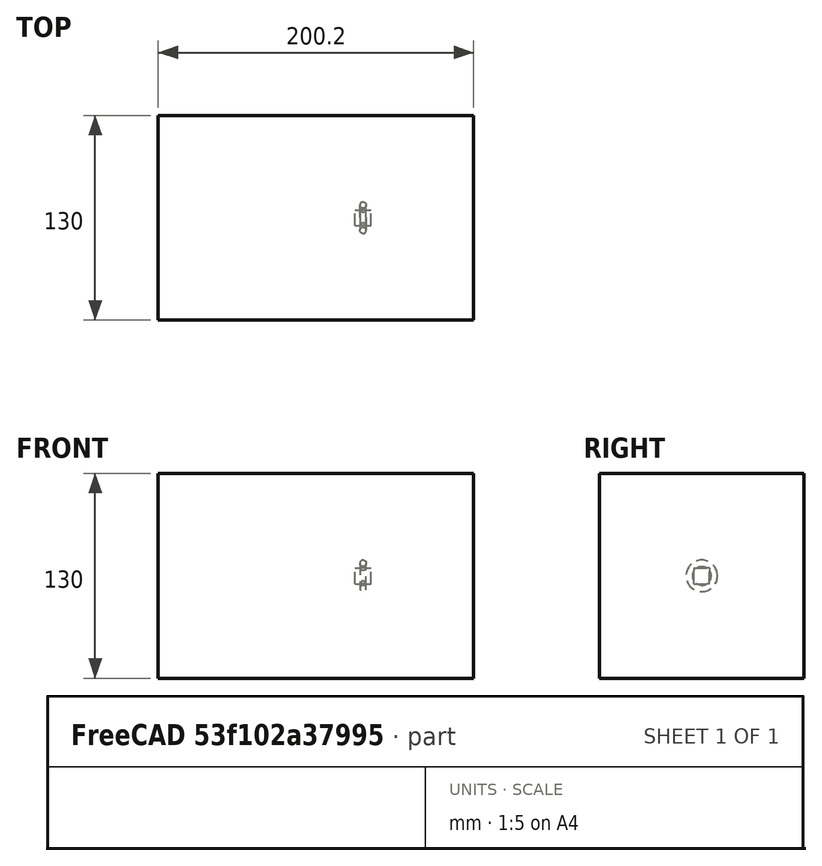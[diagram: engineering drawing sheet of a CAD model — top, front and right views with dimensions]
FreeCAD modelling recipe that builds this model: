
FCSTD DOCUMENT  (FreeCAD 0.21R33694 (Git))
Label: polarArray-7-array-rotated-translated
License: All rights reserved
objects: App::DocumentObjectGroupPython×1251, Part::FeaturePython×4, App::Part×2, Part::MultiFuse×1
note: 4 computed .brp shape members not serialized (recipe doc carries the construction recipe); baked Part::Feature solids carry a one-line shape summary decoded from their .brp

FEATURE [App::DocumentObjectGroupPython] HALFPI  # scripted group (container) (typed FeaturePython)
  name = HALFPI
  value = pi/2.
FEATURE [App::DocumentObjectGroupPython] PI  # scripted group (container) (typed FeaturePython)
  name = PI
  value = 1.*pi
FEATURE [App::DocumentObjectGroupPython] TWOPI  # scripted group (container) (typed FeaturePython)
  name = TWOPI
  value = 2.*pi
FEATURE [App::DocumentObjectGroupPython] Constants  # scripted group (container) (typed FeaturePython)
  Group = -> [HALFPI,PI,TWOPI]
FEATURE [App::DocumentObjectGroupPython] Variables  # scripted group (container) (typed FeaturePython)
FEATURE [App::DocumentObjectGroupPython] Quantities  # scripted group (container) (typed FeaturePython)
FEATURE [App::DocumentObjectGroupPython] Isotopes  # scripted group (container) (typed FeaturePython)
FEATURE [App::DocumentObjectGroupPython] Elements  # scripted group (container) (typed FeaturePython)
FEATURE [App::DocumentObjectGroupPython] Matrix  # scripted group (container) (typed FeaturePython)
FEATURE [App::DocumentObjectGroupPython] Surfaces  # scripted group (container) (typed FeaturePython)
FEATURE [App::DocumentObjectGroupPython] Opticals  # scripted group (container) (typed FeaturePython)
  Group = -> [Matrix,Surfaces]
FEATURE [App::DocumentObjectGroupPython] G4Isotopes  # scripted group (container) (typed FeaturePython)
FEATURE [App::DocumentObjectGroupPython] H_element  # scripted group (container) (typed FeaturePython)
  Z = 1
  atom_value = 1.008
  formula = H
  name = H_element
FEATURE [App::DocumentObjectGroupPython] He_element  # scripted group (container) (typed FeaturePython)
  Z = 2
  atom_value = 4.0026
  formula = He
  name = He_element
FEATURE [App::DocumentObjectGroupPython] Li_element  # scripted group (container) (typed FeaturePython)
  Z = 3
  atom_value = 6.94
  formula = Li
  name = Li_element
FEATURE [App::DocumentObjectGroupPython] Be_element  # scripted group (container) (typed FeaturePython)
  Z = 4
  atom_value = 9.01218
  formula = Be
  name = Be_element
FEATURE [App::DocumentObjectGroupPython] B_element  # scripted group (container) (typed FeaturePython)
  Z = 5
  atom_value = 10.81
  formula = B
  name = B_element
FEATURE [App::DocumentObjectGroupPython] C_element  # scripted group (container) (typed FeaturePython)
  Z = 6
  atom_value = 12.011
  formula = C
  name = C_element
FEATURE [App::DocumentObjectGroupPython] N_element  # scripted group (container) (typed FeaturePython)
  Z = 7
  atom_value = 14.007
  formula = N
  name = N_element
FEATURE [App::DocumentObjectGroupPython] O_element  # scripted group (container) (typed FeaturePython)
  Z = 8
  atom_value = 15.999
  formula = O
  name = O_element
FEATURE [App::DocumentObjectGroupPython] F_element  # scripted group (container) (typed FeaturePython)
  Z = 9
  atom_value = 18.9984
  formula = F
  name = F_element
FEATURE [App::DocumentObjectGroupPython] Ne_element  # scripted group (container) (typed FeaturePython)
  Z = 10
  atom_value = 20.1797
  formula = Ne
  name = Ne_element
FEATURE [App::DocumentObjectGroupPython] Na_element  # scripted group (container) (typed FeaturePython)
  Z = 11
  atom_value = 22.9898
  formula = Na
  name = Na_element
FEATURE [App::DocumentObjectGroupPython] Mg_element  # scripted group (container) (typed FeaturePython)
  Z = 12
  atom_value = 24.305
  formula = Mg
  name = Mg_element
FEATURE [App::DocumentObjectGroupPython] Al_element  # scripted group (container) (typed FeaturePython)
  Z = 13
  atom_value = 26.9815
  formula = Al
  name = Al_element
FEATURE [App::DocumentObjectGroupPython] Si_element  # scripted group (container) (typed FeaturePython)
  Z = 14
  atom_value = 28.085
  formula = Si
  name = Si_element
FEATURE [App::DocumentObjectGroupPython] P_element  # scripted group (container) (typed FeaturePython)
  Z = 15
  atom_value = 30.9738
  formula = P
  name = P_element
FEATURE [App::DocumentObjectGroupPython] S_element  # scripted group (container) (typed FeaturePython)
  Z = 16
  atom_value = 32.06
  formula = S
  name = S_element
FEATURE [App::DocumentObjectGroupPython] Cl_element  # scripted group (container) (typed FeaturePython)
  Z = 17
  atom_value = 35.45
  formula = Cl
  name = Cl_element
FEATURE [App::DocumentObjectGroupPython] Ar_element  # scripted group (container) (typed FeaturePython)
  Z = 18
  atom_value = 39.95
  formula = Ar
  name = Ar_element
FEATURE [App::DocumentObjectGroupPython] K_element  # scripted group (container) (typed FeaturePython)
  Z = 19
  atom_value = 39.0983
  formula = K
  name = K_element
FEATURE [App::DocumentObjectGroupPython] Ca_element  # scripted group (container) (typed FeaturePython)
  Z = 20
  atom_value = 40.078
  formula = Ca
  name = Ca_element
FEATURE [App::DocumentObjectGroupPython] Sc_element  # scripted group (container) (typed FeaturePython)
  Z = 21
  atom_value = 44.9559
  formula = Sc
  name = Sc_element
FEATURE [App::DocumentObjectGroupPython] Ti_element  # scripted group (container) (typed FeaturePython)
  Z = 22
  atom_value = 47.867
  formula = Ti
  name = Ti_element
FEATURE [App::DocumentObjectGroupPython] V_element  # scripted group (container) (typed FeaturePython)
  Z = 23
  atom_value = 50.9415
  formula = V
  name = V_element
FEATURE [App::DocumentObjectGroupPython] Cr_element  # scripted group (container) (typed FeaturePython)
  Z = 24
  atom_value = 51.9961
  formula = Cr
  name = Cr_element
FEATURE [App::DocumentObjectGroupPython] Mn_element  # scripted group (container) (typed FeaturePython)
  Z = 25
  atom_value = 54.938
  formula = Mn
  name = Mn_element
FEATURE [App::DocumentObjectGroupPython] Fe_element  # scripted group (container) (typed FeaturePython)
  Z = 26
  atom_value = 55.845
  formula = Fe
  name = Fe_element
FEATURE [App::DocumentObjectGroupPython] Co_element  # scripted group (container) (typed FeaturePython)
  Z = 27
  atom_value = 58.9332
  formula = Co
  name = Co_element
FEATURE [App::DocumentObjectGroupPython] Ni_element  # scripted group (container) (typed FeaturePython)
  Z = 28
  atom_value = 58.6934
  formula = Ni
  name = Ni_element
FEATURE [App::DocumentObjectGroupPython] Cu_element  # scripted group (container) (typed FeaturePython)
  Z = 29
  atom_value = 63.546
  formula = Cu
  name = Cu_element
FEATURE [App::DocumentObjectGroupPython] Zn_element  # scripted group (container) (typed FeaturePython)
  Z = 30
  atom_value = 65.38
  formula = Zn
  name = Zn_element
FEATURE [App::DocumentObjectGroupPython] Ga_element  # scripted group (container) (typed FeaturePython)
  Z = 31
  atom_value = 69.723
  formula = Ga
  name = Ga_element
FEATURE [App::DocumentObjectGroupPython] Ge_element  # scripted group (container) (typed FeaturePython)
  Z = 32
  atom_value = 72.63
  formula = Ge
  name = Ge_element
FEATURE [App::DocumentObjectGroupPython] As_element  # scripted group (container) (typed FeaturePython)
  Z = 33
  atom_value = 74.9216
  formula = As
  name = As_element
FEATURE [App::DocumentObjectGroupPython] Se_element  # scripted group (container) (typed FeaturePython)
  Z = 34
  atom_value = 78.971
  formula = Se
  name = Se_element
FEATURE [App::DocumentObjectGroupPython] Br_element  # scripted group (container) (typed FeaturePython)
  Z = 35
  atom_value = 79.904
  formula = Br
  name = Br_element
FEATURE [App::DocumentObjectGroupPython] Kr_element  # scripted group (container) (typed FeaturePython)
  Z = 36
  atom_value = 83.798
  formula = Kr
  name = Kr_element
FEATURE [App::DocumentObjectGroupPython] Rb_element  # scripted group (container) (typed FeaturePython)
  Z = 37
  atom_value = 85.4678
  formula = Rb
  name = Rb_element
FEATURE [App::DocumentObjectGroupPython] Sr_element  # scripted group (container) (typed FeaturePython)
  Z = 38
  atom_value = 87.62
  formula = Sr
  name = Sr_element
FEATURE [App::DocumentObjectGroupPython] Y_element  # scripted group (container) (typed FeaturePython)
  Z = 39
  atom_value = 88.9058
  formula = Y
  name = Y_element
FEATURE [App::DocumentObjectGroupPython] Zr_element  # scripted group (container) (typed FeaturePython)
  Z = 40
  atom_value = 91.224
  formula = Zr
  name = Zr_element
FEATURE [App::DocumentObjectGroupPython] Nb_element  # scripted group (container) (typed FeaturePython)
  Z = 41
  atom_value = 92.9064
  formula = Nb
  name = Nb_element
FEATURE [App::DocumentObjectGroupPython] Mo_element  # scripted group (container) (typed FeaturePython)
  Z = 42
  atom_value = 95.95
  formula = Mo
  name = Mo_element
FEATURE [App::DocumentObjectGroupPython] Tc_element  # scripted group (container) (typed FeaturePython)
  Z = 43
  atom_value = 97
  formula = Tc
  name = Tc_element
FEATURE [App::DocumentObjectGroupPython] Ru_element  # scripted group (container) (typed FeaturePython)
  Z = 44
  atom_value = 101.07
  formula = Ru
  name = Ru_element
FEATURE [App::DocumentObjectGroupPython] Rh_element  # scripted group (container) (typed FeaturePython)
  Z = 45
  atom_value = 102.905
  formula = Rh
  name = Rh_element
FEATURE [App::DocumentObjectGroupPython] Pd_element  # scripted group (container) (typed FeaturePython)
  Z = 46
  atom_value = 106.42
  formula = Pd
  name = Pd_element
FEATURE [App::DocumentObjectGroupPython] Ag_element  # scripted group (container) (typed FeaturePython)
  Z = 47
  atom_value = 107.868
  formula = Ag
  name = Ag_element
FEATURE [App::DocumentObjectGroupPython] Cd_element  # scripted group (container) (typed FeaturePython)
  Z = 48
  atom_value = 112.414
  formula = Cd
  name = Cd_element
FEATURE [App::DocumentObjectGroupPython] In_element  # scripted group (container) (typed FeaturePython)
  Z = 49
  atom_value = 114.818
  formula = In
  name = In_element
FEATURE [App::DocumentObjectGroupPython] Sn_element  # scripted group (container) (typed FeaturePython)
  Z = 50
  atom_value = 118.71
  formula = Sn
  name = Sn_element
FEATURE [App::DocumentObjectGroupPython] Sb_element  # scripted group (container) (typed FeaturePython)
  Z = 51
  atom_value = 121.76
  formula = Sb
  name = Sb_element
FEATURE [App::DocumentObjectGroupPython] Te_element  # scripted group (container) (typed FeaturePython)
  Z = 52
  atom_value = 127.6
  formula = Te
  name = Te_element
FEATURE [App::DocumentObjectGroupPython] I_element  # scripted group (container) (typed FeaturePython)
  Z = 53
  atom_value = 126.904
  formula = I
  name = I_element
FEATURE [App::DocumentObjectGroupPython] Xe_element  # scripted group (container) (typed FeaturePython)
  Z = 54
  atom_value = 131.293
  formula = Xe
  name = Xe_element
FEATURE [App::DocumentObjectGroupPython] Cs_element  # scripted group (container) (typed FeaturePython)
  Z = 55
  atom_value = 132.905
  formula = Cs
  name = Cs_element
FEATURE [App::DocumentObjectGroupPython] Ba_element  # scripted group (container) (typed FeaturePython)
  Z = 56
  atom_value = 137.327
  formula = Ba
  name = Ba_element
FEATURE [App::DocumentObjectGroupPython] La_element  # scripted group (container) (typed FeaturePython)
  Z = 57
  atom_value = 138.905
  formula = La
  name = La_element
FEATURE [App::DocumentObjectGroupPython] Ce_element  # scripted group (container) (typed FeaturePython)
  Z = 58
  atom_value = 140.116
  formula = Ce
  name = Ce_element
FEATURE [App::DocumentObjectGroupPython] Pr_element  # scripted group (container) (typed FeaturePython)
  Z = 59
  atom_value = 140.908
  formula = Pr
  name = Pr_element
FEATURE [App::DocumentObjectGroupPython] Nd_element  # scripted group (container) (typed FeaturePython)
  Z = 60
  atom_value = 144.242
  formula = Nd
  name = Nd_element
FEATURE [App::DocumentObjectGroupPython] Pm_element  # scripted group (container) (typed FeaturePython)
  Z = 61
  atom_value = 145
  formula = Pm
  name = Pm_element
FEATURE [App::DocumentObjectGroupPython] Sm_element  # scripted group (container) (typed FeaturePython)
  Z = 62
  atom_value = 150.36
  formula = Sm
  name = Sm_element
FEATURE [App::DocumentObjectGroupPython] Eu_element  # scripted group (container) (typed FeaturePython)
  Z = 63
  atom_value = 151.964
  formula = Eu
  name = Eu_element
FEATURE [App::DocumentObjectGroupPython] Gd_element  # scripted group (container) (typed FeaturePython)
  Z = 64
  atom_value = 157.25
  formula = Gd
  name = Gd_element
FEATURE [App::DocumentObjectGroupPython] Tb_element  # scripted group (container) (typed FeaturePython)
  Z = 65
  atom_value = 158.925
  formula = Tb
  name = Tb_element
FEATURE [App::DocumentObjectGroupPython] Dy_element  # scripted group (container) (typed FeaturePython)
  Z = 66
  atom_value = 162.5
  formula = Dy
  name = Dy_element
FEATURE [App::DocumentObjectGroupPython] Ho_element  # scripted group (container) (typed FeaturePython)
  Z = 67
  atom_value = 164.93
  formula = Ho
  name = Ho_element
FEATURE [App::DocumentObjectGroupPython] Er_element  # scripted group (container) (typed FeaturePython)
  Z = 68
  atom_value = 167.259
  formula = Er
  name = Er_element
FEATURE [App::DocumentObjectGroupPython] Tm_element  # scripted group (container) (typed FeaturePython)
  Z = 69
  atom_value = 168.934
  formula = Tm
  name = Tm_element
FEATURE [App::DocumentObjectGroupPython] Yb_element  # scripted group (container) (typed FeaturePython)
  Z = 70
  atom_value = 173.045
  formula = Yb
  name = Yb_element
FEATURE [App::DocumentObjectGroupPython] Lu_element  # scripted group (container) (typed FeaturePython)
  Z = 71
  atom_value = 174.967
  formula = Lu
  name = Lu_element
FEATURE [App::DocumentObjectGroupPython] Hf_element  # scripted group (container) (typed FeaturePython)
  Z = 72
  atom_value = 178.49
  formula = Hf
  name = Hf_element
FEATURE [App::DocumentObjectGroupPython] Ta_element  # scripted group (container) (typed FeaturePython)
  Z = 73
  atom_value = 180.948
  formula = Ta
  name = Ta_element
FEATURE [App::DocumentObjectGroupPython] W_element  # scripted group (container) (typed FeaturePython)
  Z = 74
  atom_value = 183.84
  formula = W
  name = W_element
FEATURE [App::DocumentObjectGroupPython] Re_element  # scripted group (container) (typed FeaturePython)
  Z = 75
  atom_value = 186.207
  formula = Re
  name = Re_element
FEATURE [App::DocumentObjectGroupPython] Os_element  # scripted group (container) (typed FeaturePython)
  Z = 76
  atom_value = 190.23
  formula = Os
  name = Os_element
FEATURE [App::DocumentObjectGroupPython] Ir_element  # scripted group (container) (typed FeaturePython)
  Z = 77
  atom_value = 192.217
  formula = Ir
  name = Ir_element
FEATURE [App::DocumentObjectGroupPython] Pt_element  # scripted group (container) (typed FeaturePython)
  Z = 78
  atom_value = 195.084
  formula = Pt
  name = Pt_element
FEATURE [App::DocumentObjectGroupPython] Au_element  # scripted group (container) (typed FeaturePython)
  Z = 79
  atom_value = 196.967
  formula = Au
  name = Au_element
FEATURE [App::DocumentObjectGroupPython] Hg_element  # scripted group (container) (typed FeaturePython)
  Z = 80
  atom_value = 200.592
  formula = Hg
  name = Hg_element
FEATURE [App::DocumentObjectGroupPython] Tl_element  # scripted group (container) (typed FeaturePython)
  Z = 81
  atom_value = 204.38
  formula = Tl
  name = Tl_element
FEATURE [App::DocumentObjectGroupPython] Pb_element  # scripted group (container) (typed FeaturePython)
  Z = 82
  atom_value = 207.2
  formula = Pb
  name = Pb_element
FEATURE [App::DocumentObjectGroupPython] Bi_element  # scripted group (container) (typed FeaturePython)
  Z = 83
  atom_value = 208.98
  formula = Bi
  name = Bi_element
FEATURE [App::DocumentObjectGroupPython] Po_element  # scripted group (container) (typed FeaturePython)
  Z = 84
  atom_value = 209
  formula = Po
  name = Po_element
FEATURE [App::DocumentObjectGroupPython] At_element  # scripted group (container) (typed FeaturePython)
  Z = 85
  atom_value = 210
  formula = At
  name = At_element
FEATURE [App::DocumentObjectGroupPython] Rn_element  # scripted group (container) (typed FeaturePython)
  Z = 86
  atom_value = 222
  formula = Rn
  name = Rn_element
FEATURE [App::DocumentObjectGroupPython] Fr_element  # scripted group (container) (typed FeaturePython)
  Z = 87
  atom_value = 223
  formula = Fr
  name = Fr_element
FEATURE [App::DocumentObjectGroupPython] Ra_element  # scripted group (container) (typed FeaturePython)
  Z = 88
  atom_value = 226
  formula = Ra
  name = Ra_element
FEATURE [App::DocumentObjectGroupPython] Ac_element  # scripted group (container) (typed FeaturePython)
  Z = 89
  atom_value = 227
  formula = Ac
  name = Ac_element
FEATURE [App::DocumentObjectGroupPython] Th_element  # scripted group (container) (typed FeaturePython)
  Z = 90
  atom_value = 232.038
  formula = Th
  name = Th_element
FEATURE [App::DocumentObjectGroupPython] Pa_element  # scripted group (container) (typed FeaturePython)
  Z = 91
  atom_value = 231.036
  formula = Pa
  name = Pa_element
FEATURE [App::DocumentObjectGroupPython] U_element  # scripted group (container) (typed FeaturePython)
  Z = 92
  atom_value = 238.029
  formula = U
  name = U_element
FEATURE [App::DocumentObjectGroupPython] Np_element  # scripted group (container) (typed FeaturePython)
  Z = 93
  atom_value = 237
  formula = Np
  name = Np_element
FEATURE [App::DocumentObjectGroupPython] Pu_element  # scripted group (container) (typed FeaturePython)
  Z = 94
  atom_value = 244
  formula = Pu
  name = Pu_element
FEATURE [App::DocumentObjectGroupPython] Am_element  # scripted group (container) (typed FeaturePython)
  Z = 95
  atom_value = 243
  formula = Am
  name = Am_element
FEATURE [App::DocumentObjectGroupPython] Cm_element  # scripted group (container) (typed FeaturePython)
  Z = 96
  atom_value = 247
  formula = Cm
  name = Cm_element
FEATURE [App::DocumentObjectGroupPython] Bk_element  # scripted group (container) (typed FeaturePython)
  Z = 97
  atom_value = 247
  formula = Bk
  name = Bk_element
FEATURE [App::DocumentObjectGroupPython] Cf_element  # scripted group (container) (typed FeaturePython)
  Z = 98
  atom_value = 251
  formula = Cf
  name = Cf_element
FEATURE [App::DocumentObjectGroupPython] G4Elements  # scripted group (container) (typed FeaturePython)
  Group = -> [H_element,He_element,Li_element,Be_element,B_element,C_element,N_element,O_element,F_element,Ne_element,Na_element,Mg_element,Al_element,Si_element,P_element,S_element,Cl_element,Ar_element,K_element,Ca_element,Sc_element,Ti_element,V_element,Cr_element,Mn_element,Fe_element,Co_element,Ni_element,Cu_element,Zn_element,Ga_element,Ge_element,As_element,Se_element,Br_element,Kr_element,Rb_element,+61 more]
FEATURE [App::DocumentObjectGroupPython] H_element001  label="H_element : 0.101"  # scripted group (container) (typed FeaturePython)
  n = 0.101327
FEATURE [App::DocumentObjectGroupPython] C_element001  label="C_element : 0.775"  # scripted group (container) (typed FeaturePython)
  n = 0.7755
FEATURE [App::DocumentObjectGroupPython] N_element001  label="N_element : 0.035"  # scripted group (container) (typed FeaturePython)
  n = 0.035057
FEATURE [App::DocumentObjectGroupPython] O_element001  label="O_element : 0.052"  # scripted group (container) (typed FeaturePython)
  n = 0.0523159
FEATURE [App::DocumentObjectGroupPython] F_element001  label="F_element : 0.017"  # scripted group (container) (typed FeaturePython)
  n = 0.017422
FEATURE [App::DocumentObjectGroupPython] Ca_element001  label="Ca_element : 0.018"  # scripted group (container) (typed FeaturePython)
  n = 0.018378
FEATURE [App::DocumentObjectGroupPython] G4_A_150_TISSUE  label="G4_A-150_TISSUE"  # scripted group (container) (typed FeaturePython)
  Dunit = g/cm3
  Dvalue = 1.127
  Group = -> [H_element001,C_element001,N_element001,O_element001,F_element001,Ca_element001]
  conduct = 2
  density = 1
  expand = 3
  formula = G4_A-150_TISSUE
  name = G4_A-150_TISSUE
  specific = 4
FEATURE [App::DocumentObjectGroupPython] C_element002  label="C_element : 3"  # scripted group (container) (typed FeaturePython)
  n = 3
  ref = C_element
FEATURE [App::DocumentObjectGroupPython] H_element002  label="H_element : 6"  # scripted group (container) (typed FeaturePython)
  n = 6
  ref = H_element
FEATURE [App::DocumentObjectGroupPython] O_element002  label="O_element : 1"  # scripted group (container) (typed FeaturePython)
  n = 1
  ref = O_element
FEATURE [App::DocumentObjectGroupPython] G4_ACETONE  # scripted group (container) (typed FeaturePython)
  Dunit = g/cm3
  Dvalue = 0.7899
  Group = -> [C_element002,H_element002,O_element002]
  conduct = 2
  density = 1
  expand = 3
  formula = G4_ACETONE
  name = G4_ACETONE
  specific = 4
FEATURE [App::DocumentObjectGroupPython] C_element003  label="C_element : 2"  # scripted group (container) (typed FeaturePython)
  n = 2
  ref = C_element
FEATURE [App::DocumentObjectGroupPython] H_element003  label="H_element : 2"  # scripted group (container) (typed FeaturePython)
  n = 2
  ref = H_element
FEATURE [App::DocumentObjectGroupPython] G4_ACETYLENE  # scripted group (container) (typed FeaturePython)
  Dunit = g/cm3
  Dvalue = 0.0010967
  Group = -> [C_element003,H_element003]
  conduct = 2
  density = 1
  expand = 3
  formula = G4_ACETYLENE
  name = G4_ACETYLENE
  specific = 4
FEATURE [App::DocumentObjectGroupPython] C_element004  label="C_element : 5"  # scripted group (container) (typed FeaturePython)
  n = 5
  ref = C_element
FEATURE [App::DocumentObjectGroupPython] H_element004  label="H_element : 5"  # scripted group (container) (typed FeaturePython)
  n = 5
  ref = H_element
FEATURE [App::DocumentObjectGroupPython] N_element002  label="N_element : 5"  # scripted group (container) (typed FeaturePython)
  n = 5
  ref = N_element
FEATURE [App::DocumentObjectGroupPython] G4_ADENINE  # scripted group (container) (typed FeaturePython)
  Dunit = g/cm3
  Dvalue = 1.6
  Group = -> [C_element004,H_element004,N_element002]
  conduct = 2
  density = 1
  expand = 3
  formula = G4_ADENINE
  name = G4_ADENINE
  specific = 4
FEATURE [App::DocumentObjectGroupPython] H_element005  label="H_element : 0.114"  # scripted group (container) (typed FeaturePython)
  n = 0.114
FEATURE [App::DocumentObjectGroupPython] C_element005  label="C_element : 0.598"  # scripted group (container) (typed FeaturePython)
  n = 0.598
FEATURE [App::DocumentObjectGroupPython] N_element003  label="N_element : 0.007"  # scripted group (container) (typed FeaturePython)
  n = 0.007
FEATURE [App::DocumentObjectGroupPython] O_element003  label="O_element : 0.278"  # scripted group (container) (typed FeaturePython)
  n = 0.278
FEATURE [App::DocumentObjectGroupPython] Na_element001  label="Na_element : 0.001"  # scripted group (container) (typed FeaturePython)
  n = 0.001
FEATURE [App::DocumentObjectGroupPython] S_element001  label="S_element : 0.001"  # scripted group (container) (typed FeaturePython)
  n = 0.001
FEATURE [App::DocumentObjectGroupPython] Cl_element001  label="Cl_element : 0.001"  # scripted group (container) (typed FeaturePython)
  n = 0.001
FEATURE [App::DocumentObjectGroupPython] G4_ADIPOSE_TISSUE_ICRP  # scripted group (container) (typed FeaturePython)
  Dunit = g/cm3
  Dvalue = 0.95
  Group = -> [H_element005,C_element005,N_element003,O_element003,Na_element001,S_element001,Cl_element001]
  conduct = 2
  density = 1
  expand = 3
  formula = G4_ADIPOSE_TISSUE_ICRP
  name = G4_ADIPOSE_TISSUE_ICRP
  specific = 4
FEATURE [App::DocumentObjectGroupPython] C_element006  label="C_element : 0.000"  # scripted group (container) (typed FeaturePython)
  n = 0.000124
FEATURE [App::DocumentObjectGroupPython] N_element004  label="N_element : 0.755"  # scripted group (container) (typed FeaturePython)
  n = 0.755268
FEATURE [App::DocumentObjectGroupPython] O_element004  label="O_element : 0.232"  # scripted group (container) (typed FeaturePython)
  n = 0.231781
FEATURE [App::DocumentObjectGroupPython] Ar_element001  label="Ar_element : 0.013"  # scripted group (container) (typed FeaturePython)
  n = 0.012827
FEATURE [App::DocumentObjectGroupPython] G4_AIR  # scripted group (container) (typed FeaturePython)
  Dunit = g/cm3
  Dvalue = 0.00120479
  Group = -> [C_element006,N_element004,O_element004,Ar_element001]
  conduct = 2
  density = 1
  expand = 3
  formula = G4_AIR
  name = G4_AIR
  specific = 4
FEATURE [App::DocumentObjectGroupPython] C_element007  label="C_element : 006"  # scripted group (container) (typed FeaturePython)
  n = 3
  ref = C_element
FEATURE [App::DocumentObjectGroupPython] H_element006  label="H_element : 7"  # scripted group (container) (typed FeaturePython)
  n = 7
  ref = H_element
FEATURE [App::DocumentObjectGroupPython] N_element005  label="N_element : 1"  # scripted group (container) (typed FeaturePython)
  n = 1
  ref = N_element
FEATURE [App::DocumentObjectGroupPython] O_element005  label="O_element : 2"  # scripted group (container) (typed FeaturePython)
  n = 2
  ref = O_element
FEATURE [App::DocumentObjectGroupPython] G4_ALANINE  # scripted group (container) (typed FeaturePython)
  Dunit = g/cm3
  Dvalue = 1.42
  Group = -> [C_element007,H_element006,N_element005,O_element005]
  conduct = 2
  density = 1
  expand = 3
  formula = G4_ALANINE
  name = G4_ALANINE
  specific = 4
FEATURE [App::DocumentObjectGroupPython] Al_element001  label="Al_element : 2"  # scripted group (container) (typed FeaturePython)
  n = 2
  ref = Al_element
FEATURE [App::DocumentObjectGroupPython] O_element006  label="O_element : 3"  # scripted group (container) (typed FeaturePython)
  n = 3
  ref = O_element
FEATURE [App::DocumentObjectGroupPython] G4_ALUMINUM_OXIDE  # scripted group (container) (typed FeaturePython)
  Dunit = g/cm3
  Dvalue = 3.97
  Group = -> [Al_element001,O_element006]
  conduct = 2
  density = 1
  expand = 3
  formula = G4_ALUMINUM_OXIDE
  name = G4_ALUMINUM_OXIDE
  specific = 4
FEATURE [App::DocumentObjectGroupPython] H_element007  label="H_element : 0.106"  # scripted group (container) (typed FeaturePython)
  n = 0.10593
FEATURE [App::DocumentObjectGroupPython] C_element008  label="C_element : 0.789"  # scripted group (container) (typed FeaturePython)
  n = 0.788974
FEATURE [App::DocumentObjectGroupPython] O_element007  label="O_element : 0.105"  # scripted group (container) (typed FeaturePython)
  n = 0.105096
FEATURE [App::DocumentObjectGroupPython] G4_AMBER  # scripted group (container) (typed FeaturePython)
  Dunit = g/cm3
  Dvalue = 1.1
  Group = -> [H_element007,C_element008,O_element007]
  conduct = 2
  density = 1
  expand = 3
  formula = G4_AMBER
  name = G4_AMBER
  specific = 4
FEATURE [App::DocumentObjectGroupPython] N_element006  label="N_element : 006"  # scripted group (container) (typed FeaturePython)
  n = 1
  ref = N_element
FEATURE [App::DocumentObjectGroupPython] H_element008  label="H_element : 3"  # scripted group (container) (typed FeaturePython)
  n = 3
  ref = H_element
FEATURE [App::DocumentObjectGroupPython] G4_AMMONIA  # scripted group (container) (typed FeaturePython)
  Dunit = g/cm3
  Dvalue = 0.000826019
  Group = -> [N_element006,H_element008]
  conduct = 2
  density = 1
  expand = 3
  formula = G4_AMMONIA
  name = G4_AMMONIA
  specific = 4
FEATURE [App::DocumentObjectGroupPython] C_element009  label="C_element : 6"  # scripted group (container) (typed FeaturePython)
  n = 6
  ref = C_element
FEATURE [App::DocumentObjectGroupPython] H_element009  label="H_element : 008"  # scripted group (container) (typed FeaturePython)
  n = 7
  ref = H_element
FEATURE [App::DocumentObjectGroupPython] N_element007  label="N_element : 007"  # scripted group (container) (typed FeaturePython)
  n = 1
  ref = N_element
FEATURE [App::DocumentObjectGroupPython] G4_ANILINE  # scripted group (container) (typed FeaturePython)
  Dunit = g/cm3
  Dvalue = 1.0235
  Group = -> [C_element009,H_element009,N_element007]
  conduct = 2
  density = 1
  expand = 3
  formula = G4_ANILINE
  name = G4_ANILINE
  specific = 4
FEATURE [App::DocumentObjectGroupPython] C_element010  label="C_element : 14"  # scripted group (container) (typed FeaturePython)
  n = 14
  ref = C_element
FEATURE [App::DocumentObjectGroupPython] H_element010  label="H_element : 10"  # scripted group (container) (typed FeaturePython)
  n = 10
  ref = H_element
FEATURE [App::DocumentObjectGroupPython] G4_ANTHRACENE  # scripted group (container) (typed FeaturePython)
  Dunit = g/cm3
  Dvalue = 1.283
  Group = -> [C_element010,H_element010]
  conduct = 2
  density = 1
  expand = 3
  formula = G4_ANTHRACENE
  name = G4_ANTHRACENE
  specific = 4
FEATURE [App::DocumentObjectGroupPython] H_element011  label="H_element : 0.065"  # scripted group (container) (typed FeaturePython)
  n = 0.0654709
FEATURE [App::DocumentObjectGroupPython] C_element011  label="C_element : 0.537"  # scripted group (container) (typed FeaturePython)
  n = 0.536944
FEATURE [App::DocumentObjectGroupPython] N_element008  label="N_element : 0.021"  # scripted group (container) (typed FeaturePython)
  n = 0.0215
FEATURE [App::DocumentObjectGroupPython] O_element008  label="O_element : 0.032"  # scripted group (container) (typed FeaturePython)
  n = 0.032085
FEATURE [App::DocumentObjectGroupPython] F_element002  label="F_element : 0.167"  # scripted group (container) (typed FeaturePython)
  n = 0.167411
FEATURE [App::DocumentObjectGroupPython] Ca_element002  label="Ca_element : 0.177"  # scripted group (container) (typed FeaturePython)
  n = 0.176589
FEATURE [App::DocumentObjectGroupPython] G4_B_100_BONE  label="G4_B-100_BONE"  # scripted group (container) (typed FeaturePython)
  Dunit = g/cm3
  Dvalue = 1.45
  Group = -> [H_element011,C_element011,N_element008,O_element008,F_element002,Ca_element002]
  conduct = 2
  density = 1
  expand = 3
  formula = G4_B-100_BONE
  name = G4_B-100_BONE
  specific = 4
FEATURE [App::DocumentObjectGroupPython] H_element012  label="H_element : 0.057"  # scripted group (container) (typed FeaturePython)
  n = 0.057441
FEATURE [App::DocumentObjectGroupPython] C_element012  label="C_element : 0.790"  # scripted group (container) (typed FeaturePython)
  n = 0.774591
FEATURE [App::DocumentObjectGroupPython] O_element009  label="O_element : 0.168"  # scripted group (container) (typed FeaturePython)
  n = 0.167968
FEATURE [App::DocumentObjectGroupPython] G4_BAKELITE  # scripted group (container) (typed FeaturePython)
  Dunit = g/cm3
  Dvalue = 1.25
  Group = -> [H_element012,C_element012,O_element009]
  conduct = 2
  density = 1
  expand = 3
  formula = G4_BAKELITE
  name = G4_BAKELITE
  specific = 4
FEATURE [App::DocumentObjectGroupPython] Ba_element001  label="Ba_element : 1"  # scripted group (container) (typed FeaturePython)
  n = 1
  ref = Ba_element
FEATURE [App::DocumentObjectGroupPython] F_element003  label="F_element : 2"  # scripted group (container) (typed FeaturePython)
  n = 2
  ref = F_element
FEATURE [App::DocumentObjectGroupPython] G4_BARIUM_FLUORIDE  # scripted group (container) (typed FeaturePython)
  Dunit = g/cm3
  Dvalue = 4.89
  Group = -> [Ba_element001,F_element003]
  conduct = 2
  density = 1
  expand = 3
  formula = G4_BARIUM_FLUORIDE
  name = G4_BARIUM_FLUORIDE
  specific = 4
FEATURE [App::DocumentObjectGroupPython] Ba_element002  label="Ba_element : 002"  # scripted group (container) (typed FeaturePython)
  n = 1
  ref = Ba_element
FEATURE [App::DocumentObjectGroupPython] S_element002  label="S_element : 1"  # scripted group (container) (typed FeaturePython)
  n = 1
  ref = S_element
FEATURE [App::DocumentObjectGroupPython] O_element010  label="O_element : 4"  # scripted group (container) (typed FeaturePython)
  n = 4
  ref = O_element
FEATURE [App::DocumentObjectGroupPython] G4_BARIUM_SULFATE  # scripted group (container) (typed FeaturePython)
  Dunit = g/cm3
  Dvalue = 4.5
  Group = -> [Ba_element002,S_element002,O_element010]
  conduct = 2
  density = 1
  expand = 3
  formula = G4_BARIUM_SULFATE
  name = G4_BARIUM_SULFATE
  specific = 4
FEATURE [App::DocumentObjectGroupPython] C_element013  label="C_element : 007"  # scripted group (container) (typed FeaturePython)
  n = 6
  ref = C_element
FEATURE [App::DocumentObjectGroupPython] H_element013  label="H_element : 009"  # scripted group (container) (typed FeaturePython)
  n = 6
  ref = H_element
FEATURE [App::DocumentObjectGroupPython] G4_BENZENE  # scripted group (container) (typed FeaturePython)
  Dunit = g/cm3
  Dvalue = 0.87865
  Group = -> [C_element013,H_element013]
  conduct = 2
  density = 1
  expand = 3
  formula = G4_BENZENE
  name = G4_BENZENE
  specific = 4
FEATURE [App::DocumentObjectGroupPython] Be_element001  label="Be_element : 1"  # scripted group (container) (typed FeaturePython)
  n = 1
  ref = Be_element
FEATURE [App::DocumentObjectGroupPython] O_element011  label="O_element : 005"  # scripted group (container) (typed FeaturePython)
  n = 1
  ref = O_element
FEATURE [App::DocumentObjectGroupPython] G4_BERYLLIUM_OXIDE  # scripted group (container) (typed FeaturePython)
  Dunit = g/cm3
  Dvalue = 3.01
  Group = -> [Be_element001,O_element011]
  conduct = 2
  density = 1
  expand = 3
  formula = G4_BERYLLIUM_OXIDE
  name = G4_BERYLLIUM_OXIDE
  specific = 4
FEATURE [App::DocumentObjectGroupPython] Bi_element001  label="Bi_element : 4"  # scripted group (container) (typed FeaturePython)
  n = 4
  ref = Bi_element
FEATURE [App::DocumentObjectGroupPython] Ge_element001  label="Ge_element : 3"  # scripted group (container) (typed FeaturePython)
  n = 3
  ref = Ge_element
FEATURE [App::DocumentObjectGroupPython] O_element012  label="O_element : 12"  # scripted group (container) (typed FeaturePython)
  n = 12
  ref = O_element
FEATURE [App::DocumentObjectGroupPython] G4_BGO  # scripted group (container) (typed FeaturePython)
  Dunit = g/cm3
  Dvalue = 7.13
  Group = -> [Bi_element001,Ge_element001,O_element012]
  conduct = 2
  density = 1
  expand = 3
  formula = G4_BGO
  name = G4_BGO
  specific = 4
FEATURE [App::DocumentObjectGroupPython] H_element014  label="H_element : 0.102"  # scripted group (container) (typed FeaturePython)
  n = 0.102
FEATURE [App::DocumentObjectGroupPython] C_element014  label="C_element : 0.110"  # scripted group (container) (typed FeaturePython)
  n = 0.11
FEATURE [App::DocumentObjectGroupPython] N_element009  label="N_element : 0.033"  # scripted group (container) (typed FeaturePython)
  n = 0.033
FEATURE [App::DocumentObjectGroupPython] O_element013  label="O_element : 0.745"  # scripted group (container) (typed FeaturePython)
  n = 0.745
FEATURE [App::DocumentObjectGroupPython] Na_element002  label="Na_element : 0.002"  # scripted group (container) (typed FeaturePython)
  n = 0.001
FEATURE [App::DocumentObjectGroupPython] P_element001  label="P_element : 0.001"  # scripted group (container) (typed FeaturePython)
  n = 0.001
FEATURE [App::DocumentObjectGroupPython] S_element003  label="S_element : 0.002"  # scripted group (container) (typed FeaturePython)
  n = 0.002
FEATURE [App::DocumentObjectGroupPython] Cl_element002  label="Cl_element : 0.003"  # scripted group (container) (typed FeaturePython)
  n = 0.003
FEATURE [App::DocumentObjectGroupPython] K_element001  label="K_element : 0.002"  # scripted group (container) (typed FeaturePython)
  n = 0.002
FEATURE [App::DocumentObjectGroupPython] Fe_element001  label="Fe_element : 0.001"  # scripted group (container) (typed FeaturePython)
  n = 0.001
FEATURE [App::DocumentObjectGroupPython] G4_BLOOD_ICRP  # scripted group (container) (typed FeaturePython)
  Dunit = g/cm3
  Dvalue = 1.06
  Group = -> [H_element014,C_element014,N_element009,O_element013,Na_element002,P_element001,S_element003,Cl_element002,K_element001,Fe_element001]
  conduct = 2
  density = 1
  expand = 3
  formula = G4_BLOOD_ICRP
  name = G4_BLOOD_ICRP
  specific = 4
FEATURE [App::DocumentObjectGroupPython] H_element015  label="H_element : 0.064"  # scripted group (container) (typed FeaturePython)
  n = 0.064
FEATURE [App::DocumentObjectGroupPython] C_element015  label="C_element : 0.278"  # scripted group (container) (typed FeaturePython)
  n = 0.278
FEATURE [App::DocumentObjectGroupPython] N_element010  label="N_element : 0.027"  # scripted group (container) (typed FeaturePython)
  n = 0.027
FEATURE [App::DocumentObjectGroupPython] O_element014  label="O_element : 0.410"  # scripted group (container) (typed FeaturePython)
  n = 0.41
FEATURE [App::DocumentObjectGroupPython] Mg_element001  label="Mg_element : 0.002"  # scripted group (container) (typed FeaturePython)
  n = 0.002
FEATURE [App::DocumentObjectGroupPython] P_element002  label="P_element : 0.070"  # scripted group (container) (typed FeaturePython)
  n = 0.07
FEATURE [App::DocumentObjectGroupPython] S_element004  label="S_element : 0.003"  # scripted group (container) (typed FeaturePython)
  n = 0.002
FEATURE [App::DocumentObjectGroupPython] Ca_element003  label="Ca_element : 0.147"  # scripted group (container) (typed FeaturePython)
  n = 0.147
FEATURE [App::DocumentObjectGroupPython] G4_BONE_COMPACT_ICRU  # scripted group (container) (typed FeaturePython)
  Dunit = g/cm3
  Dvalue = 1.85
  Group = -> [H_element015,C_element015,N_element010,O_element014,Mg_element001,P_element002,S_element004,Ca_element003]
  conduct = 2
  density = 1
  expand = 3
  formula = G4_BONE_COMPACT_ICRU
  name = G4_BONE_COMPACT_ICRU
  specific = 4
FEATURE [App::DocumentObjectGroupPython] H_element016  label="H_element : 0.034"  # scripted group (container) (typed FeaturePython)
  n = 0.034
FEATURE [App::DocumentObjectGroupPython] C_element016  label="C_element : 0.155"  # scripted group (container) (typed FeaturePython)
  n = 0.155
FEATURE [App::DocumentObjectGroupPython] N_element011  label="N_element : 0.042"  # scripted group (container) (typed FeaturePython)
  n = 0.042
FEATURE [App::DocumentObjectGroupPython] O_element015  label="O_element : 0.435"  # scripted group (container) (typed FeaturePython)
  n = 0.435
FEATURE [App::DocumentObjectGroupPython] Na_element003  label="Na_element : 0.003"  # scripted group (container) (typed FeaturePython)
  n = 0.001
FEATURE [App::DocumentObjectGroupPython] Mg_element002  label="Mg_element : 0.003"  # scripted group (container) (typed FeaturePython)
  n = 0.002
FEATURE [App::DocumentObjectGroupPython] P_element003  label="P_element : 0.103"  # scripted group (container) (typed FeaturePython)
  n = 0.103
FEATURE [App::DocumentObjectGroupPython] S_element005  label="S_element : 0.004"  # scripted group (container) (typed FeaturePython)
  n = 0.003
FEATURE [App::DocumentObjectGroupPython] Ca_element004  label="Ca_element : 0.225"  # scripted group (container) (typed FeaturePython)
  n = 0.225
FEATURE [App::DocumentObjectGroupPython] G4_BONE_CORTICAL_ICRP  # scripted group (container) (typed FeaturePython)
  Dunit = g/cm3
  Dvalue = 1.92
  Group = -> [H_element016,C_element016,N_element011,O_element015,Na_element003,Mg_element002,P_element003,S_element005,Ca_element004]
  conduct = 2
  density = 1
  expand = 3
  formula = G4_BONE_CORTICAL_ICRP
  name = G4_BONE_CORTICAL_ICRP
  specific = 4
FEATURE [App::DocumentObjectGroupPython] B_element001  label="B_element : 4"  # scripted group (container) (typed FeaturePython)
  n = 4
  ref = B_element
FEATURE [App::DocumentObjectGroupPython] C_element017  label="C_element : 1"  # scripted group (container) (typed FeaturePython)
  n = 1
  ref = C_element
FEATURE [App::DocumentObjectGroupPython] G4_BORON_CARBIDE  # scripted group (container) (typed FeaturePython)
  Dunit = g/cm3
  Dvalue = 2.52
  Group = -> [B_element001,C_element017]
  conduct = 2
  density = 1
  expand = 3
  formula = G4_BORON_CARBIDE
  name = G4_BORON_CARBIDE
  specific = 4
FEATURE [App::DocumentObjectGroupPython] B_element002  label="B_element : 2"  # scripted group (container) (typed FeaturePython)
  n = 2
  ref = B_element
FEATURE [App::DocumentObjectGroupPython] O_element016  label="O_element : 006"  # scripted group (container) (typed FeaturePython)
  n = 3
  ref = O_element
FEATURE [App::DocumentObjectGroupPython] G4_BORON_OXIDE  # scripted group (container) (typed FeaturePython)
  Dunit = g/cm3
  Dvalue = 1.812
  Group = -> [B_element002,O_element016]
  conduct = 2
  density = 1
  expand = 3
  formula = G4_BORON_OXIDE
  name = G4_BORON_OXIDE
  specific = 4
FEATURE [App::DocumentObjectGroupPython] H_element017  label="H_element : 0.107"  # scripted group (container) (typed FeaturePython)
  n = 0.107
FEATURE [App::DocumentObjectGroupPython] C_element018  label="C_element : 0.145"  # scripted group (container) (typed FeaturePython)
  n = 0.145
FEATURE [App::DocumentObjectGroupPython] N_element012  label="N_element : 0.022"  # scripted group (container) (typed FeaturePython)
  n = 0.022
FEATURE [App::DocumentObjectGroupPython] O_element017  label="O_element : 0.712"  # scripted group (container) (typed FeaturePython)
  n = 0.712
FEATURE [App::DocumentObjectGroupPython] Na_element004  label="Na_element : 0.004"  # scripted group (container) (typed FeaturePython)
  n = 0.002
FEATURE [App::DocumentObjectGroupPython] P_element004  label="P_element : 0.004"  # scripted group (container) (typed FeaturePython)
  n = 0.004
FEATURE [App::DocumentObjectGroupPython] S_element006  label="S_element : 0.005"  # scripted group (container) (typed FeaturePython)
  n = 0.002
FEATURE [App::DocumentObjectGroupPython] Cl_element003  label="Cl_element : 0.004"  # scripted group (container) (typed FeaturePython)
  n = 0.003
FEATURE [App::DocumentObjectGroupPython] K_element002  label="K_element : 0.003"  # scripted group (container) (typed FeaturePython)
  n = 0.003
FEATURE [App::DocumentObjectGroupPython] G4_BRAIN_ICRP  # scripted group (container) (typed FeaturePython)
  Dunit = g/cm3
  Dvalue = 1.04
  Group = -> [H_element017,C_element018,N_element012,O_element017,Na_element004,P_element004,S_element006,Cl_element003,K_element002]
  conduct = 2
  density = 1
  expand = 3
  formula = G4_BRAIN_ICRP
  name = G4_BRAIN_ICRP
  specific = 4
FEATURE [App::DocumentObjectGroupPython] C_element019  label="C_element : 4"  # scripted group (container) (typed FeaturePython)
  n = 4
  ref = C_element
FEATURE [App::DocumentObjectGroupPython] H_element018  label="H_element : 010"  # scripted group (container) (typed FeaturePython)
  n = 10
  ref = H_element
FEATURE [App::DocumentObjectGroupPython] G4_BUTANE  # scripted group (container) (typed FeaturePython)
  Dunit = g/cm3
  Dvalue = 0.00249343
  Group = -> [C_element019,H_element018]
  conduct = 2
  density = 1
  expand = 3
  formula = G4_BUTANE
  name = G4_BUTANE
  specific = 4
FEATURE [App::DocumentObjectGroupPython] C_element020  label="C_element : 008"  # scripted group (container) (typed FeaturePython)
  n = 4
  ref = C_element
FEATURE [App::DocumentObjectGroupPython] H_element019  label="H_element : 011"  # scripted group (container) (typed FeaturePython)
  n = 10
  ref = H_element
FEATURE [App::DocumentObjectGroupPython] O_element018  label="O_element : 007"  # scripted group (container) (typed FeaturePython)
  n = 1
  ref = O_element
FEATURE [App::DocumentObjectGroupPython] G4_N_BUTYL_ALCOHOL  label="G4_N-BUTYL_ALCOHOL"  # scripted group (container) (typed FeaturePython)
  Dunit = g/cm3
  Dvalue = 0.8098
  Group = -> [C_element020,H_element019,O_element018]
  conduct = 2
  density = 1
  expand = 3
  formula = G4_N-BUTYL_ALCOHOL
  name = G4_N-BUTYL_ALCOHOL
  specific = 4
FEATURE [App::DocumentObjectGroupPython] H_element020  label="H_element : 0.025"  # scripted group (container) (typed FeaturePython)
  n = 0.02468
FEATURE [App::DocumentObjectGroupPython] C_element021  label="C_element : 0.502"  # scripted group (container) (typed FeaturePython)
  n = 0.501611
FEATURE [App::DocumentObjectGroupPython] O_element019  label="O_element : 0.005"  # scripted group (container) (typed FeaturePython)
  n = 0.004527
FEATURE [App::DocumentObjectGroupPython] F_element004  label="F_element : 0.465"  # scripted group (container) (typed FeaturePython)
  n = 0.465209
FEATURE [App::DocumentObjectGroupPython] Si_element001  label="Si_element : 0.004"  # scripted group (container) (typed FeaturePython)
  n = 0.003973
FEATURE [App::DocumentObjectGroupPython] G4_C_552  label="G4_C-552"  # scripted group (container) (typed FeaturePython)
  Dunit = g/cm3
  Dvalue = 1.76
  Group = -> [H_element020,C_element021,O_element019,F_element004,Si_element001]
  conduct = 2
  density = 1
  expand = 3
  formula = G4_C-552
  name = G4_C-552
  specific = 4
FEATURE [App::DocumentObjectGroupPython] Cd_element001  label="Cd_element : 1"  # scripted group (container) (typed FeaturePython)
  n = 1
  ref = Cd_element
FEATURE [App::DocumentObjectGroupPython] Te_element001  label="Te_element : 1"  # scripted group (container) (typed FeaturePython)
  n = 1
  ref = Te_element
FEATURE [App::DocumentObjectGroupPython] G4_CADMIUM_TELLURIDE  # scripted group (container) (typed FeaturePython)
  Dunit = g/cm3
  Dvalue = 6.2
  Group = -> [Cd_element001,Te_element001]
  conduct = 2
  density = 1
  expand = 3
  formula = G4_CADMIUM_TELLURIDE
  name = G4_CADMIUM_TELLURIDE
  specific = 4
FEATURE [App::DocumentObjectGroupPython] Cd_element002  label="Cd_element : 002"  # scripted group (container) (typed FeaturePython)
  n = 1
  ref = Cd_element
FEATURE [App::DocumentObjectGroupPython] W_element001  label="W_element : 1"  # scripted group (container) (typed FeaturePython)
  n = 1
  ref = W_element
FEATURE [App::DocumentObjectGroupPython] O_element020  label="O_element : 008"  # scripted group (container) (typed FeaturePython)
  n = 4
  ref = O_element
FEATURE [App::DocumentObjectGroupPython] G4_CADMIUM_TUNGSTATE  # scripted group (container) (typed FeaturePython)
  Dunit = g/cm3
  Dvalue = 7.9
  Group = -> [Cd_element002,W_element001,O_element020]
  conduct = 2
  density = 1
  expand = 3
  formula = G4_CADMIUM_TUNGSTATE
  name = G4_CADMIUM_TUNGSTATE
  specific = 4
FEATURE [App::DocumentObjectGroupPython] Ca_element005  label="Ca_element : 1"  # scripted group (container) (typed FeaturePython)
  n = 1
  ref = Ca_element
FEATURE [App::DocumentObjectGroupPython] C_element022  label="C_element : 009"  # scripted group (container) (typed FeaturePython)
  n = 1
  ref = C_element
FEATURE [App::DocumentObjectGroupPython] O_element021  label="O_element : 009"  # scripted group (container) (typed FeaturePython)
  n = 3
  ref = O_element
FEATURE [App::DocumentObjectGroupPython] G4_CALCIUM_CARBONATE  # scripted group (container) (typed FeaturePython)
  Dunit = g/cm3
  Dvalue = 2.8
  Group = -> [Ca_element005,C_element022,O_element021]
  conduct = 2
  density = 1
  expand = 3
  formula = G4_CALCIUM_CARBONATE
  name = G4_CALCIUM_CARBONATE
  specific = 4
FEATURE [App::DocumentObjectGroupPython] Ca_element006  label="Ca_element : 002"  # scripted group (container) (typed FeaturePython)
  n = 1
  ref = Ca_element
FEATURE [App::DocumentObjectGroupPython] F_element005  label="F_element : 003"  # scripted group (container) (typed FeaturePython)
  n = 2
  ref = F_element
FEATURE [App::DocumentObjectGroupPython] G4_CALCIUM_FLUORIDE  # scripted group (container) (typed FeaturePython)
  Dunit = g/cm3
  Dvalue = 3.18
  Group = -> [Ca_element006,F_element005]
  conduct = 2
  density = 1
  expand = 3
  formula = G4_CALCIUM_FLUORIDE
  name = G4_CALCIUM_FLUORIDE
  specific = 4
FEATURE [App::DocumentObjectGroupPython] Ca_element007  label="Ca_element : 003"  # scripted group (container) (typed FeaturePython)
  n = 1
  ref = Ca_element
FEATURE [App::DocumentObjectGroupPython] O_element022  label="O_element : 010"  # scripted group (container) (typed FeaturePython)
  n = 1
  ref = O_element
FEATURE [App::DocumentObjectGroupPython] G4_CALCIUM_OXIDE  # scripted group (container) (typed FeaturePython)
  Dunit = g/cm3
  Dvalue = 3.3
  Group = -> [Ca_element007,O_element022]
  conduct = 2
  density = 1
  expand = 3
  formula = G4_CALCIUM_OXIDE
  name = G4_CALCIUM_OXIDE
  specific = 4
FEATURE [App::DocumentObjectGroupPython] Ca_element008  label="Ca_element : 004"  # scripted group (container) (typed FeaturePython)
  n = 1
  ref = Ca_element
FEATURE [App::DocumentObjectGroupPython] S_element007  label="S_element : 002"  # scripted group (container) (typed FeaturePython)
  n = 1
  ref = S_element
FEATURE [App::DocumentObjectGroupPython] O_element023  label="O_element : 011"  # scripted group (container) (typed FeaturePython)
  n = 4
  ref = O_element
FEATURE [App::DocumentObjectGroupPython] G4_CALCIUM_SULFATE  # scripted group (container) (typed FeaturePython)
  Dunit = g/cm3
  Dvalue = 2.96
  Group = -> [Ca_element008,S_element007,O_element023]
  conduct = 2
  density = 1
  expand = 3
  formula = G4_CALCIUM_SULFATE
  name = G4_CALCIUM_SULFATE
  specific = 4
FEATURE [App::DocumentObjectGroupPython] Ca_element009  label="Ca_element : 005"  # scripted group (container) (typed FeaturePython)
  n = 1
  ref = Ca_element
FEATURE [App::DocumentObjectGroupPython] W_element002  label="W_element : 002"  # scripted group (container) (typed FeaturePython)
  n = 1
  ref = W_element
FEATURE [App::DocumentObjectGroupPython] O_element024  label="O_element : 012"  # scripted group (container) (typed FeaturePython)
  n = 4
  ref = O_element
FEATURE [App::DocumentObjectGroupPython] G4_CALCIUM_TUNGSTATE  # scripted group (container) (typed FeaturePython)
  Dunit = g/cm3
  Dvalue = 6.062
  Group = -> [Ca_element009,W_element002,O_element024]
  conduct = 2
  density = 1
  expand = 3
  formula = G4_CALCIUM_TUNGSTATE
  name = G4_CALCIUM_TUNGSTATE
  specific = 4
FEATURE [App::DocumentObjectGroupPython] C_element023  label="C_element : 010"  # scripted group (container) (typed FeaturePython)
  n = 1
  ref = C_element
FEATURE [App::DocumentObjectGroupPython] O_element025  label="O_element : 013"  # scripted group (container) (typed FeaturePython)
  n = 2
  ref = O_element
FEATURE [App::DocumentObjectGroupPython] G4_CARBON_DIOXIDE  # scripted group (container) (typed FeaturePython)
  Dunit = g/cm3
  Dvalue = 0.00184212
  Group = -> [C_element023,O_element025]
  conduct = 2
  density = 1
  expand = 3
  formula = G4_CARBON_DIOXIDE
  name = G4_CARBON_DIOXIDE
  specific = 4
FEATURE [App::DocumentObjectGroupPython] C_element024  label="C_element : 011"  # scripted group (container) (typed FeaturePython)
  n = 1
  ref = C_element
FEATURE [App::DocumentObjectGroupPython] Cl_element004  label="Cl_element : 4"  # scripted group (container) (typed FeaturePython)
  n = 4
  ref = Cl_element
FEATURE [App::DocumentObjectGroupPython] G4_CARBON_TETRACHLORIDE  # scripted group (container) (typed FeaturePython)
  Dunit = g/cm3
  Dvalue = 1.594
  Group = -> [C_element024,Cl_element004]
  conduct = 2
  density = 1
  expand = 3
  formula = G4_CARBON_TETRACHLORIDE
  name = G4_CARBON_TETRACHLORIDE
  specific = 4
FEATURE [App::DocumentObjectGroupPython] C_element025  label="C_element : 012"  # scripted group (container) (typed FeaturePython)
  n = 6
  ref = C_element
FEATURE [App::DocumentObjectGroupPython] H_element021  label="H_element : 012"  # scripted group (container) (typed FeaturePython)
  n = 10
  ref = H_element
FEATURE [App::DocumentObjectGroupPython] O_element026  label="O_element : 5"  # scripted group (container) (typed FeaturePython)
  n = 5
  ref = O_element
FEATURE [App::DocumentObjectGroupPython] G4_CELLULOSE_CELLOPHANE  # scripted group (container) (typed FeaturePython)
  Dunit = g/cm3
  Dvalue = 1.42
  Group = -> [C_element025,H_element021,O_element026]
  conduct = 2
  density = 1
  expand = 3
  formula = G4_CELLULOSE_CELLOPHANE
  name = G4_CELLULOSE_CELLOPHANE
  specific = 4
FEATURE [App::DocumentObjectGroupPython] H_element022  label="H_element : 0.067"  # scripted group (container) (typed FeaturePython)
  n = 0.067125
FEATURE [App::DocumentObjectGroupPython] C_element026  label="C_element : 0.545"  # scripted group (container) (typed FeaturePython)
  n = 0.545403
FEATURE [App::DocumentObjectGroupPython] O_element027  label="O_element : 0.387"  # scripted group (container) (typed FeaturePython)
  n = 0.387472
FEATURE [App::DocumentObjectGroupPython] G4_CELLULOSE_BUTYRATE  # scripted group (container) (typed FeaturePython)
  Dunit = g/cm3
  Dvalue = 1.2
  Group = -> [H_element022,C_element026,O_element027]
  conduct = 2
  density = 1
  expand = 3
  formula = G4_CELLULOSE_BUTYRATE
  name = G4_CELLULOSE_BUTYRATE
  specific = 4
FEATURE [App::DocumentObjectGroupPython] H_element023  label="H_element : 0.029"  # scripted group (container) (typed FeaturePython)
  n = 0.029216
FEATURE [App::DocumentObjectGroupPython] C_element027  label="C_element : 0.271"  # scripted group (container) (typed FeaturePython)
  n = 0.271296
FEATURE [App::DocumentObjectGroupPython] N_element013  label="N_element : 0.121"  # scripted group (container) (typed FeaturePython)
  n = 0.121276
FEATURE [App::DocumentObjectGroupPython] O_element028  label="O_element : 0.578"  # scripted group (container) (typed FeaturePython)
  n = 0.578212
FEATURE [App::DocumentObjectGroupPython] G4_CELLULOSE_NITRATE  # scripted group (container) (typed FeaturePython)
  Dunit = g/cm3
  Dvalue = 1.49
  Group = -> [H_element023,C_element027,N_element013,O_element028]
  conduct = 2
  density = 1
  expand = 3
  formula = G4_CELLULOSE_NITRATE
  name = G4_CELLULOSE_NITRATE
  specific = 4
FEATURE [App::DocumentObjectGroupPython] H_element024  label="H_element : 0.108"  # scripted group (container) (typed FeaturePython)
  n = 0.107596
FEATURE [App::DocumentObjectGroupPython] N_element014  label="N_element : 0.001"  # scripted group (container) (typed FeaturePython)
  n = 0.0008
FEATURE [App::DocumentObjectGroupPython] O_element029  label="O_element : 0.875"  # scripted group (container) (typed FeaturePython)
  n = 0.874976
FEATURE [App::DocumentObjectGroupPython] S_element008  label="S_element : 0.015"  # scripted group (container) (typed FeaturePython)
  n = 0.014627
FEATURE [App::DocumentObjectGroupPython] Ce_element001  label="Ce_element : 0.002"  # scripted group (container) (typed FeaturePython)
  n = 0.002001
FEATURE [App::DocumentObjectGroupPython] G4_CERIC_SULFATE  # scripted group (container) (typed FeaturePython)
  Dunit = g/cm3
  Dvalue = 1.03
  Group = -> [H_element024,N_element014,O_element029,S_element008,Ce_element001]
  conduct = 2
  density = 1
  expand = 3
  formula = G4_CERIC_SULFATE
  name = G4_CERIC_SULFATE
  specific = 4
FEATURE [App::DocumentObjectGroupPython] Cs_element001  label="Cs_element : 1"  # scripted group (container) (typed FeaturePython)
  n = 1
  ref = Cs_element
FEATURE [App::DocumentObjectGroupPython] F_element006  label="F_element : 1"  # scripted group (container) (typed FeaturePython)
  n = 1
  ref = F_element
FEATURE [App::DocumentObjectGroupPython] G4_CESIUM_FLUORIDE  # scripted group (container) (typed FeaturePython)
  Dunit = g/cm3
  Dvalue = 4.115
  Group = -> [Cs_element001,F_element006]
  conduct = 2
  density = 1
  expand = 3
  formula = G4_CESIUM_FLUORIDE
  name = G4_CESIUM_FLUORIDE
  specific = 4
FEATURE [App::DocumentObjectGroupPython] Cs_element002  label="Cs_element : 002"  # scripted group (container) (typed FeaturePython)
  n = 1
  ref = Cs_element
FEATURE [App::DocumentObjectGroupPython] I_element001  label="I_element : 1"  # scripted group (container) (typed FeaturePython)
  n = 1
  ref = I_element
FEATURE [App::DocumentObjectGroupPython] G4_CESIUM_IODIDE  # scripted group (container) (typed FeaturePython)
  Dunit = g/cm3
  Dvalue = 4.51
  Group = -> [Cs_element002,I_element001]
  conduct = 2
  density = 1
  expand = 3
  formula = G4_CESIUM_IODIDE
  name = G4_CESIUM_IODIDE
  specific = 4
FEATURE [App::DocumentObjectGroupPython] C_element028  label="C_element : 013"  # scripted group (container) (typed FeaturePython)
  n = 6
  ref = C_element
FEATURE [App::DocumentObjectGroupPython] H_element025  label="H_element : 013"  # scripted group (container) (typed FeaturePython)
  n = 5
  ref = H_element
FEATURE [App::DocumentObjectGroupPython] Cl_element005  label="Cl_element : 1"  # scripted group (container) (typed FeaturePython)
  n = 1
  ref = Cl_element
FEATURE [App::DocumentObjectGroupPython] G4_CHLOROBENZENE  # scripted group (container) (typed FeaturePython)
  Dunit = g/cm3
  Dvalue = 1.1058
  Group = -> [C_element028,H_element025,Cl_element005]
  conduct = 2
  density = 1
  expand = 3
  formula = G4_CHLOROBENZENE
  name = G4_CHLOROBENZENE
  specific = 4
FEATURE [App::DocumentObjectGroupPython] C_element029  label="C_element : 014"  # scripted group (container) (typed FeaturePython)
  n = 1
  ref = C_element
FEATURE [App::DocumentObjectGroupPython] H_element026  label="H_element : 1"  # scripted group (container) (typed FeaturePython)
  n = 1
  ref = H_element
FEATURE [App::DocumentObjectGroupPython] Cl_element006  label="Cl_element : 3"  # scripted group (container) (typed FeaturePython)
  n = 3
  ref = Cl_element
FEATURE [App::DocumentObjectGroupPython] G4_CHLOROFORM  # scripted group (container) (typed FeaturePython)
  Dunit = g/cm3
  Dvalue = 1.4832
  Group = -> [C_element029,H_element026,Cl_element006]
  conduct = 2
  density = 1
  expand = 3
  formula = G4_CHLOROFORM
  name = G4_CHLOROFORM
  specific = 4
FEATURE [App::DocumentObjectGroupPython] H_element027  label="H_element : 0.010"  # scripted group (container) (typed FeaturePython)
  n = 0.01
FEATURE [App::DocumentObjectGroupPython] C_element030  label="C_element : 0.001"  # scripted group (container) (typed FeaturePython)
  n = 0.001
FEATURE [App::DocumentObjectGroupPython] O_element030  label="O_element : 0.529"  # scripted group (container) (typed FeaturePython)
  n = 0.529107
FEATURE [App::DocumentObjectGroupPython] Na_element005  label="Na_element : 0.016"  # scripted group (container) (typed FeaturePython)
  n = 0.016
FEATURE [App::DocumentObjectGroupPython] Mg_element003  label="Mg_element : 0.004"  # scripted group (container) (typed FeaturePython)
  n = 0.002
FEATURE [App::DocumentObjectGroupPython] Al_element002  label="Al_element : 0.034"  # scripted group (container) (typed FeaturePython)
  n = 0.033872
FEATURE [App::DocumentObjectGroupPython] Si_element002  label="Si_element : 0.337"  # scripted group (container) (typed FeaturePython)
  n = 0.337021
FEATURE [App::DocumentObjectGroupPython] K_element003  label="K_element : 0.013"  # scripted group (container) (typed FeaturePython)
  n = 0.013
FEATURE [App::DocumentObjectGroupPython] Ca_element010  label="Ca_element : 0.044"  # scripted group (container) (typed FeaturePython)
  n = 0.044
FEATURE [App::DocumentObjectGroupPython] Fe_element002  label="Fe_element : 0.014"  # scripted group (container) (typed FeaturePython)
  n = 0.014
FEATURE [App::DocumentObjectGroupPython] G4_CONCRETE  # scripted group (container) (typed FeaturePython)
  Dunit = g/cm3
  Dvalue = 2.3
  Group = -> [H_element027,C_element030,O_element030,Na_element005,Mg_element003,Al_element002,Si_element002,K_element003,Ca_element010,Fe_element002]
  conduct = 2
  density = 1
  expand = 3
  formula = G4_CONCRETE
  name = G4_CONCRETE
  specific = 4
FEATURE [App::DocumentObjectGroupPython] C_element031  label="C_element : 015"  # scripted group (container) (typed FeaturePython)
  n = 6
  ref = C_element
FEATURE [App::DocumentObjectGroupPython] H_element028  label="H_element : 12"  # scripted group (container) (typed FeaturePython)
  n = 12
  ref = H_element
FEATURE [App::DocumentObjectGroupPython] G4_CYCLOHEXANE  # scripted group (container) (typed FeaturePython)
  Dunit = g/cm3
  Dvalue = 0.779
  Group = -> [C_element031,H_element028]
  conduct = 2
  density = 1
  expand = 3
  formula = G4_CYCLOHEXANE
  name = G4_CYCLOHEXANE
  specific = 4
FEATURE [App::DocumentObjectGroupPython] C_element032  label="C_element : 016"  # scripted group (container) (typed FeaturePython)
  n = 6
  ref = C_element
FEATURE [App::DocumentObjectGroupPython] H_element029  label="H_element : 4"  # scripted group (container) (typed FeaturePython)
  n = 4
  ref = H_element
FEATURE [App::DocumentObjectGroupPython] Cl_element007  label="Cl_element : 2"  # scripted group (container) (typed FeaturePython)
  n = 2
  ref = Cl_element
FEATURE [App::DocumentObjectGroupPython] G4_1_2_DICHLOROBENZENE  label="G4_1.2-DICHLOROBENZENE"  # scripted group (container) (typed FeaturePython)
  Dunit = g/cm3
  Dvalue = 1.3048
  Group = -> [C_element032,H_element029,Cl_element007]
  conduct = 2
  density = 1
  expand = 3
  formula = G4_1.2-DICHLOROBENZENE
  name = G4_1.2-DICHLOROBENZENE
  specific = 4
FEATURE [App::DocumentObjectGroupPython] C_element033  label="C_element : 017"  # scripted group (container) (typed FeaturePython)
  n = 4
  ref = C_element
FEATURE [App::DocumentObjectGroupPython] H_element030  label="H_element : 8"  # scripted group (container) (typed FeaturePython)
  n = 8
  ref = H_element
FEATURE [App::DocumentObjectGroupPython] O_element031  label="O_element : 014"  # scripted group (container) (typed FeaturePython)
  n = 1
  ref = O_element
FEATURE [App::DocumentObjectGroupPython] Cl_element008  label="Cl_element : 005"  # scripted group (container) (typed FeaturePython)
  n = 2
  ref = Cl_element
FEATURE [App::DocumentObjectGroupPython] G4_DICHLORODIETHYL_ETHER  # scripted group (container) (typed FeaturePython)
  Dunit = g/cm3
  Dvalue = 1.2199
  Group = -> [C_element033,H_element030,O_element031,Cl_element008]
  conduct = 2
  density = 1
  expand = 3
  formula = G4_DICHLORODIETHYL_ETHER
  name = G4_DICHLORODIETHYL_ETHER
  specific = 4
FEATURE [App::DocumentObjectGroupPython] C_element034  label="C_element : 018"  # scripted group (container) (typed FeaturePython)
  n = 2
  ref = C_element
FEATURE [App::DocumentObjectGroupPython] H_element031  label="H_element : 014"  # scripted group (container) (typed FeaturePython)
  n = 4
  ref = H_element
FEATURE [App::DocumentObjectGroupPython] Cl_element009  label="Cl_element : 006"  # scripted group (container) (typed FeaturePython)
  n = 2
  ref = Cl_element
FEATURE [App::DocumentObjectGroupPython] G4_1_2_DICHLOROETHANE  label="G4_1.2-DICHLOROETHANE"  # scripted group (container) (typed FeaturePython)
  Dunit = g/cm3
  Dvalue = 1.2351
  Group = -> [C_element034,H_element031,Cl_element009]
  conduct = 2
  density = 1
  expand = 3
  formula = G4_1.2-DICHLOROETHANE
  name = G4_1.2-DICHLOROETHANE
  specific = 4
FEATURE [App::DocumentObjectGroupPython] C_element035  label="C_element : 019"  # scripted group (container) (typed FeaturePython)
  n = 4
  ref = C_element
FEATURE [App::DocumentObjectGroupPython] H_element032  label="H_element : 015"  # scripted group (container) (typed FeaturePython)
  n = 10
  ref = H_element
FEATURE [App::DocumentObjectGroupPython] O_element032  label="O_element : 015"  # scripted group (container) (typed FeaturePython)
  n = 1
  ref = O_element
FEATURE [App::DocumentObjectGroupPython] G4_DIETHYL_ETHER  # scripted group (container) (typed FeaturePython)
  Dunit = g/cm3
  Dvalue = 0.71378
  Group = -> [C_element035,H_element032,O_element032]
  conduct = 2
  density = 1
  expand = 3
  formula = G4_DIETHYL_ETHER
  name = G4_DIETHYL_ETHER
  specific = 4
FEATURE [App::DocumentObjectGroupPython] C_element036  label="C_element : 020"  # scripted group (container) (typed FeaturePython)
  n = 3
  ref = C_element
FEATURE [App::DocumentObjectGroupPython] H_element033  label="H_element : 016"  # scripted group (container) (typed FeaturePython)
  n = 7
  ref = H_element
FEATURE [App::DocumentObjectGroupPython] N_element015  label="N_element : 008"  # scripted group (container) (typed FeaturePython)
  n = 1
  ref = N_element
FEATURE [App::DocumentObjectGroupPython] O_element033  label="O_element : 016"  # scripted group (container) (typed FeaturePython)
  n = 1
  ref = O_element
FEATURE [App::DocumentObjectGroupPython] G4_N_N_DIMETHYL_FORMAMIDE  label="G4_N.N-DIMETHYL_FORMAMIDE"  # scripted group (container) (typed FeaturePython)
  Dunit = g/cm3
  Dvalue = 0.9487
  Group = -> [C_element036,H_element033,N_element015,O_element033]
  conduct = 2
  density = 1
  expand = 3
  formula = G4_N.N-DIMETHYL_FORMAMIDE
  name = G4_N.N-DIMETHYL_FORMAMIDE
  specific = 4
FEATURE [App::DocumentObjectGroupPython] C_element037  label="C_element : 021"  # scripted group (container) (typed FeaturePython)
  n = 2
  ref = C_element
FEATURE [App::DocumentObjectGroupPython] H_element034  label="H_element : 017"  # scripted group (container) (typed FeaturePython)
  n = 6
  ref = H_element
FEATURE [App::DocumentObjectGroupPython] O_element034  label="O_element : 017"  # scripted group (container) (typed FeaturePython)
  n = 1
  ref = O_element
FEATURE [App::DocumentObjectGroupPython] S_element009  label="S_element : 003"  # scripted group (container) (typed FeaturePython)
  n = 1
  ref = S_element
FEATURE [App::DocumentObjectGroupPython] G4_DIMETHYL_SULFOXIDE  # scripted group (container) (typed FeaturePython)
  Dunit = g/cm3
  Dvalue = 1.1014
  Group = -> [C_element037,H_element034,O_element034,S_element009]
  conduct = 2
  density = 1
  expand = 3
  formula = G4_DIMETHYL_SULFOXIDE
  name = G4_DIMETHYL_SULFOXIDE
  specific = 4
FEATURE [App::DocumentObjectGroupPython] C_element038  label="C_element : 022"  # scripted group (container) (typed FeaturePython)
  n = 2
  ref = C_element
FEATURE [App::DocumentObjectGroupPython] H_element035  label="H_element : 018"  # scripted group (container) (typed FeaturePython)
  n = 6
  ref = H_element
FEATURE [App::DocumentObjectGroupPython] G4_ETHANE  # scripted group (container) (typed FeaturePython)
  Dunit = g/cm3
  Dvalue = 0.00125324
  Group = -> [C_element038,H_element035]
  conduct = 2
  density = 1
  expand = 3
  formula = G4_ETHANE
  name = G4_ETHANE
  specific = 4
FEATURE [App::DocumentObjectGroupPython] C_element039  label="C_element : 023"  # scripted group (container) (typed FeaturePython)
  n = 2
  ref = C_element
FEATURE [App::DocumentObjectGroupPython] H_element036  label="H_element : 019"  # scripted group (container) (typed FeaturePython)
  n = 6
  ref = H_element
FEATURE [App::DocumentObjectGroupPython] O_element035  label="O_element : 018"  # scripted group (container) (typed FeaturePython)
  n = 1
  ref = O_element
FEATURE [App::DocumentObjectGroupPython] G4_ETHYL_ALCOHOL  # scripted group (container) (typed FeaturePython)
  Dunit = g/cm3
  Dvalue = 0.7893
  Group = -> [C_element039,H_element036,O_element035]
  conduct = 2
  density = 1
  expand = 3
  formula = G4_ETHYL_ALCOHOL
  name = G4_ETHYL_ALCOHOL
  specific = 4
FEATURE [App::DocumentObjectGroupPython] H_element037  label="H_element : 0.090"  # scripted group (container) (typed FeaturePython)
  n = 0.090027
FEATURE [App::DocumentObjectGroupPython] C_element040  label="C_element : 0.585"  # scripted group (container) (typed FeaturePython)
  n = 0.585182
FEATURE [App::DocumentObjectGroupPython] O_element036  label="O_element : 0.325"  # scripted group (container) (typed FeaturePython)
  n = 0.324791
FEATURE [App::DocumentObjectGroupPython] G4_ETHYL_CELLULOSE  # scripted group (container) (typed FeaturePython)
  Dunit = g/cm3
  Dvalue = 1.13
  Group = -> [H_element037,C_element040,O_element036]
  conduct = 2
  density = 1
  expand = 3
  formula = G4_ETHYL_CELLULOSE
  name = G4_ETHYL_CELLULOSE
  specific = 4
FEATURE [App::DocumentObjectGroupPython] C_element041  label="C_element : 024"  # scripted group (container) (typed FeaturePython)
  n = 2
  ref = C_element
FEATURE [App::DocumentObjectGroupPython] H_element038  label="H_element : 020"  # scripted group (container) (typed FeaturePython)
  n = 4
  ref = H_element
FEATURE [App::DocumentObjectGroupPython] G4_ETHYLENE  # scripted group (container) (typed FeaturePython)
  Dunit = g/cm3
  Dvalue = 0.00117497
  Group = -> [C_element041,H_element038]
  conduct = 2
  density = 1
  expand = 3
  formula = G4_ETHYLENE
  name = G4_ETHYLENE
  specific = 4
FEATURE [App::DocumentObjectGroupPython] H_element039  label="H_element : 0.096"  # scripted group (container) (typed FeaturePython)
  n = 0.096
FEATURE [App::DocumentObjectGroupPython] C_element042  label="C_element : 0.195"  # scripted group (container) (typed FeaturePython)
  n = 0.195
FEATURE [App::DocumentObjectGroupPython] N_element016  label="N_element : 0.057"  # scripted group (container) (typed FeaturePython)
  n = 0.057
FEATURE [App::DocumentObjectGroupPython] O_element037  label="O_element : 0.646"  # scripted group (container) (typed FeaturePython)
  n = 0.646
FEATURE [App::DocumentObjectGroupPython] Na_element006  label="Na_element : 0.017"  # scripted group (container) (typed FeaturePython)
  n = 0.001
FEATURE [App::DocumentObjectGroupPython] P_element005  label="P_element : 0.104"  # scripted group (container) (typed FeaturePython)
  n = 0.001
FEATURE [App::DocumentObjectGroupPython] S_element010  label="S_element : 0.016"  # scripted group (container) (typed FeaturePython)
  n = 0.003
FEATURE [App::DocumentObjectGroupPython] Cl_element010  label="Cl_element : 0.005"  # scripted group (container) (typed FeaturePython)
  n = 0.001
FEATURE [App::DocumentObjectGroupPython] G4_EYE_LENS_ICRP  # scripted group (container) (typed FeaturePython)
  Dunit = g/cm3
  Dvalue = 1.07
  Group = -> [H_element039,C_element042,N_element016,O_element037,Na_element006,P_element005,S_element010,Cl_element010]
  conduct = 2
  density = 1
  expand = 3
  formula = G4_EYE_LENS_ICRP
  name = G4_EYE_LENS_ICRP
  specific = 4
FEATURE [App::DocumentObjectGroupPython] Fe_element003  label="Fe_element : 2"  # scripted group (container) (typed FeaturePython)
  n = 2
  ref = Fe_element
FEATURE [App::DocumentObjectGroupPython] O_element038  label="O_element : 019"  # scripted group (container) (typed FeaturePython)
  n = 3
  ref = O_element
FEATURE [App::DocumentObjectGroupPython] G4_FERRIC_OXIDE  # scripted group (container) (typed FeaturePython)
  Dunit = g/cm3
  Dvalue = 5.2
  Group = -> [Fe_element003,O_element038]
  conduct = 2
  density = 1
  expand = 3
  formula = G4_FERRIC_OXIDE
  name = G4_FERRIC_OXIDE
  specific = 4
FEATURE [App::DocumentObjectGroupPython] Fe_element004  label="Fe_element : 1"  # scripted group (container) (typed FeaturePython)
  n = 1
  ref = Fe_element
FEATURE [App::DocumentObjectGroupPython] B_element003  label="B_element : 1"  # scripted group (container) (typed FeaturePython)
  n = 1
  ref = B_element
FEATURE [App::DocumentObjectGroupPython] G4_FERROBORIDE  # scripted group (container) (typed FeaturePython)
  Dunit = g/cm3
  Dvalue = 7.15
  Group = -> [Fe_element004,B_element003]
  conduct = 2
  density = 1
  expand = 3
  formula = G4_FERROBORIDE
  name = G4_FERROBORIDE
  specific = 4
FEATURE [App::DocumentObjectGroupPython] Fe_element005  label="Fe_element : 003"  # scripted group (container) (typed FeaturePython)
  n = 1
  ref = Fe_element
FEATURE [App::DocumentObjectGroupPython] O_element039  label="O_element : 020"  # scripted group (container) (typed FeaturePython)
  n = 1
  ref = O_element
FEATURE [App::DocumentObjectGroupPython] G4_FERROUS_OXIDE  # scripted group (container) (typed FeaturePython)
  Dunit = g/cm3
  Dvalue = 5.7
  Group = -> [Fe_element005,O_element039]
  conduct = 2
  density = 1
  expand = 3
  formula = G4_FERROUS_OXIDE
  name = G4_FERROUS_OXIDE
  specific = 4
FEATURE [App::DocumentObjectGroupPython] H_element040  label="H_element : 0.115"  # scripted group (container) (typed FeaturePython)
  n = 0.108259
FEATURE [App::DocumentObjectGroupPython] N_element017  label="N_element : 0.000"  # scripted group (container) (typed FeaturePython)
  n = 2.7e-05
FEATURE [App::DocumentObjectGroupPython] O_element040  label="O_element : 0.879"  # scripted group (container) (typed FeaturePython)
  n = 0.878636
FEATURE [App::DocumentObjectGroupPython] Na_element007  label="Na_element : 0.000"  # scripted group (container) (typed FeaturePython)
  n = 2.2e-05
FEATURE [App::DocumentObjectGroupPython] S_element011  label="S_element : 0.013"  # scripted group (container) (typed FeaturePython)
  n = 0.012968
FEATURE [App::DocumentObjectGroupPython] Cl_element011  label="Cl_element : 0.000"  # scripted group (container) (typed FeaturePython)
  n = 3.4e-05
FEATURE [App::DocumentObjectGroupPython] Fe_element006  label="Fe_element : 0.000"  # scripted group (container) (typed FeaturePython)
  n = 5.4e-05
FEATURE [App::DocumentObjectGroupPython] G4_FERROUS_SULFATE  # scripted group (container) (typed FeaturePython)
  Dunit = g/cm3
  Dvalue = 1.024
  Group = -> [H_element040,N_element017,O_element040,Na_element007,S_element011,Cl_element011,Fe_element006]
  conduct = 2
  density = 1
  expand = 3
  formula = G4_FERROUS_SULFATE
  name = G4_FERROUS_SULFATE
  specific = 4
FEATURE [App::DocumentObjectGroupPython] C_element043  label="C_element : 0.099"  # scripted group (container) (typed FeaturePython)
  n = 0.099335
FEATURE [App::DocumentObjectGroupPython] F_element007  label="F_element : 0.314"  # scripted group (container) (typed FeaturePython)
  n = 0.314247
FEATURE [App::DocumentObjectGroupPython] Cl_element012  label="Cl_element : 0.586"  # scripted group (container) (typed FeaturePython)
  n = 0.586418
FEATURE [App::DocumentObjectGroupPython] G4_FREON_12  label="G4_FREON-12"  # scripted group (container) (typed FeaturePython)
  Dunit = g/cm3
  Dvalue = 1.12
  Group = -> [C_element043,F_element007,Cl_element012]
  conduct = 2
  density = 1
  expand = 3
  formula = G4_FREON-12
  name = G4_FREON-12
  specific = 4
FEATURE [App::DocumentObjectGroupPython] C_element044  label="C_element : 0.057"  # scripted group (container) (typed FeaturePython)
  n = 0.057245
FEATURE [App::DocumentObjectGroupPython] F_element008  label="F_element : 0.181"  # scripted group (container) (typed FeaturePython)
  n = 0.181096
FEATURE [App::DocumentObjectGroupPython] Br_element001  label="Br_element : 0.762"  # scripted group (container) (typed FeaturePython)
  n = 0.761659
FEATURE [App::DocumentObjectGroupPython] G4_FREON_12B2  label="G4_FREON-12B2"  # scripted group (container) (typed FeaturePython)
  Dunit = g/cm3
  Dvalue = 1.8
  Group = -> [C_element044,F_element008,Br_element001]
  conduct = 2
  density = 1
  expand = 3
  formula = G4_FREON-12B2
  name = G4_FREON-12B2
  specific = 4
FEATURE [App::DocumentObjectGroupPython] C_element045  label="C_element : 0.115"  # scripted group (container) (typed FeaturePython)
  n = 0.114983
FEATURE [App::DocumentObjectGroupPython] F_element009  label="F_element : 0.546"  # scripted group (container) (typed FeaturePython)
  n = 0.545621
FEATURE [App::DocumentObjectGroupPython] Cl_element013  label="Cl_element : 0.339"  # scripted group (container) (typed FeaturePython)
  n = 0.339396
FEATURE [App::DocumentObjectGroupPython] G4_FREON_13  label="G4_FREON-13"  # scripted group (container) (typed FeaturePython)
  Dunit = g/cm3
  Dvalue = 0.95
  Group = -> [C_element045,F_element009,Cl_element013]
  conduct = 2
  density = 1
  expand = 3
  formula = G4_FREON-13
  name = G4_FREON-13
  specific = 4
FEATURE [App::DocumentObjectGroupPython] C_element046  label="C_element : 025"  # scripted group (container) (typed FeaturePython)
  n = 1
  ref = C_element
FEATURE [App::DocumentObjectGroupPython] F_element010  label="F_element : 3"  # scripted group (container) (typed FeaturePython)
  n = 3
  ref = F_element
FEATURE [App::DocumentObjectGroupPython] Br_element002  label="Br_element : 1"  # scripted group (container) (typed FeaturePython)
  n = 1
  ref = Br_element
FEATURE [App::DocumentObjectGroupPython] G4_FREON_13B1  label="G4_FREON-13B1"  # scripted group (container) (typed FeaturePython)
  Dunit = g/cm3
  Dvalue = 1.5
  Group = -> [C_element046,F_element010,Br_element002]
  conduct = 2
  density = 1
  expand = 3
  formula = G4_FREON-13B1
  name = G4_FREON-13B1
  specific = 4
FEATURE [App::DocumentObjectGroupPython] C_element047  label="C_element : 0.061"  # scripted group (container) (typed FeaturePython)
  n = 0.061309
FEATURE [App::DocumentObjectGroupPython] F_element011  label="F_element : 0.291"  # scripted group (container) (typed FeaturePython)
  n = 0.290924
FEATURE [App::DocumentObjectGroupPython] I_element002  label="I_element : 0.648"  # scripted group (container) (typed FeaturePython)
  n = 0.647767
FEATURE [App::DocumentObjectGroupPython] G4_FREON_13I1  label="G4_FREON-13I1"  # scripted group (container) (typed FeaturePython)
  Dunit = g/cm3
  Dvalue = 1.8
  Group = -> [C_element047,F_element011,I_element002]
  conduct = 2
  density = 1
  expand = 3
  formula = G4_FREON-13I1
  name = G4_FREON-13I1
  specific = 4
FEATURE [App::DocumentObjectGroupPython] Gd_element001  label="Gd_element : 2"  # scripted group (container) (typed FeaturePython)
  n = 2
  ref = Gd_element
FEATURE [App::DocumentObjectGroupPython] O_element041  label="O_element : 021"  # scripted group (container) (typed FeaturePython)
  n = 2
  ref = O_element
FEATURE [App::DocumentObjectGroupPython] S_element012  label="S_element : 004"  # scripted group (container) (typed FeaturePython)
  n = 1
  ref = S_element
FEATURE [App::DocumentObjectGroupPython] G4_GADOLINIUM_OXYSULFIDE  # scripted group (container) (typed FeaturePython)
  Dunit = g/cm3
  Dvalue = 7.44
  Group = -> [Gd_element001,O_element041,S_element012]
  conduct = 2
  density = 1
  expand = 3
  formula = G4_GADOLINIUM_OXYSULFIDE
  name = G4_GADOLINIUM_OXYSULFIDE
  specific = 4
FEATURE [App::DocumentObjectGroupPython] Ga_element001  label="Ga_element : 1"  # scripted group (container) (typed FeaturePython)
  n = 1
  ref = Ga_element
FEATURE [App::DocumentObjectGroupPython] As_element001  label="As_element : 1"  # scripted group (container) (typed FeaturePython)
  n = 1
  ref = As_element
FEATURE [App::DocumentObjectGroupPython] G4_GALLIUM_ARSENIDE  # scripted group (container) (typed FeaturePython)
  Dunit = g/cm3
  Dvalue = 5.31
  Group = -> [Ga_element001,As_element001]
  conduct = 2
  density = 1
  expand = 3
  formula = G4_GALLIUM_ARSENIDE
  name = G4_GALLIUM_ARSENIDE
  specific = 4
FEATURE [App::DocumentObjectGroupPython] H_element041  label="H_element : 0.081"  # scripted group (container) (typed FeaturePython)
  n = 0.08118
FEATURE [App::DocumentObjectGroupPython] C_element048  label="C_element : 0.416"  # scripted group (container) (typed FeaturePython)
  n = 0.41606
FEATURE [App::DocumentObjectGroupPython] N_element018  label="N_element : 0.111"  # scripted group (container) (typed FeaturePython)
  n = 0.11124
FEATURE [App::DocumentObjectGroupPython] O_element042  label="O_element : 0.381"  # scripted group (container) (typed FeaturePython)
  n = 0.38064
FEATURE [App::DocumentObjectGroupPython] S_element013  label="S_element : 0.011"  # scripted group (container) (typed FeaturePython)
  n = 0.01088
FEATURE [App::DocumentObjectGroupPython] G4_GEL_PHOTO_EMULSION  # scripted group (container) (typed FeaturePython)
  Dunit = g/cm3
  Dvalue = 1.2914
  Group = -> [H_element041,C_element048,N_element018,O_element042,S_element013]
  conduct = 2
  density = 1
  expand = 3
  formula = G4_GEL_PHOTO_EMULSION
  name = G4_GEL_PHOTO_EMULSION
  specific = 4
FEATURE [App::DocumentObjectGroupPython] B_element004  label="B_element : 0.040"  # scripted group (container) (typed FeaturePython)
  n = 0.0400639
FEATURE [App::DocumentObjectGroupPython] O_element043  label="O_element : 0.540"  # scripted group (container) (typed FeaturePython)
  n = 0.539561
FEATURE [App::DocumentObjectGroupPython] Na_element008  label="Na_element : 0.028"  # scripted group (container) (typed FeaturePython)
  n = 0.0281909
FEATURE [App::DocumentObjectGroupPython] Al_element003  label="Al_element : 0.012"  # scripted group (container) (typed FeaturePython)
  n = 0.011644
FEATURE [App::DocumentObjectGroupPython] Si_element003  label="Si_element : 0.377"  # scripted group (container) (typed FeaturePython)
  n = 0.377219
FEATURE [App::DocumentObjectGroupPython] K_element004  label="K_element : 0.014"  # scripted group (container) (typed FeaturePython)
  n = 0.00332099
FEATURE [App::DocumentObjectGroupPython] G4_Pyrex_Glass  # scripted group (container) (typed FeaturePython)
  Dunit = g/cm3
  Dvalue = 2.23
  Group = -> [B_element004,O_element043,Na_element008,Al_element003,Si_element003,K_element004]
  conduct = 2
  density = 1
  expand = 3
  formula = G4_Pyrex_Glass
  name = G4_Pyrex_Glass
  specific = 4
FEATURE [App::DocumentObjectGroupPython] O_element044  label="O_element : 0.156"  # scripted group (container) (typed FeaturePython)
  n = 0.156453
FEATURE [App::DocumentObjectGroupPython] Si_element004  label="Si_element : 0.081"  # scripted group (container) (typed FeaturePython)
  n = 0.080866
FEATURE [App::DocumentObjectGroupPython] Ti_element001  label="Ti_element : 0.008"  # scripted group (container) (typed FeaturePython)
  n = 0.008092
FEATURE [App::DocumentObjectGroupPython] As_element002  label="As_element : 0.003"  # scripted group (container) (typed FeaturePython)
  n = 0.002651
FEATURE [App::DocumentObjectGroupPython] Pb_element001  label="Pb_element : 0.752"  # scripted group (container) (typed FeaturePython)
  n = 0.751938
FEATURE [App::DocumentObjectGroupPython] G4_GLASS_LEAD  # scripted group (container) (typed FeaturePython)
  Dunit = g/cm3
  Dvalue = 6.22
  Group = -> [O_element044,Si_element004,Ti_element001,As_element002,Pb_element001]
  conduct = 2
  density = 1
  expand = 3
  formula = G4_GLASS_LEAD
  name = G4_GLASS_LEAD
  specific = 4
FEATURE [App::DocumentObjectGroupPython] O_element045  label="O_element : 0.460"  # scripted group (container) (typed FeaturePython)
  n = 0.4598
FEATURE [App::DocumentObjectGroupPython] Na_element009  label="Na_element : 0.096"  # scripted group (container) (typed FeaturePython)
  n = 0.0964411
FEATURE [App::DocumentObjectGroupPython] Si_element005  label="Si_element : 0.378"  # scripted group (container) (typed FeaturePython)
  n = 0.336553
FEATURE [App::DocumentObjectGroupPython] Ca_element011  label="Ca_element : 0.107"  # scripted group (container) (typed FeaturePython)
  n = 0.107205
FEATURE [App::DocumentObjectGroupPython] G4_GLASS_PLATE  # scripted group (container) (typed FeaturePython)
  Dunit = g/cm3
  Dvalue = 2.4
  Group = -> [O_element045,Na_element009,Si_element005,Ca_element011]
  conduct = 2
  density = 1
  expand = 3
  formula = G4_GLASS_PLATE
  name = G4_GLASS_PLATE
  specific = 4
FEATURE [App::DocumentObjectGroupPython] C_element049  label="C_element : 026"  # scripted group (container) (typed FeaturePython)
  n = 5
  ref = C_element
FEATURE [App::DocumentObjectGroupPython] H_element042  label="H_element : 021"  # scripted group (container) (typed FeaturePython)
  n = 10
  ref = H_element
FEATURE [App::DocumentObjectGroupPython] N_element019  label="N_element : 2"  # scripted group (container) (typed FeaturePython)
  n = 2
  ref = N_element
FEATURE [App::DocumentObjectGroupPython] O_element046  label="O_element : 022"  # scripted group (container) (typed FeaturePython)
  n = 3
  ref = O_element
FEATURE [App::DocumentObjectGroupPython] G4_GLUTAMINE  # scripted group (container) (typed FeaturePython)
  Dunit = g/cm3
  Dvalue = 1.46
  Group = -> [C_element049,H_element042,N_element019,O_element046]
  conduct = 2
  density = 1
  expand = 3
  formula = G4_GLUTAMINE
  name = G4_GLUTAMINE
  specific = 4
FEATURE [App::DocumentObjectGroupPython] C_element050  label="C_element : 027"  # scripted group (container) (typed FeaturePython)
  n = 3
  ref = C_element
FEATURE [App::DocumentObjectGroupPython] H_element043  label="H_element : 022"  # scripted group (container) (typed FeaturePython)
  n = 8
  ref = H_element
FEATURE [App::DocumentObjectGroupPython] O_element047  label="O_element : 023"  # scripted group (container) (typed FeaturePython)
  n = 3
  ref = O_element
FEATURE [App::DocumentObjectGroupPython] G4_GLYCEROL  # scripted group (container) (typed FeaturePython)
  Dunit = g/cm3
  Dvalue = 1.2613
  Group = -> [C_element050,H_element043,O_element047]
  conduct = 2
  density = 1
  expand = 3
  formula = G4_GLYCEROL
  name = G4_GLYCEROL
  specific = 4
FEATURE [App::DocumentObjectGroupPython] C_element051  label="C_element : 028"  # scripted group (container) (typed FeaturePython)
  n = 5
  ref = C_element
FEATURE [App::DocumentObjectGroupPython] H_element044  label="H_element : 023"  # scripted group (container) (typed FeaturePython)
  n = 5
  ref = H_element
FEATURE [App::DocumentObjectGroupPython] N_element020  label="N_element : 009"  # scripted group (container) (typed FeaturePython)
  n = 5
  ref = N_element
FEATURE [App::DocumentObjectGroupPython] O_element048  label="O_element : 024"  # scripted group (container) (typed FeaturePython)
  n = 1
  ref = O_element
FEATURE [App::DocumentObjectGroupPython] G4_GUANINE  # scripted group (container) (typed FeaturePython)
  Dunit = g/cm3
  Dvalue = 2.2
  Group = -> [C_element051,H_element044,N_element020,O_element048]
  conduct = 2
  density = 1
  expand = 3
  formula = G4_GUANINE
  name = G4_GUANINE
  specific = 4
FEATURE [App::DocumentObjectGroupPython] Ca_element012  label="Ca_element : 006"  # scripted group (container) (typed FeaturePython)
  n = 1
  ref = Ca_element
FEATURE [App::DocumentObjectGroupPython] S_element014  label="S_element : 005"  # scripted group (container) (typed FeaturePython)
  n = 1
  ref = S_element
FEATURE [App::DocumentObjectGroupPython] O_element049  label="O_element : 6"  # scripted group (container) (typed FeaturePython)
  n = 6
  ref = O_element
FEATURE [App::DocumentObjectGroupPython] H_element045  label="H_element : 024"  # scripted group (container) (typed FeaturePython)
  n = 4
  ref = H_element
FEATURE [App::DocumentObjectGroupPython] G4_GYPSUM  # scripted group (container) (typed FeaturePython)
  Dunit = g/cm3
  Dvalue = 2.32
  Group = -> [Ca_element012,S_element014,O_element049,H_element045]
  conduct = 2
  density = 1
  expand = 3
  formula = G4_GYPSUM
  name = G4_GYPSUM
  specific = 4
FEATURE [App::DocumentObjectGroupPython] C_element052  label="C_element : 7"  # scripted group (container) (typed FeaturePython)
  n = 7
  ref = C_element
FEATURE [App::DocumentObjectGroupPython] H_element046  label="H_element : 16"  # scripted group (container) (typed FeaturePython)
  n = 16
  ref = H_element
FEATURE [App::DocumentObjectGroupPython] G4_N_HEPTANE  label="G4_N-HEPTANE"  # scripted group (container) (typed FeaturePython)
  Dunit = g/cm3
  Dvalue = 0.68376
  Group = -> [C_element052,H_element046]
  conduct = 2
  density = 1
  expand = 3
  formula = G4_N-HEPTANE
  name = G4_N-HEPTANE
  specific = 4
FEATURE [App::DocumentObjectGroupPython] C_element053  label="C_element : 029"  # scripted group (container) (typed FeaturePython)
  n = 6
  ref = C_element
FEATURE [App::DocumentObjectGroupPython] H_element047  label="H_element : 14"  # scripted group (container) (typed FeaturePython)
  n = 14
  ref = H_element
FEATURE [App::DocumentObjectGroupPython] G4_N_HEXANE  label="G4_N-HEXANE"  # scripted group (container) (typed FeaturePython)
  Dunit = g/cm3
  Dvalue = 0.6603
  Group = -> [C_element053,H_element047]
  conduct = 2
  density = 1
  expand = 3
  formula = G4_N-HEXANE
  name = G4_N-HEXANE
  specific = 4
FEATURE [App::DocumentObjectGroupPython] C_element054  label="C_element : 22"  # scripted group (container) (typed FeaturePython)
  n = 22
  ref = C_element
FEATURE [App::DocumentObjectGroupPython] H_element048  label="H_element : 025"  # scripted group (container) (typed FeaturePython)
  n = 10
  ref = H_element
FEATURE [App::DocumentObjectGroupPython] N_element021  label="N_element : 010"  # scripted group (container) (typed FeaturePython)
  n = 2
  ref = N_element
FEATURE [App::DocumentObjectGroupPython] O_element050  label="O_element : 025"  # scripted group (container) (typed FeaturePython)
  n = 5
  ref = O_element
FEATURE [App::DocumentObjectGroupPython] G4_KAPTON  # scripted group (container) (typed FeaturePython)
  Dunit = g/cm3
  Dvalue = 1.42
  Group = -> [C_element054,H_element048,N_element021,O_element050]
  conduct = 2
  density = 1
  expand = 3
  formula = G4_KAPTON
  name = G4_KAPTON
  specific = 4
FEATURE [App::DocumentObjectGroupPython] La_element001  label="La_element : 1"  # scripted group (container) (typed FeaturePython)
  n = 1
  ref = La_element
FEATURE [App::DocumentObjectGroupPython] Br_element003  label="Br_element : 002"  # scripted group (container) (typed FeaturePython)
  n = 1
  ref = Br_element
FEATURE [App::DocumentObjectGroupPython] O_element051  label="O_element : 026"  # scripted group (container) (typed FeaturePython)
  n = 1
  ref = O_element
FEATURE [App::DocumentObjectGroupPython] G4_LANTHANUM_OXYBROMIDE  # scripted group (container) (typed FeaturePython)
  Dunit = g/cm3
  Dvalue = 6.28
  Group = -> [La_element001,Br_element003,O_element051]
  conduct = 2
  density = 1
  expand = 3
  formula = G4_LANTHANUM_OXYBROMIDE
  name = G4_LANTHANUM_OXYBROMIDE
  specific = 4
FEATURE [App::DocumentObjectGroupPython] La_element002  label="La_element : 2"  # scripted group (container) (typed FeaturePython)
  n = 2
  ref = La_element
FEATURE [App::DocumentObjectGroupPython] O_element052  label="O_element : 027"  # scripted group (container) (typed FeaturePython)
  n = 2
  ref = O_element
FEATURE [App::DocumentObjectGroupPython] S_element015  label="S_element : 006"  # scripted group (container) (typed FeaturePython)
  n = 1
  ref = S_element
FEATURE [App::DocumentObjectGroupPython] G4_LANTHANUM_OXYSULFIDE  # scripted group (container) (typed FeaturePython)
  Dunit = g/cm3
  Dvalue = 5.86
  Group = -> [La_element002,O_element052,S_element015]
  conduct = 2
  density = 1
  expand = 3
  formula = G4_LANTHANUM_OXYSULFIDE
  name = G4_LANTHANUM_OXYSULFIDE
  specific = 4
FEATURE [App::DocumentObjectGroupPython] O_element053  label="O_element : 0.072"  # scripted group (container) (typed FeaturePython)
  n = 0.071682
FEATURE [App::DocumentObjectGroupPython] Pb_element002  label="Pb_element : 0.928"  # scripted group (container) (typed FeaturePython)
  n = 0.928318
FEATURE [App::DocumentObjectGroupPython] G4_LEAD_OXIDE  # scripted group (container) (typed FeaturePython)
  Dunit = g/cm3
  Dvalue = 9.53
  Group = -> [O_element053,Pb_element002]
  conduct = 2
  density = 1
  expand = 3
  formula = G4_LEAD_OXIDE
  name = G4_LEAD_OXIDE
  specific = 4
FEATURE [App::DocumentObjectGroupPython] Li_element001  label="Li_element : 1"  # scripted group (container) (typed FeaturePython)
  n = 1
  ref = Li_element
FEATURE [App::DocumentObjectGroupPython] N_element022  label="N_element : 011"  # scripted group (container) (typed FeaturePython)
  n = 1
  ref = N_element
FEATURE [App::DocumentObjectGroupPython] H_element049  label="H_element : 026"  # scripted group (container) (typed FeaturePython)
  n = 2
  ref = H_element
FEATURE [App::DocumentObjectGroupPython] G4_LITHIUM_AMIDE  # scripted group (container) (typed FeaturePython)
  Dunit = g/cm3
  Dvalue = 1.178
  Group = -> [Li_element001,N_element022,H_element049]
  conduct = 2
  density = 1
  expand = 3
  formula = G4_LITHIUM_AMIDE
  name = G4_LITHIUM_AMIDE
  specific = 4
FEATURE [App::DocumentObjectGroupPython] Li_element002  label="Li_element : 2"  # scripted group (container) (typed FeaturePython)
  n = 2
  ref = Li_element
FEATURE [App::DocumentObjectGroupPython] C_element055  label="C_element : 030"  # scripted group (container) (typed FeaturePython)
  n = 1
  ref = C_element
FEATURE [App::DocumentObjectGroupPython] O_element054  label="O_element : 028"  # scripted group (container) (typed FeaturePython)
  n = 3
  ref = O_element
FEATURE [App::DocumentObjectGroupPython] G4_LITHIUM_CARBONATE  # scripted group (container) (typed FeaturePython)
  Dunit = g/cm3
  Dvalue = 2.11
  Group = -> [Li_element002,C_element055,O_element054]
  conduct = 2
  density = 1
  expand = 3
  formula = G4_LITHIUM_CARBONATE
  name = G4_LITHIUM_CARBONATE
  specific = 4
FEATURE [App::DocumentObjectGroupPython] Li_element003  label="Li_element : 003"  # scripted group (container) (typed FeaturePython)
  n = 1
  ref = Li_element
FEATURE [App::DocumentObjectGroupPython] F_element012  label="F_element : 004"  # scripted group (container) (typed FeaturePython)
  n = 1
  ref = F_element
FEATURE [App::DocumentObjectGroupPython] G4_LITHIUM_FLUORIDE  # scripted group (container) (typed FeaturePython)
  Dunit = g/cm3
  Dvalue = 2.635
  Group = -> [Li_element003,F_element012]
  conduct = 2
  density = 1
  expand = 3
  formula = G4_LITHIUM_FLUORIDE
  name = G4_LITHIUM_FLUORIDE
  specific = 4
FEATURE [App::DocumentObjectGroupPython] Li_element004  label="Li_element : 004"  # scripted group (container) (typed FeaturePython)
  n = 1
  ref = Li_element
FEATURE [App::DocumentObjectGroupPython] H_element050  label="H_element : 027"  # scripted group (container) (typed FeaturePython)
  n = 1
  ref = H_element
FEATURE [App::DocumentObjectGroupPython] G4_LITHIUM_HYDRIDE  # scripted group (container) (typed FeaturePython)
  Dunit = g/cm3
  Dvalue = 0.82
  Group = -> [Li_element004,H_element050]
  conduct = 2
  density = 1
  expand = 3
  formula = G4_LITHIUM_HYDRIDE
  name = G4_LITHIUM_HYDRIDE
  specific = 4
FEATURE [App::DocumentObjectGroupPython] Li_element005  label="Li_element : 005"  # scripted group (container) (typed FeaturePython)
  n = 1
  ref = Li_element
FEATURE [App::DocumentObjectGroupPython] I_element003  label="I_element : 002"  # scripted group (container) (typed FeaturePython)
  n = 1
  ref = I_element
FEATURE [App::DocumentObjectGroupPython] G4_LITHIUM_IODIDE  # scripted group (container) (typed FeaturePython)
  Dunit = g/cm3
  Dvalue = 3.494
  Group = -> [Li_element005,I_element003]
  conduct = 2
  density = 1
  expand = 3
  formula = G4_LITHIUM_IODIDE
  name = G4_LITHIUM_IODIDE
  specific = 4
FEATURE [App::DocumentObjectGroupPython] Li_element006  label="Li_element : 006"  # scripted group (container) (typed FeaturePython)
  n = 2
  ref = Li_element
FEATURE [App::DocumentObjectGroupPython] O_element055  label="O_element : 029"  # scripted group (container) (typed FeaturePython)
  n = 1
  ref = O_element
FEATURE [App::DocumentObjectGroupPython] G4_LITHIUM_OXIDE  # scripted group (container) (typed FeaturePython)
  Dunit = g/cm3
  Dvalue = 2.013
  Group = -> [Li_element006,O_element055]
  conduct = 2
  density = 1
  expand = 3
  formula = G4_LITHIUM_OXIDE
  name = G4_LITHIUM_OXIDE
  specific = 4
FEATURE [App::DocumentObjectGroupPython] Li_element007  label="Li_element : 007"  # scripted group (container) (typed FeaturePython)
  n = 2
  ref = Li_element
FEATURE [App::DocumentObjectGroupPython] B_element005  label="B_element : 005"  # scripted group (container) (typed FeaturePython)
  n = 4
  ref = B_element
FEATURE [App::DocumentObjectGroupPython] O_element056  label="O_element : 7"  # scripted group (container) (typed FeaturePython)
  n = 7
  ref = O_element
FEATURE [App::DocumentObjectGroupPython] G4_LITHIUM_TETRABORATE  # scripted group (container) (typed FeaturePython)
  Dunit = g/cm3
  Dvalue = 2.44
  Group = -> [Li_element007,B_element005,O_element056]
  conduct = 2
  density = 1
  expand = 3
  formula = G4_LITHIUM_TETRABORATE
  name = G4_LITHIUM_TETRABORATE
  specific = 4
FEATURE [App::DocumentObjectGroupPython] H_element051  label="H_element : 0.105"  # scripted group (container) (typed FeaturePython)
  n = 0.105
FEATURE [App::DocumentObjectGroupPython] C_element056  label="C_element : 0.083"  # scripted group (container) (typed FeaturePython)
  n = 0.083
FEATURE [App::DocumentObjectGroupPython] N_element023  label="N_element : 0.023"  # scripted group (container) (typed FeaturePython)
  n = 0.023
FEATURE [App::DocumentObjectGroupPython] O_element057  label="O_element : 0.779"  # scripted group (container) (typed FeaturePython)
  n = 0.779
FEATURE [App::DocumentObjectGroupPython] Na_element010  label="Na_element : 0.097"  # scripted group (container) (typed FeaturePython)
  n = 0.002
FEATURE [App::DocumentObjectGroupPython] P_element006  label="P_element : 0.105"  # scripted group (container) (typed FeaturePython)
  n = 0.001
FEATURE [App::DocumentObjectGroupPython] S_element016  label="S_element : 0.017"  # scripted group (container) (typed FeaturePython)
  n = 0.002
FEATURE [App::DocumentObjectGroupPython] Cl_element014  label="Cl_element : 0.587"  # scripted group (container) (typed FeaturePython)
  n = 0.003
FEATURE [App::DocumentObjectGroupPython] K_element005  label="K_element : 0.015"  # scripted group (container) (typed FeaturePython)
  n = 0.002
FEATURE [App::DocumentObjectGroupPython] G4_LUNG_ICRP  # scripted group (container) (typed FeaturePython)
  Dunit = g/cm3
  Dvalue = 1.04
  Group = -> [H_element051,C_element056,N_element023,O_element057,Na_element010,P_element006,S_element016,Cl_element014,K_element005]
  conduct = 2
  density = 1
  expand = 3
  formula = G4_LUNG_ICRP
  name = G4_LUNG_ICRP
  specific = 4
FEATURE [App::DocumentObjectGroupPython] H_element052  label="H_element : 0.116"  # scripted group (container) (typed FeaturePython)
  n = 0.114318
FEATURE [App::DocumentObjectGroupPython] C_element057  label="C_element : 0.656"  # scripted group (container) (typed FeaturePython)
  n = 0.655824
FEATURE [App::DocumentObjectGroupPython] O_element058  label="O_element : 0.092"  # scripted group (container) (typed FeaturePython)
  n = 0.0921831
FEATURE [App::DocumentObjectGroupPython] Mg_element004  label="Mg_element : 0.135"  # scripted group (container) (typed FeaturePython)
  n = 0.134792
FEATURE [App::DocumentObjectGroupPython] Ca_element013  label="Ca_element : 0.003"  # scripted group (container) (typed FeaturePython)
  n = 0.002883
FEATURE [App::DocumentObjectGroupPython] G4_M3_WAX  # scripted group (container) (typed FeaturePython)
  Dunit = g/cm3
  Dvalue = 1.05
  Group = -> [H_element052,C_element057,O_element058,Mg_element004,Ca_element013]
  conduct = 2
  density = 1
  expand = 3
  formula = G4_M3_WAX
  name = G4_M3_WAX
  specific = 4
FEATURE [App::DocumentObjectGroupPython] Mg_element005  label="Mg_element : 1"  # scripted group (container) (typed FeaturePython)
  n = 1
  ref = Mg_element
FEATURE [App::DocumentObjectGroupPython] C_element058  label="C_element : 031"  # scripted group (container) (typed FeaturePython)
  n = 1
  ref = C_element
FEATURE [App::DocumentObjectGroupPython] O_element059  label="O_element : 030"  # scripted group (container) (typed FeaturePython)
  n = 3
  ref = O_element
FEATURE [App::DocumentObjectGroupPython] G4_MAGNESIUM_CARBONATE  # scripted group (container) (typed FeaturePython)
  Dunit = g/cm3
  Dvalue = 2.958
  Group = -> [Mg_element005,C_element058,O_element059]
  conduct = 2
  density = 1
  expand = 3
  formula = G4_MAGNESIUM_CARBONATE
  name = G4_MAGNESIUM_CARBONATE
  specific = 4
FEATURE [App::DocumentObjectGroupPython] Mg_element006  label="Mg_element : 002"  # scripted group (container) (typed FeaturePython)
  n = 1
  ref = Mg_element
FEATURE [App::DocumentObjectGroupPython] F_element013  label="F_element : 005"  # scripted group (container) (typed FeaturePython)
  n = 2
  ref = F_element
FEATURE [App::DocumentObjectGroupPython] G4_MAGNESIUM_FLUORIDE  # scripted group (container) (typed FeaturePython)
  Dunit = g/cm3
  Dvalue = 3
  Group = -> [Mg_element006,F_element013]
  conduct = 2
  density = 1
  expand = 3
  formula = G4_MAGNESIUM_FLUORIDE
  name = G4_MAGNESIUM_FLUORIDE
  specific = 4
FEATURE [App::DocumentObjectGroupPython] Mg_element007  label="Mg_element : 003"  # scripted group (container) (typed FeaturePython)
  n = 1
  ref = Mg_element
FEATURE [App::DocumentObjectGroupPython] O_element060  label="O_element : 031"  # scripted group (container) (typed FeaturePython)
  n = 1
  ref = O_element
FEATURE [App::DocumentObjectGroupPython] G4_MAGNESIUM_OXIDE  # scripted group (container) (typed FeaturePython)
  Dunit = g/cm3
  Dvalue = 3.58
  Group = -> [Mg_element007,O_element060]
  conduct = 2
  density = 1
  expand = 3
  formula = G4_MAGNESIUM_OXIDE
  name = G4_MAGNESIUM_OXIDE
  specific = 4
FEATURE [App::DocumentObjectGroupPython] Mg_element008  label="Mg_element : 004"  # scripted group (container) (typed FeaturePython)
  n = 1
  ref = Mg_element
FEATURE [App::DocumentObjectGroupPython] B_element006  label="B_element : 006"  # scripted group (container) (typed FeaturePython)
  n = 4
  ref = B_element
FEATURE [App::DocumentObjectGroupPython] O_element061  label="O_element : 032"  # scripted group (container) (typed FeaturePython)
  n = 7
  ref = O_element
FEATURE [App::DocumentObjectGroupPython] G4_MAGNESIUM_TETRABORATE  # scripted group (container) (typed FeaturePython)
  Dunit = g/cm3
  Dvalue = 2.53
  Group = -> [Mg_element008,B_element006,O_element061]
  conduct = 2
  density = 1
  expand = 3
  formula = G4_MAGNESIUM_TETRABORATE
  name = G4_MAGNESIUM_TETRABORATE
  specific = 4
FEATURE [App::DocumentObjectGroupPython] Hg_element001  label="Hg_element : 1"  # scripted group (container) (typed FeaturePython)
  n = 1
  ref = Hg_element
FEATURE [App::DocumentObjectGroupPython] I_element004  label="I_element : 2"  # scripted group (container) (typed FeaturePython)
  n = 2
  ref = I_element
FEATURE [App::DocumentObjectGroupPython] G4_MERCURIC_IODIDE  # scripted group (container) (typed FeaturePython)
  Dunit = g/cm3
  Dvalue = 6.36
  Group = -> [Hg_element001,I_element004]
  conduct = 2
  density = 1
  expand = 3
  formula = G4_MERCURIC_IODIDE
  name = G4_MERCURIC_IODIDE
  specific = 4
FEATURE [App::DocumentObjectGroupPython] C_element059  label="C_element : 032"  # scripted group (container) (typed FeaturePython)
  n = 1
  ref = C_element
FEATURE [App::DocumentObjectGroupPython] H_element053  label="H_element : 028"  # scripted group (container) (typed FeaturePython)
  n = 4
  ref = H_element
FEATURE [App::DocumentObjectGroupPython] G4_METHANE  # scripted group (container) (typed FeaturePython)
  Dunit = g/cm3
  Dvalue = 0.000667151
  Group = -> [C_element059,H_element053]
  conduct = 2
  density = 1
  expand = 3
  formula = G4_METHANE
  name = G4_METHANE
  specific = 4
FEATURE [App::DocumentObjectGroupPython] C_element060  label="C_element : 033"  # scripted group (container) (typed FeaturePython)
  n = 1
  ref = C_element
FEATURE [App::DocumentObjectGroupPython] H_element054  label="H_element : 029"  # scripted group (container) (typed FeaturePython)
  n = 4
  ref = H_element
FEATURE [App::DocumentObjectGroupPython] O_element062  label="O_element : 033"  # scripted group (container) (typed FeaturePython)
  n = 1
  ref = O_element
FEATURE [App::DocumentObjectGroupPython] G4_METHANOL  # scripted group (container) (typed FeaturePython)
  Dunit = g/cm3
  Dvalue = 0.7914
  Group = -> [C_element060,H_element054,O_element062]
  conduct = 2
  density = 1
  expand = 3
  formula = G4_METHANOL
  name = G4_METHANOL
  specific = 4
FEATURE [App::DocumentObjectGroupPython] H_element055  label="H_element : 0.134"  # scripted group (container) (typed FeaturePython)
  n = 0.13404
FEATURE [App::DocumentObjectGroupPython] C_element061  label="C_element : 0.778"  # scripted group (container) (typed FeaturePython)
  n = 0.77796
FEATURE [App::DocumentObjectGroupPython] O_element063  label="O_element : 0.035"  # scripted group (container) (typed FeaturePython)
  n = 0.03502
FEATURE [App::DocumentObjectGroupPython] Mg_element009  label="Mg_element : 0.039"  # scripted group (container) (typed FeaturePython)
  n = 0.038594
FEATURE [App::DocumentObjectGroupPython] Ti_element002  label="Ti_element : 0.014"  # scripted group (container) (typed FeaturePython)
  n = 0.014386
FEATURE [App::DocumentObjectGroupPython] G4_MIX_D_WAX  # scripted group (container) (typed FeaturePython)
  Dunit = g/cm3
  Dvalue = 0.99
  Group = -> [H_element055,C_element061,O_element063,Mg_element009,Ti_element002]
  conduct = 2
  density = 1
  expand = 3
  formula = G4_MIX_D_WAX
  name = G4_MIX_D_WAX
  specific = 4
FEATURE [App::DocumentObjectGroupPython] H_element056  label="H_element : 0.135"  # scripted group (container) (typed FeaturePython)
  n = 0.081192
FEATURE [App::DocumentObjectGroupPython] C_element062  label="C_element : 0.583"  # scripted group (container) (typed FeaturePython)
  n = 0.583442
FEATURE [App::DocumentObjectGroupPython] N_element024  label="N_element : 0.018"  # scripted group (container) (typed FeaturePython)
  n = 0.017798
FEATURE [App::DocumentObjectGroupPython] O_element064  label="O_element : 0.186"  # scripted group (container) (typed FeaturePython)
  n = 0.186381
FEATURE [App::DocumentObjectGroupPython] Mg_element010  label="Mg_element : 0.130"  # scripted group (container) (typed FeaturePython)
  n = 0.130287
FEATURE [App::DocumentObjectGroupPython] Cl_element015  label="Cl_element : 0.588"  # scripted group (container) (typed FeaturePython)
  n = 0.0009
FEATURE [App::DocumentObjectGroupPython] G4_MS20_TISSUE  # scripted group (container) (typed FeaturePython)
  Dunit = g/cm3
  Dvalue = 1
  Group = -> [H_element056,C_element062,N_element024,O_element064,Mg_element010,Cl_element015]
  conduct = 2
  density = 1
  expand = 3
  formula = G4_MS20_TISSUE
  name = G4_MS20_TISSUE
  specific = 4
FEATURE [App::DocumentObjectGroupPython] H_element057  label="H_element : 0.136"  # scripted group (container) (typed FeaturePython)
  n = 0.102
FEATURE [App::DocumentObjectGroupPython] C_element063  label="C_element : 0.143"  # scripted group (container) (typed FeaturePython)
  n = 0.143
FEATURE [App::DocumentObjectGroupPython] N_element025  label="N_element : 0.034"  # scripted group (container) (typed FeaturePython)
  n = 0.034
FEATURE [App::DocumentObjectGroupPython] O_element065  label="O_element : 0.710"  # scripted group (container) (typed FeaturePython)
  n = 0.71
FEATURE [App::DocumentObjectGroupPython] Na_element011  label="Na_element : 0.098"  # scripted group (container) (typed FeaturePython)
  n = 0.001
FEATURE [App::DocumentObjectGroupPython] P_element007  label="P_element : 0.002"  # scripted group (container) (typed FeaturePython)
  n = 0.002
FEATURE [App::DocumentObjectGroupPython] S_element017  label="S_element : 0.018"  # scripted group (container) (typed FeaturePython)
  n = 0.003
FEATURE [App::DocumentObjectGroupPython] Cl_element016  label="Cl_element : 0.589"  # scripted group (container) (typed FeaturePython)
  n = 0.001
FEATURE [App::DocumentObjectGroupPython] K_element006  label="K_element : 0.004"  # scripted group (container) (typed FeaturePython)
  n = 0.004
FEATURE [App::DocumentObjectGroupPython] G4_MUSCLE_SKELETAL_ICRP  # scripted group (container) (typed FeaturePython)
  Dunit = g/cm3
  Dvalue = 1.05
  Group = -> [H_element057,C_element063,N_element025,O_element065,Na_element011,P_element007,S_element017,Cl_element016,K_element006]
  conduct = 2
  density = 1
  expand = 3
  formula = G4_MUSCLE_SKELETAL_ICRP
  name = G4_MUSCLE_SKELETAL_ICRP
  specific = 4
FEATURE [App::DocumentObjectGroupPython] H_element058  label="H_element : 0.137"  # scripted group (container) (typed FeaturePython)
  n = 0.102102
FEATURE [App::DocumentObjectGroupPython] C_element064  label="C_element : 0.123"  # scripted group (container) (typed FeaturePython)
  n = 0.123123
FEATURE [App::DocumentObjectGroupPython] N_element026  label="N_element : 0.756"  # scripted group (container) (typed FeaturePython)
  n = 0.035035
FEATURE [App::DocumentObjectGroupPython] O_element066  label="O_element : 0.730"  # scripted group (container) (typed FeaturePython)
  n = 0.72973
FEATURE [App::DocumentObjectGroupPython] Na_element012  label="Na_element : 0.099"  # scripted group (container) (typed FeaturePython)
  n = 0.001001
FEATURE [App::DocumentObjectGroupPython] P_element008  label="P_element : 0.106"  # scripted group (container) (typed FeaturePython)
  n = 0.002002
FEATURE [App::DocumentObjectGroupPython] S_element018  label="S_element : 0.019"  # scripted group (container) (typed FeaturePython)
  n = 0.004004
FEATURE [App::DocumentObjectGroupPython] K_element007  label="K_element : 0.016"  # scripted group (container) (typed FeaturePython)
  n = 0.003003
FEATURE [App::DocumentObjectGroupPython] G4_MUSCLE_STRIATED_ICRU  # scripted group (container) (typed FeaturePython)
  Dunit = g/cm3
  Dvalue = 1.04
  Group = -> [H_element058,C_element064,N_element026,O_element066,Na_element012,P_element008,S_element018,K_element007]
  conduct = 2
  density = 1
  expand = 3
  formula = G4_MUSCLE_STRIATED_ICRU
  name = G4_MUSCLE_STRIATED_ICRU
  specific = 4
FEATURE [App::DocumentObjectGroupPython] H_element059  label="H_element : 0.098"  # scripted group (container) (typed FeaturePython)
  n = 0.0982341
FEATURE [App::DocumentObjectGroupPython] C_element065  label="C_element : 0.156"  # scripted group (container) (typed FeaturePython)
  n = 0.156214
FEATURE [App::DocumentObjectGroupPython] N_element027  label="N_element : 0.757"  # scripted group (container) (typed FeaturePython)
  n = 0.035451
FEATURE [App::DocumentObjectGroupPython] O_element067  label="O_element : 0.880"  # scripted group (container) (typed FeaturePython)
  n = 0.710101
FEATURE [App::DocumentObjectGroupPython] G4_MUSCLE_WITH_SUCROSE  # scripted group (container) (typed FeaturePython)
  Dunit = g/cm3
  Dvalue = 1.11
  Group = -> [H_element059,C_element065,N_element027,O_element067]
  conduct = 2
  density = 1
  expand = 3
  formula = G4_MUSCLE_WITH_SUCROSE
  name = G4_MUSCLE_WITH_SUCROSE
  specific = 4
FEATURE [App::DocumentObjectGroupPython] H_element060  label="H_element : 0.138"  # scripted group (container) (typed FeaturePython)
  n = 0.101969
FEATURE [App::DocumentObjectGroupPython] C_element066  label="C_element : 0.120"  # scripted group (container) (typed FeaturePython)
  n = 0.120058
FEATURE [App::DocumentObjectGroupPython] N_element028  label="N_element : 0.758"  # scripted group (container) (typed FeaturePython)
  n = 0.035451
FEATURE [App::DocumentObjectGroupPython] O_element068  label="O_element : 0.743"  # scripted group (container) (typed FeaturePython)
  n = 0.742522
FEATURE [App::DocumentObjectGroupPython] G4_MUSCLE_WITHOUT_SUCROSE  # scripted group (container) (typed FeaturePython)
  Dunit = g/cm3
  Dvalue = 1.07
  Group = -> [H_element060,C_element066,N_element028,O_element068]
  conduct = 2
  density = 1
  expand = 3
  formula = G4_MUSCLE_WITHOUT_SUCROSE
  name = G4_MUSCLE_WITHOUT_SUCROSE
  specific = 4
FEATURE [App::DocumentObjectGroupPython] C_element067  label="C_element : 10"  # scripted group (container) (typed FeaturePython)
  n = 10
  ref = C_element
FEATURE [App::DocumentObjectGroupPython] H_element061  label="H_element : 030"  # scripted group (container) (typed FeaturePython)
  n = 8
  ref = H_element
FEATURE [App::DocumentObjectGroupPython] G4_NAPHTHALENE  # scripted group (container) (typed FeaturePython)
  Dunit = g/cm3
  Dvalue = 1.145
  Group = -> [C_element067,H_element061]
  conduct = 2
  density = 1
  expand = 3
  formula = G4_NAPHTHALENE
  name = G4_NAPHTHALENE
  specific = 4
FEATURE [App::DocumentObjectGroupPython] C_element068  label="C_element : 034"  # scripted group (container) (typed FeaturePython)
  n = 6
  ref = C_element
FEATURE [App::DocumentObjectGroupPython] H_element062  label="H_element : 031"  # scripted group (container) (typed FeaturePython)
  n = 5
  ref = H_element
FEATURE [App::DocumentObjectGroupPython] N_element029  label="N_element : 012"  # scripted group (container) (typed FeaturePython)
  n = 1
  ref = N_element
FEATURE [App::DocumentObjectGroupPython] O_element069  label="O_element : 034"  # scripted group (container) (typed FeaturePython)
  n = 2
  ref = O_element
FEATURE [App::DocumentObjectGroupPython] G4_NITROBENZENE  # scripted group (container) (typed FeaturePython)
  Dunit = g/cm3
  Dvalue = 1.19867
  Group = -> [C_element068,H_element062,N_element029,O_element069]
  conduct = 2
  density = 1
  expand = 3
  formula = G4_NITROBENZENE
  name = G4_NITROBENZENE
  specific = 4
FEATURE [App::DocumentObjectGroupPython] N_element030  label="N_element : 013"  # scripted group (container) (typed FeaturePython)
  n = 2
  ref = N_element
FEATURE [App::DocumentObjectGroupPython] O_element070  label="O_element : 035"  # scripted group (container) (typed FeaturePython)
  n = 1
  ref = O_element
FEATURE [App::DocumentObjectGroupPython] G4_NITROUS_OXIDE  # scripted group (container) (typed FeaturePython)
  Dunit = g/cm3
  Dvalue = 0.00183094
  Group = -> [N_element030,O_element070]
  conduct = 2
  density = 1
  expand = 3
  formula = G4_NITROUS_OXIDE
  name = G4_NITROUS_OXIDE
  specific = 4
FEATURE [App::DocumentObjectGroupPython] H_element063  label="H_element : 0.104"  # scripted group (container) (typed FeaturePython)
  n = 0.103509
FEATURE [App::DocumentObjectGroupPython] C_element069  label="C_element : 0.648"  # scripted group (container) (typed FeaturePython)
  n = 0.648416
FEATURE [App::DocumentObjectGroupPython] N_element031  label="N_element : 0.100"  # scripted group (container) (typed FeaturePython)
  n = 0.0995361
FEATURE [App::DocumentObjectGroupPython] O_element071  label="O_element : 0.149"  # scripted group (container) (typed FeaturePython)
  n = 0.148539
FEATURE [App::DocumentObjectGroupPython] G4_NYLON_8062  label="G4_NYLON-8062"  # scripted group (container) (typed FeaturePython)
  Dunit = g/cm3
  Dvalue = 1.08
  Group = -> [H_element063,C_element069,N_element031,O_element071]
  conduct = 2
  density = 1
  expand = 3
  formula = G4_NYLON-8062
  name = G4_NYLON-8062
  specific = 4
FEATURE [App::DocumentObjectGroupPython] C_element070  label="C_element : 035"  # scripted group (container) (typed FeaturePython)
  n = 6
  ref = C_element
FEATURE [App::DocumentObjectGroupPython] H_element064  label="H_element : 11"  # scripted group (container) (typed FeaturePython)
  n = 11
  ref = H_element
FEATURE [App::DocumentObjectGroupPython] N_element032  label="N_element : 014"  # scripted group (container) (typed FeaturePython)
  n = 1
  ref = N_element
FEATURE [App::DocumentObjectGroupPython] O_element072  label="O_element : 036"  # scripted group (container) (typed FeaturePython)
  n = 1
  ref = O_element
FEATURE [App::DocumentObjectGroupPython] G4_NYLON_6_6  label="G4_NYLON-6-6"  # scripted group (container) (typed FeaturePython)
  Dunit = g/cm3
  Dvalue = 1.14
  Group = -> [C_element070,H_element064,N_element032,O_element072]
  conduct = 2
  density = 1
  expand = 3
  formula = G4_NYLON-6-6
  name = G4_NYLON-6-6
  specific = 4
FEATURE [App::DocumentObjectGroupPython] H_element065  label="H_element : 0.139"  # scripted group (container) (typed FeaturePython)
  n = 0.107062
FEATURE [App::DocumentObjectGroupPython] C_element071  label="C_element : 0.680"  # scripted group (container) (typed FeaturePython)
  n = 0.680449
FEATURE [App::DocumentObjectGroupPython] N_element033  label="N_element : 0.099"  # scripted group (container) (typed FeaturePython)
  n = 0.099189
FEATURE [App::DocumentObjectGroupPython] O_element073  label="O_element : 0.113"  # scripted group (container) (typed FeaturePython)
  n = 0.1133
FEATURE [App::DocumentObjectGroupPython] G4_NYLON_6_10  label="G4_NYLON-6-10"  # scripted group (container) (typed FeaturePython)
  Dunit = g/cm3
  Dvalue = 1.14
  Group = -> [H_element065,C_element071,N_element033,O_element073]
  conduct = 2
  density = 1
  expand = 3
  formula = G4_NYLON-6-10
  name = G4_NYLON-6-10
  specific = 4
FEATURE [App::DocumentObjectGroupPython] H_element066  label="H_element : 0.140"  # scripted group (container) (typed FeaturePython)
  n = 0.115476
FEATURE [App::DocumentObjectGroupPython] C_element072  label="C_element : 0.721"  # scripted group (container) (typed FeaturePython)
  n = 0.720818
FEATURE [App::DocumentObjectGroupPython] N_element034  label="N_element : 0.076"  # scripted group (container) (typed FeaturePython)
  n = 0.0764169
FEATURE [App::DocumentObjectGroupPython] O_element074  label="O_element : 0.087"  # scripted group (container) (typed FeaturePython)
  n = 0.0872889
FEATURE [App::DocumentObjectGroupPython] G4_NYLON_11_RILSAN  label="G4_NYLON-11_RILSAN"  # scripted group (container) (typed FeaturePython)
  Dunit = g/cm3
  Dvalue = 1.425
  Group = -> [H_element066,C_element072,N_element034,O_element074]
  conduct = 2
  density = 1
  expand = 3
  formula = G4_NYLON-11_RILSAN
  name = G4_NYLON-11_RILSAN
  specific = 4
FEATURE [App::DocumentObjectGroupPython] C_element073  label="C_element : 8"  # scripted group (container) (typed FeaturePython)
  n = 8
  ref = C_element
FEATURE [App::DocumentObjectGroupPython] H_element067  label="H_element : 18"  # scripted group (container) (typed FeaturePython)
  n = 18
  ref = H_element
FEATURE [App::DocumentObjectGroupPython] G4_OCTANE  # scripted group (container) (typed FeaturePython)
  Dunit = g/cm3
  Dvalue = 0.7026
  Group = -> [C_element073,H_element067]
  conduct = 2
  density = 1
  expand = 3
  formula = G4_OCTANE
  name = G4_OCTANE
  specific = 4
FEATURE [App::DocumentObjectGroupPython] C_element074  label="C_element : 25"  # scripted group (container) (typed FeaturePython)
  n = 25
  ref = C_element
FEATURE [App::DocumentObjectGroupPython] H_element068  label="H_element : 52"  # scripted group (container) (typed FeaturePython)
  n = 52
  ref = H_element
FEATURE [App::DocumentObjectGroupPython] G4_PARAFFIN  # scripted group (container) (typed FeaturePython)
  Dunit = g/cm3
  Dvalue = 0.93
  Group = -> [C_element074,H_element068]
  conduct = 2
  density = 1
  expand = 3
  formula = G4_PARAFFIN
  name = G4_PARAFFIN
  specific = 4
FEATURE [App::DocumentObjectGroupPython] C_element075  label="C_element : 036"  # scripted group (container) (typed FeaturePython)
  n = 5
  ref = C_element
FEATURE [App::DocumentObjectGroupPython] H_element069  label="H_element : 032"  # scripted group (container) (typed FeaturePython)
  n = 12
  ref = H_element
FEATURE [App::DocumentObjectGroupPython] G4_N_PENTANE  label="G4_N-PENTANE"  # scripted group (container) (typed FeaturePython)
  Dunit = g/cm3
  Dvalue = 0.6262
  Group = -> [C_element075,H_element069]
  conduct = 2
  density = 1
  expand = 3
  formula = G4_N-PENTANE
  name = G4_N-PENTANE
  specific = 4
FEATURE [App::DocumentObjectGroupPython] H_element070  label="H_element : 0.014"  # scripted group (container) (typed FeaturePython)
  n = 0.0141
FEATURE [App::DocumentObjectGroupPython] C_element076  label="C_element : 0.072"  # scripted group (container) (typed FeaturePython)
  n = 0.072261
FEATURE [App::DocumentObjectGroupPython] N_element035  label="N_element : 0.019"  # scripted group (container) (typed FeaturePython)
  n = 0.01932
FEATURE [App::DocumentObjectGroupPython] O_element075  label="O_element : 0.066"  # scripted group (container) (typed FeaturePython)
  n = 0.066101
FEATURE [App::DocumentObjectGroupPython] S_element019  label="S_element : 0.020"  # scripted group (container) (typed FeaturePython)
  n = 0.00189
FEATURE [App::DocumentObjectGroupPython] Br_element004  label="Br_element : 0.349"  # scripted group (container) (typed FeaturePython)
  n = 0.349103
FEATURE [App::DocumentObjectGroupPython] Ag_element001  label="Ag_element : 0.474"  # scripted group (container) (typed FeaturePython)
  n = 0.474105
FEATURE [App::DocumentObjectGroupPython] I_element005  label="I_element : 0.003"  # scripted group (container) (typed FeaturePython)
  n = 0.00312
FEATURE [App::DocumentObjectGroupPython] G4_PHOTO_EMULSION  # scripted group (container) (typed FeaturePython)
  Dunit = g/cm3
  Dvalue = 3.815
  Group = -> [H_element070,C_element076,N_element035,O_element075,S_element019,Br_element004,Ag_element001,I_element005]
  conduct = 2
  density = 1
  expand = 3
  formula = G4_PHOTO_EMULSION
  name = G4_PHOTO_EMULSION
  specific = 4
FEATURE [App::DocumentObjectGroupPython] C_element077  label="C_element : 9"  # scripted group (container) (typed FeaturePython)
  n = 9
  ref = C_element
FEATURE [App::DocumentObjectGroupPython] H_element071  label="H_element : 033"  # scripted group (container) (typed FeaturePython)
  n = 10
  ref = H_element
FEATURE [App::DocumentObjectGroupPython] G4_PLASTIC_SC_VINYLTOLUENE  # scripted group (container) (typed FeaturePython)
  Dunit = g/cm3
  Dvalue = 1.032
  Group = -> [C_element077,H_element071]
  conduct = 2
  density = 1
  expand = 3
  formula = G4_PLASTIC_SC_VINYLTOLUENE
  name = G4_PLASTIC_SC_VINYLTOLUENE
  specific = 4
FEATURE [App::DocumentObjectGroupPython] Pu_element001  label="Pu_element : 1"  # scripted group (container) (typed FeaturePython)
  n = 1
  ref = Pu_element
FEATURE [App::DocumentObjectGroupPython] O_element076  label="O_element : 037"  # scripted group (container) (typed FeaturePython)
  n = 2
  ref = O_element
FEATURE [App::DocumentObjectGroupPython] G4_PLUTONIUM_DIOXIDE  # scripted group (container) (typed FeaturePython)
  Dunit = g/cm3
  Dvalue = 11.46
  Group = -> [Pu_element001,O_element076]
  conduct = 2
  density = 1
  expand = 3
  formula = G4_PLUTONIUM_DIOXIDE
  name = G4_PLUTONIUM_DIOXIDE
  specific = 4
FEATURE [App::DocumentObjectGroupPython] C_element078  label="C_element : 037"  # scripted group (container) (typed FeaturePython)
  n = 3
  ref = C_element
FEATURE [App::DocumentObjectGroupPython] H_element072  label="H_element : 034"  # scripted group (container) (typed FeaturePython)
  n = 3
  ref = H_element
FEATURE [App::DocumentObjectGroupPython] N_element036  label="N_element : 015"  # scripted group (container) (typed FeaturePython)
  n = 1
  ref = N_element
FEATURE [App::DocumentObjectGroupPython] G4_POLYACRYLONITRILE  # scripted group (container) (typed FeaturePython)
  Dunit = g/cm3
  Dvalue = 1.17
  Group = -> [C_element078,H_element072,N_element036]
  conduct = 2
  density = 1
  expand = 3
  formula = G4_POLYACRYLONITRILE
  name = G4_POLYACRYLONITRILE
  specific = 4
FEATURE [App::DocumentObjectGroupPython] C_element079  label="C_element : 16"  # scripted group (container) (typed FeaturePython)
  n = 16
  ref = C_element
FEATURE [App::DocumentObjectGroupPython] H_element073  label="H_element : 035"  # scripted group (container) (typed FeaturePython)
  n = 14
  ref = H_element
FEATURE [App::DocumentObjectGroupPython] O_element077  label="O_element : 038"  # scripted group (container) (typed FeaturePython)
  n = 3
  ref = O_element
FEATURE [App::DocumentObjectGroupPython] G4_POLYCARBONATE  # scripted group (container) (typed FeaturePython)
  Dunit = g/cm3
  Dvalue = 1.2
  Group = -> [C_element079,H_element073,O_element077]
  conduct = 2
  density = 1
  expand = 3
  formula = G4_POLYCARBONATE
  name = G4_POLYCARBONATE
  specific = 4
FEATURE [App::DocumentObjectGroupPython] C_element080  label="C_element : 038"  # scripted group (container) (typed FeaturePython)
  n = 8
  ref = C_element
FEATURE [App::DocumentObjectGroupPython] H_element074  label="H_element : 036"  # scripted group (container) (typed FeaturePython)
  n = 7
  ref = H_element
FEATURE [App::DocumentObjectGroupPython] Cl_element017  label="Cl_element : 007"  # scripted group (container) (typed FeaturePython)
  n = 1
  ref = Cl_element
FEATURE [App::DocumentObjectGroupPython] G4_POLYCHLOROSTYRENE  # scripted group (container) (typed FeaturePython)
  Dunit = g/cm3
  Dvalue = 1.3
  Group = -> [C_element080,H_element074,Cl_element017]
  conduct = 2
  density = 1
  expand = 3
  formula = G4_POLYCHLOROSTYRENE
  name = G4_POLYCHLOROSTYRENE
  specific = 4
FEATURE [App::DocumentObjectGroupPython] C_element081  label="C_element : 039"  # scripted group (container) (typed FeaturePython)
  n = 1
  ref = C_element
FEATURE [App::DocumentObjectGroupPython] H_element075  label="H_element : 037"  # scripted group (container) (typed FeaturePython)
  n = 2
  ref = H_element
FEATURE [App::DocumentObjectGroupPython] G4_POLYETHYLENE  # scripted group (container) (typed FeaturePython)
  Dunit = g/cm3
  Dvalue = 0.94
  Group = -> [C_element081,H_element075]
  conduct = 2
  density = 1
  expand = 3
  formula = G4_POLYETHYLENE
  name = G4_POLYETHYLENE
  specific = 4
FEATURE [App::DocumentObjectGroupPython] C_element082  label="C_element : 040"  # scripted group (container) (typed FeaturePython)
  n = 10
  ref = C_element
FEATURE [App::DocumentObjectGroupPython] H_element076  label="H_element : 038"  # scripted group (container) (typed FeaturePython)
  n = 8
  ref = H_element
FEATURE [App::DocumentObjectGroupPython] O_element078  label="O_element : 039"  # scripted group (container) (typed FeaturePython)
  n = 4
  ref = O_element
FEATURE [App::DocumentObjectGroupPython] G4_MYLAR  # scripted group (container) (typed FeaturePython)
  Dunit = g/cm3
  Dvalue = 1.4
  Group = -> [C_element082,H_element076,O_element078]
  conduct = 2
  density = 1
  expand = 3
  formula = G4_MYLAR
  name = G4_MYLAR
  specific = 4
FEATURE [App::DocumentObjectGroupPython] C_element083  label="C_element : 041"  # scripted group (container) (typed FeaturePython)
  n = 5
  ref = C_element
FEATURE [App::DocumentObjectGroupPython] H_element077  label="H_element : 039"  # scripted group (container) (typed FeaturePython)
  n = 8
  ref = H_element
FEATURE [App::DocumentObjectGroupPython] O_element079  label="O_element : 040"  # scripted group (container) (typed FeaturePython)
  n = 2
  ref = O_element
FEATURE [App::DocumentObjectGroupPython] G4_PLEXIGLASS  # scripted group (container) (typed FeaturePython)
  Dunit = g/cm3
  Dvalue = 1.19
  Group = -> [C_element083,H_element077,O_element079]
  conduct = 2
  density = 1
  expand = 3
  formula = G4_PLEXIGLASS
  name = G4_PLEXIGLASS
  specific = 4
FEATURE [App::DocumentObjectGroupPython] C_element084  label="C_element : 042"  # scripted group (container) (typed FeaturePython)
  n = 1
  ref = C_element
FEATURE [App::DocumentObjectGroupPython] H_element078  label="H_element : 040"  # scripted group (container) (typed FeaturePython)
  n = 2
  ref = H_element
FEATURE [App::DocumentObjectGroupPython] O_element080  label="O_element : 041"  # scripted group (container) (typed FeaturePython)
  n = 1
  ref = O_element
FEATURE [App::DocumentObjectGroupPython] G4_POLYOXYMETHYLENE  # scripted group (container) (typed FeaturePython)
  Dunit = g/cm3
  Dvalue = 1.425
  Group = -> [C_element084,H_element078,O_element080]
  conduct = 2
  density = 1
  expand = 3
  formula = G4_POLYOXYMETHYLENE
  name = G4_POLYOXYMETHYLENE
  specific = 4
FEATURE [App::DocumentObjectGroupPython] C_element085  label="C_element : 043"  # scripted group (container) (typed FeaturePython)
  n = 2
  ref = C_element
FEATURE [App::DocumentObjectGroupPython] H_element079  label="H_element : 041"  # scripted group (container) (typed FeaturePython)
  n = 4
  ref = H_element
FEATURE [App::DocumentObjectGroupPython] G4_POLYPROPYLENE  # scripted group (container) (typed FeaturePython)
  Dunit = g/cm3
  Dvalue = 0.9
  Group = -> [C_element085,H_element079]
  conduct = 2
  density = 1
  expand = 3
  formula = G4_POLYPROPYLENE
  name = G4_POLYPROPYLENE
  specific = 4
FEATURE [App::DocumentObjectGroupPython] C_element086  label="C_element : 044"  # scripted group (container) (typed FeaturePython)
  n = 8
  ref = C_element
FEATURE [App::DocumentObjectGroupPython] H_element080  label="H_element : 042"  # scripted group (container) (typed FeaturePython)
  n = 8
  ref = H_element
FEATURE [App::DocumentObjectGroupPython] G4_POLYSTYRENE  # scripted group (container) (typed FeaturePython)
  Dunit = g/cm3
  Dvalue = 1.06
  Group = -> [C_element086,H_element080]
  conduct = 2
  density = 1
  expand = 3
  formula = G4_POLYSTYRENE
  name = G4_POLYSTYRENE
  specific = 4
FEATURE [App::DocumentObjectGroupPython] C_element087  label="C_element : 045"  # scripted group (container) (typed FeaturePython)
  n = 2
  ref = C_element
FEATURE [App::DocumentObjectGroupPython] F_element014  label="F_element : 4"  # scripted group (container) (typed FeaturePython)
  n = 4
  ref = F_element
FEATURE [App::DocumentObjectGroupPython] G4_TEFLON  # scripted group (container) (typed FeaturePython)
  Dunit = g/cm3
  Dvalue = 2.2
  Group = -> [C_element087,F_element014]
  conduct = 2
  density = 1
  expand = 3
  formula = G4_TEFLON
  name = G4_TEFLON
  specific = 4
FEATURE [App::DocumentObjectGroupPython] C_element088  label="C_element : 046"  # scripted group (container) (typed FeaturePython)
  n = 2
  ref = C_element
FEATURE [App::DocumentObjectGroupPython] F_element015  label="F_element : 006"  # scripted group (container) (typed FeaturePython)
  n = 3
  ref = F_element
FEATURE [App::DocumentObjectGroupPython] Cl_element018  label="Cl_element : 008"  # scripted group (container) (typed FeaturePython)
  n = 1
  ref = Cl_element
FEATURE [App::DocumentObjectGroupPython] G4_POLYTRIFLUOROCHLOROETHYLENE  # scripted group (container) (typed FeaturePython)
  Dunit = g/cm3
  Dvalue = 2.1
  Group = -> [C_element088,F_element015,Cl_element018]
  conduct = 2
  density = 1
  expand = 3
  formula = G4_POLYTRIFLUOROCHLOROETHYLENE
  name = G4_POLYTRIFLUOROCHLOROETHYLENE
  specific = 4
FEATURE [App::DocumentObjectGroupPython] C_element089  label="C_element : 047"  # scripted group (container) (typed FeaturePython)
  n = 4
  ref = C_element
FEATURE [App::DocumentObjectGroupPython] H_element081  label="H_element : 043"  # scripted group (container) (typed FeaturePython)
  n = 6
  ref = H_element
FEATURE [App::DocumentObjectGroupPython] O_element081  label="O_element : 042"  # scripted group (container) (typed FeaturePython)
  n = 2
  ref = O_element
FEATURE [App::DocumentObjectGroupPython] G4_POLYVINYL_ACETATE  # scripted group (container) (typed FeaturePython)
  Dunit = g/cm3
  Dvalue = 1.19
  Group = -> [C_element089,H_element081,O_element081]
  conduct = 2
  density = 1
  expand = 3
  formula = G4_POLYVINYL_ACETATE
  name = G4_POLYVINYL_ACETATE
  specific = 4
FEATURE [App::DocumentObjectGroupPython] C_element090  label="C_element : 048"  # scripted group (container) (typed FeaturePython)
  n = 2
  ref = C_element
FEATURE [App::DocumentObjectGroupPython] H_element082  label="H_element : 044"  # scripted group (container) (typed FeaturePython)
  n = 4
  ref = H_element
FEATURE [App::DocumentObjectGroupPython] O_element082  label="O_element : 043"  # scripted group (container) (typed FeaturePython)
  n = 1
  ref = O_element
FEATURE [App::DocumentObjectGroupPython] G4_POLYVINYL_ALCOHOL  # scripted group (container) (typed FeaturePython)
  Dunit = g/cm3
  Dvalue = 1.3
  Group = -> [C_element090,H_element082,O_element082]
  conduct = 2
  density = 1
  expand = 3
  formula = G4_POLYVINYL_ALCOHOL
  name = G4_POLYVINYL_ALCOHOL
  specific = 4
FEATURE [App::DocumentObjectGroupPython] C_element091  label="C_element : 049"  # scripted group (container) (typed FeaturePython)
  n = 8
  ref = C_element
FEATURE [App::DocumentObjectGroupPython] H_element083  label="H_element : 045"  # scripted group (container) (typed FeaturePython)
  n = 14
  ref = H_element
FEATURE [App::DocumentObjectGroupPython] O_element083  label="O_element : 044"  # scripted group (container) (typed FeaturePython)
  n = 2
  ref = O_element
FEATURE [App::DocumentObjectGroupPython] G4_POLYVINYL_BUTYRAL  # scripted group (container) (typed FeaturePython)
  Dunit = g/cm3
  Dvalue = 1.12
  Group = -> [C_element091,H_element083,O_element083]
  conduct = 2
  density = 1
  expand = 3
  formula = G4_POLYVINYL_BUTYRAL
  name = G4_POLYVINYL_BUTYRAL
  specific = 4
FEATURE [App::DocumentObjectGroupPython] C_element092  label="C_element : 050"  # scripted group (container) (typed FeaturePython)
  n = 2
  ref = C_element
FEATURE [App::DocumentObjectGroupPython] H_element084  label="H_element : 046"  # scripted group (container) (typed FeaturePython)
  n = 3
  ref = H_element
FEATURE [App::DocumentObjectGroupPython] Cl_element019  label="Cl_element : 009"  # scripted group (container) (typed FeaturePython)
  n = 1
  ref = Cl_element
FEATURE [App::DocumentObjectGroupPython] G4_POLYVINYL_CHLORIDE  # scripted group (container) (typed FeaturePython)
  Dunit = g/cm3
  Dvalue = 1.3
  Group = -> [C_element092,H_element084,Cl_element019]
  conduct = 2
  density = 1
  expand = 3
  formula = G4_POLYVINYL_CHLORIDE
  name = G4_POLYVINYL_CHLORIDE
  specific = 4
FEATURE [App::DocumentObjectGroupPython] C_element093  label="C_element : 051"  # scripted group (container) (typed FeaturePython)
  n = 2
  ref = C_element
FEATURE [App::DocumentObjectGroupPython] H_element085  label="H_element : 047"  # scripted group (container) (typed FeaturePython)
  n = 2
  ref = H_element
FEATURE [App::DocumentObjectGroupPython] Cl_element020  label="Cl_element : 010"  # scripted group (container) (typed FeaturePython)
  n = 2
  ref = Cl_element
FEATURE [App::DocumentObjectGroupPython] G4_POLYVINYLIDENE_CHLORIDE  # scripted group (container) (typed FeaturePython)
  Dunit = g/cm3
  Dvalue = 1.7
  Group = -> [C_element093,H_element085,Cl_element020]
  conduct = 2
  density = 1
  expand = 3
  formula = G4_POLYVINYLIDENE_CHLORIDE
  name = G4_POLYVINYLIDENE_CHLORIDE
  specific = 4
FEATURE [App::DocumentObjectGroupPython] C_element094  label="C_element : 052"  # scripted group (container) (typed FeaturePython)
  n = 2
  ref = C_element
FEATURE [App::DocumentObjectGroupPython] H_element086  label="H_element : 048"  # scripted group (container) (typed FeaturePython)
  n = 2
  ref = H_element
FEATURE [App::DocumentObjectGroupPython] F_element016  label="F_element : 007"  # scripted group (container) (typed FeaturePython)
  n = 2
  ref = F_element
FEATURE [App::DocumentObjectGroupPython] G4_POLYVINYLIDENE_FLUORIDE  # scripted group (container) (typed FeaturePython)
  Dunit = g/cm3
  Dvalue = 1.76
  Group = -> [C_element094,H_element086,F_element016]
  conduct = 2
  density = 1
  expand = 3
  formula = G4_POLYVINYLIDENE_FLUORIDE
  name = G4_POLYVINYLIDENE_FLUORIDE
  specific = 4
FEATURE [App::DocumentObjectGroupPython] C_element095  label="C_element : 053"  # scripted group (container) (typed FeaturePython)
  n = 6
  ref = C_element
FEATURE [App::DocumentObjectGroupPython] H_element087  label="H_element : 9"  # scripted group (container) (typed FeaturePython)
  n = 9
  ref = H_element
FEATURE [App::DocumentObjectGroupPython] N_element037  label="N_element : 016"  # scripted group (container) (typed FeaturePython)
  n = 1
  ref = N_element
FEATURE [App::DocumentObjectGroupPython] O_element084  label="O_element : 045"  # scripted group (container) (typed FeaturePython)
  n = 1
  ref = O_element
FEATURE [App::DocumentObjectGroupPython] G4_POLYVINYL_PYRROLIDONE  # scripted group (container) (typed FeaturePython)
  Dunit = g/cm3
  Dvalue = 1.25
  Group = -> [C_element095,H_element087,N_element037,O_element084]
  conduct = 2
  density = 1
  expand = 3
  formula = G4_POLYVINYL_PYRROLIDONE
  name = G4_POLYVINYL_PYRROLIDONE
  specific = 4
FEATURE [App::DocumentObjectGroupPython] K_element008  label="K_element : 1"  # scripted group (container) (typed FeaturePython)
  n = 1
  ref = K_element
FEATURE [App::DocumentObjectGroupPython] I_element006  label="I_element : 003"  # scripted group (container) (typed FeaturePython)
  n = 1
  ref = I_element
FEATURE [App::DocumentObjectGroupPython] G4_POTASSIUM_IODIDE  # scripted group (container) (typed FeaturePython)
  Dunit = g/cm3
  Dvalue = 3.13
  Group = -> [K_element008,I_element006]
  conduct = 2
  density = 1
  expand = 3
  formula = G4_POTASSIUM_IODIDE
  name = G4_POTASSIUM_IODIDE
  specific = 4
FEATURE [App::DocumentObjectGroupPython] K_element009  label="K_element : 2"  # scripted group (container) (typed FeaturePython)
  n = 2
  ref = K_element
FEATURE [App::DocumentObjectGroupPython] O_element085  label="O_element : 046"  # scripted group (container) (typed FeaturePython)
  n = 1
  ref = O_element
FEATURE [App::DocumentObjectGroupPython] G4_POTASSIUM_OXIDE  # scripted group (container) (typed FeaturePython)
  Dunit = g/cm3
  Dvalue = 2.32
  Group = -> [K_element009,O_element085]
  conduct = 2
  density = 1
  expand = 3
  formula = G4_POTASSIUM_OXIDE
  name = G4_POTASSIUM_OXIDE
  specific = 4
FEATURE [App::DocumentObjectGroupPython] C_element096  label="C_element : 054"  # scripted group (container) (typed FeaturePython)
  n = 3
  ref = C_element
FEATURE [App::DocumentObjectGroupPython] H_element088  label="H_element : 049"  # scripted group (container) (typed FeaturePython)
  n = 8
  ref = H_element
FEATURE [App::DocumentObjectGroupPython] G4_PROPANE  # scripted group (container) (typed FeaturePython)
  Dunit = g/cm3
  Dvalue = 0.00187939
  Group = -> [C_element096,H_element088]
  conduct = 2
  density = 1
  expand = 3
  formula = G4_PROPANE
  name = G4_PROPANE
  specific = 4
FEATURE [App::DocumentObjectGroupPython] C_element097  label="C_element : 055"  # scripted group (container) (typed FeaturePython)
  n = 3
  ref = C_element
FEATURE [App::DocumentObjectGroupPython] H_element089  label="H_element : 050"  # scripted group (container) (typed FeaturePython)
  n = 8
  ref = H_element
FEATURE [App::DocumentObjectGroupPython] G4_lPROPANE  # scripted group (container) (typed FeaturePython)
  Dunit = g/cm3
  Dvalue = 0.43
  Group = -> [C_element097,H_element089]
  conduct = 2
  density = 1
  expand = 3
  formula = G4_lPROPANE
  name = G4_lPROPANE
  specific = 4
FEATURE [App::DocumentObjectGroupPython] C_element098  label="C_element : 056"  # scripted group (container) (typed FeaturePython)
  n = 3
  ref = C_element
FEATURE [App::DocumentObjectGroupPython] H_element090  label="H_element : 051"  # scripted group (container) (typed FeaturePython)
  n = 8
  ref = H_element
FEATURE [App::DocumentObjectGroupPython] O_element086  label="O_element : 047"  # scripted group (container) (typed FeaturePython)
  n = 1
  ref = O_element
FEATURE [App::DocumentObjectGroupPython] G4_N_PROPYL_ALCOHOL  label="G4_N-PROPYL_ALCOHOL"  # scripted group (container) (typed FeaturePython)
  Dunit = g/cm3
  Dvalue = 0.8035
  Group = -> [C_element098,H_element090,O_element086]
  conduct = 2
  density = 1
  expand = 3
  formula = G4_N-PROPYL_ALCOHOL
  name = G4_N-PROPYL_ALCOHOL
  specific = 4
FEATURE [App::DocumentObjectGroupPython] C_element099  label="C_element : 057"  # scripted group (container) (typed FeaturePython)
  n = 5
  ref = C_element
FEATURE [App::DocumentObjectGroupPython] H_element091  label="H_element : 052"  # scripted group (container) (typed FeaturePython)
  n = 5
  ref = H_element
FEATURE [App::DocumentObjectGroupPython] N_element038  label="N_element : 017"  # scripted group (container) (typed FeaturePython)
  n = 1
  ref = N_element
FEATURE [App::DocumentObjectGroupPython] G4_PYRIDINE  # scripted group (container) (typed FeaturePython)
  Dunit = g/cm3
  Dvalue = 0.9819
  Group = -> [C_element099,H_element091,N_element038]
  conduct = 2
  density = 1
  expand = 3
  formula = G4_PYRIDINE
  name = G4_PYRIDINE
  specific = 4
FEATURE [App::DocumentObjectGroupPython] H_element092  label="H_element : 0.144"  # scripted group (container) (typed FeaturePython)
  n = 0.143711
FEATURE [App::DocumentObjectGroupPython] C_element100  label="C_element : 0.856"  # scripted group (container) (typed FeaturePython)
  n = 0.856289
FEATURE [App::DocumentObjectGroupPython] G4_RUBBER_BUTYL  # scripted group (container) (typed FeaturePython)
  Dunit = g/cm3
  Dvalue = 0.92
  Group = -> [H_element092,C_element100]
  conduct = 2
  density = 1
  expand = 3
  formula = G4_RUBBER_BUTYL
  name = G4_RUBBER_BUTYL
  specific = 4
FEATURE [App::DocumentObjectGroupPython] H_element093  label="H_element : 0.118"  # scripted group (container) (typed FeaturePython)
  n = 0.118371
FEATURE [App::DocumentObjectGroupPython] C_element101  label="C_element : 0.882"  # scripted group (container) (typed FeaturePython)
  n = 0.881629
FEATURE [App::DocumentObjectGroupPython] G4_RUBBER_NATURAL  # scripted group (container) (typed FeaturePython)
  Dunit = g/cm3
  Dvalue = 0.92
  Group = -> [H_element093,C_element101]
  conduct = 2
  density = 1
  expand = 3
  formula = G4_RUBBER_NATURAL
  name = G4_RUBBER_NATURAL
  specific = 4
FEATURE [App::DocumentObjectGroupPython] H_element094  label="H_element : 0.145"  # scripted group (container) (typed FeaturePython)
  n = 0.05692
FEATURE [App::DocumentObjectGroupPython] C_element102  label="C_element : 0.543"  # scripted group (container) (typed FeaturePython)
  n = 0.542646
FEATURE [App::DocumentObjectGroupPython] Cl_element021  label="Cl_element : 0.400"  # scripted group (container) (typed FeaturePython)
  n = 0.400434
FEATURE [App::DocumentObjectGroupPython] G4_RUBBER_NEOPRENE  # scripted group (container) (typed FeaturePython)
  Dunit = g/cm3
  Dvalue = 1.23
  Group = -> [H_element094,C_element102,Cl_element021]
  conduct = 2
  density = 1
  expand = 3
  formula = G4_RUBBER_NEOPRENE
  name = G4_RUBBER_NEOPRENE
  specific = 4
FEATURE [App::DocumentObjectGroupPython] Si_element006  label="Si_element : 1"  # scripted group (container) (typed FeaturePython)
  n = 1
  ref = Si_element
FEATURE [App::DocumentObjectGroupPython] O_element087  label="O_element : 048"  # scripted group (container) (typed FeaturePython)
  n = 2
  ref = O_element
FEATURE [App::DocumentObjectGroupPython] G4_SILICON_DIOXIDE  # scripted group (container) (typed FeaturePython)
  Dunit = g/cm3
  Dvalue = 2.32
  Group = -> [Si_element006,O_element087]
  conduct = 2
  density = 1
  expand = 3
  formula = G4_SILICON_DIOXIDE
  name = G4_SILICON_DIOXIDE
  specific = 4
FEATURE [App::DocumentObjectGroupPython] Ag_element002  label="Ag_element : 1"  # scripted group (container) (typed FeaturePython)
  n = 1
  ref = Ag_element
FEATURE [App::DocumentObjectGroupPython] Br_element005  label="Br_element : 003"  # scripted group (container) (typed FeaturePython)
  n = 1
  ref = Br_element
FEATURE [App::DocumentObjectGroupPython] G4_SILVER_BROMIDE  # scripted group (container) (typed FeaturePython)
  Dunit = g/cm3
  Dvalue = 6.473
  Group = -> [Ag_element002,Br_element005]
  conduct = 2
  density = 1
  expand = 3
  formula = G4_SILVER_BROMIDE
  name = G4_SILVER_BROMIDE
  specific = 4
FEATURE [App::DocumentObjectGroupPython] Ag_element003  label="Ag_element : 002"  # scripted group (container) (typed FeaturePython)
  n = 1
  ref = Ag_element
FEATURE [App::DocumentObjectGroupPython] Cl_element022  label="Cl_element : 011"  # scripted group (container) (typed FeaturePython)
  n = 1
  ref = Cl_element
FEATURE [App::DocumentObjectGroupPython] G4_SILVER_CHLORIDE  # scripted group (container) (typed FeaturePython)
  Dunit = g/cm3
  Dvalue = 5.56
  Group = -> [Ag_element003,Cl_element022]
  conduct = 2
  density = 1
  expand = 3
  formula = G4_SILVER_CHLORIDE
  name = G4_SILVER_CHLORIDE
  specific = 4
FEATURE [App::DocumentObjectGroupPython] Br_element006  label="Br_element : 0.423"  # scripted group (container) (typed FeaturePython)
  n = 0.422895
FEATURE [App::DocumentObjectGroupPython] Ag_element004  label="Ag_element : 0.574"  # scripted group (container) (typed FeaturePython)
  n = 0.573748
FEATURE [App::DocumentObjectGroupPython] I_element007  label="I_element : 0.649"  # scripted group (container) (typed FeaturePython)
  n = 0.003357
FEATURE [App::DocumentObjectGroupPython] G4_SILVER_HALIDES  # scripted group (container) (typed FeaturePython)
  Dunit = g/cm3
  Dvalue = 6.47
  Group = -> [Br_element006,Ag_element004,I_element007]
  conduct = 2
  density = 1
  expand = 3
  formula = G4_SILVER_HALIDES
  name = G4_SILVER_HALIDES
  specific = 4
FEATURE [App::DocumentObjectGroupPython] Ag_element005  label="Ag_element : 003"  # scripted group (container) (typed FeaturePython)
  n = 1
  ref = Ag_element
FEATURE [App::DocumentObjectGroupPython] I_element008  label="I_element : 004"  # scripted group (container) (typed FeaturePython)
  n = 1
  ref = I_element
FEATURE [App::DocumentObjectGroupPython] G4_SILVER_IODIDE  # scripted group (container) (typed FeaturePython)
  Dunit = g/cm3
  Dvalue = 6.01
  Group = -> [Ag_element005,I_element008]
  conduct = 2
  density = 1
  expand = 3
  formula = G4_SILVER_IODIDE
  name = G4_SILVER_IODIDE
  specific = 4
FEATURE [App::DocumentObjectGroupPython] H_element095  label="H_element : 0.100"  # scripted group (container) (typed FeaturePython)
  n = 0.1
FEATURE [App::DocumentObjectGroupPython] C_element103  label="C_element : 0.204"  # scripted group (container) (typed FeaturePython)
  n = 0.204
FEATURE [App::DocumentObjectGroupPython] N_element039  label="N_element : 0.759"  # scripted group (container) (typed FeaturePython)
  n = 0.042
FEATURE [App::DocumentObjectGroupPython] O_element088  label="O_element : 0.645"  # scripted group (container) (typed FeaturePython)
  n = 0.645
FEATURE [App::DocumentObjectGroupPython] Na_element013  label="Na_element : 0.100"  # scripted group (container) (typed FeaturePython)
  n = 0.002
FEATURE [App::DocumentObjectGroupPython] P_element009  label="P_element : 0.107"  # scripted group (container) (typed FeaturePython)
  n = 0.001
FEATURE [App::DocumentObjectGroupPython] S_element020  label="S_element : 0.021"  # scripted group (container) (typed FeaturePython)
  n = 0.002
FEATURE [App::DocumentObjectGroupPython] Cl_element023  label="Cl_element : 0.590"  # scripted group (container) (typed FeaturePython)
  n = 0.003
FEATURE [App::DocumentObjectGroupPython] K_element010  label="K_element : 0.001"  # scripted group (container) (typed FeaturePython)
  n = 0.001
FEATURE [App::DocumentObjectGroupPython] G4_SKIN_ICRP  # scripted group (container) (typed FeaturePython)
  Dunit = g/cm3
  Dvalue = 1.09
  Group = -> [H_element095,C_element103,N_element039,O_element088,Na_element013,P_element009,S_element020,Cl_element023,K_element010]
  conduct = 2
  density = 1
  expand = 3
  formula = G4_SKIN_ICRP
  name = G4_SKIN_ICRP
  specific = 4
FEATURE [App::DocumentObjectGroupPython] Na_element014  label="Na_element : 2"  # scripted group (container) (typed FeaturePython)
  n = 2
  ref = Na_element
FEATURE [App::DocumentObjectGroupPython] C_element104  label="C_element : 058"  # scripted group (container) (typed FeaturePython)
  n = 1
  ref = C_element
FEATURE [App::DocumentObjectGroupPython] O_element089  label="O_element : 049"  # scripted group (container) (typed FeaturePython)
  n = 3
  ref = O_element
FEATURE [App::DocumentObjectGroupPython] G4_SODIUM_CARBONATE  # scripted group (container) (typed FeaturePython)
  Dunit = g/cm3
  Dvalue = 2.532
  Group = -> [Na_element014,C_element104,O_element089]
  conduct = 2
  density = 1
  expand = 3
  formula = G4_SODIUM_CARBONATE
  name = G4_SODIUM_CARBONATE
  specific = 4
FEATURE [App::DocumentObjectGroupPython] Na_element015  label="Na_element : 1"  # scripted group (container) (typed FeaturePython)
  n = 1
  ref = Na_element
FEATURE [App::DocumentObjectGroupPython] I_element009  label="I_element : 005"  # scripted group (container) (typed FeaturePython)
  n = 1
  ref = I_element
FEATURE [App::DocumentObjectGroupPython] G4_SODIUM_IODIDE  # scripted group (container) (typed FeaturePython)
  Dunit = g/cm3
  Dvalue = 3.667
  Group = -> [Na_element015,I_element009]
  conduct = 2
  density = 1
  expand = 3
  formula = G4_SODIUM_IODIDE
  name = G4_SODIUM_IODIDE
  specific = 4
FEATURE [App::DocumentObjectGroupPython] Na_element016  label="Na_element : 003"  # scripted group (container) (typed FeaturePython)
  n = 2
  ref = Na_element
FEATURE [App::DocumentObjectGroupPython] O_element090  label="O_element : 050"  # scripted group (container) (typed FeaturePython)
  n = 1
  ref = O_element
FEATURE [App::DocumentObjectGroupPython] G4_SODIUM_MONOXIDE  # scripted group (container) (typed FeaturePython)
  Dunit = g/cm3
  Dvalue = 2.27
  Group = -> [Na_element016,O_element090]
  conduct = 2
  density = 1
  expand = 3
  formula = G4_SODIUM_MONOXIDE
  name = G4_SODIUM_MONOXIDE
  specific = 4
FEATURE [App::DocumentObjectGroupPython] Na_element017  label="Na_element : 004"  # scripted group (container) (typed FeaturePython)
  n = 1
  ref = Na_element
FEATURE [App::DocumentObjectGroupPython] N_element040  label="N_element : 018"  # scripted group (container) (typed FeaturePython)
  n = 1
  ref = N_element
FEATURE [App::DocumentObjectGroupPython] O_element091  label="O_element : 051"  # scripted group (container) (typed FeaturePython)
  n = 3
  ref = O_element
FEATURE [App::DocumentObjectGroupPython] G4_SODIUM_NITRATE  # scripted group (container) (typed FeaturePython)
  Dunit = g/cm3
  Dvalue = 2.261
  Group = -> [Na_element017,N_element040,O_element091]
  conduct = 2
  density = 1
  expand = 3
  formula = G4_SODIUM_NITRATE
  name = G4_SODIUM_NITRATE
  specific = 4
FEATURE [App::DocumentObjectGroupPython] C_element105  label="C_element : 059"  # scripted group (container) (typed FeaturePython)
  n = 14
  ref = C_element
FEATURE [App::DocumentObjectGroupPython] H_element096  label="H_element : 053"  # scripted group (container) (typed FeaturePython)
  n = 12
  ref = H_element
FEATURE [App::DocumentObjectGroupPython] G4_STILBENE  # scripted group (container) (typed FeaturePython)
  Dunit = g/cm3
  Dvalue = 0.9707
  Group = -> [C_element105,H_element096]
  conduct = 2
  density = 1
  expand = 3
  formula = G4_STILBENE
  name = G4_STILBENE
  specific = 4
FEATURE [App::DocumentObjectGroupPython] C_element106  label="C_element : 12"  # scripted group (container) (typed FeaturePython)
  n = 12
  ref = C_element
FEATURE [App::DocumentObjectGroupPython] H_element097  label="H_element : 22"  # scripted group (container) (typed FeaturePython)
  n = 22
  ref = H_element
FEATURE [App::DocumentObjectGroupPython] O_element092  label="O_element : 11"  # scripted group (container) (typed FeaturePython)
  n = 11
  ref = O_element
FEATURE [App::DocumentObjectGroupPython] G4_SUCROSE  # scripted group (container) (typed FeaturePython)
  Dunit = g/cm3
  Dvalue = 1.5805
  Group = -> [C_element106,H_element097,O_element092]
  conduct = 2
  density = 1
  expand = 3
  formula = G4_SUCROSE
  name = G4_SUCROSE
  specific = 4
FEATURE [App::DocumentObjectGroupPython] C_element107  label="C_element : 18"  # scripted group (container) (typed FeaturePython)
  n = 18
  ref = C_element
FEATURE [App::DocumentObjectGroupPython] H_element098  label="H_element : 054"  # scripted group (container) (typed FeaturePython)
  n = 14
  ref = H_element
FEATURE [App::DocumentObjectGroupPython] G4_TERPHENYL  # scripted group (container) (typed FeaturePython)
  Dunit = g/cm3
  Dvalue = 1.24
  Group = -> [C_element107,H_element098]
  conduct = 2
  density = 1
  expand = 3
  formula = G4_TERPHENYL
  name = G4_TERPHENYL
  specific = 4
FEATURE [App::DocumentObjectGroupPython] H_element099  label="H_element : 0.146"  # scripted group (container) (typed FeaturePython)
  n = 0.106
FEATURE [App::DocumentObjectGroupPython] C_element108  label="C_element : 0.883"  # scripted group (container) (typed FeaturePython)
  n = 0.099
FEATURE [App::DocumentObjectGroupPython] N_element041  label="N_element : 0.020"  # scripted group (container) (typed FeaturePython)
  n = 0.02
FEATURE [App::DocumentObjectGroupPython] O_element093  label="O_element : 0.766"  # scripted group (container) (typed FeaturePython)
  n = 0.766
FEATURE [App::DocumentObjectGroupPython] Na_element018  label="Na_element : 0.101"  # scripted group (container) (typed FeaturePython)
  n = 0.002
FEATURE [App::DocumentObjectGroupPython] P_element010  label="P_element : 0.108"  # scripted group (container) (typed FeaturePython)
  n = 0.001
FEATURE [App::DocumentObjectGroupPython] S_element021  label="S_element : 0.022"  # scripted group (container) (typed FeaturePython)
  n = 0.002
FEATURE [App::DocumentObjectGroupPython] Cl_element024  label="Cl_element : 0.002"  # scripted group (container) (typed FeaturePython)
  n = 0.002
FEATURE [App::DocumentObjectGroupPython] K_element011  label="K_element : 0.017"  # scripted group (container) (typed FeaturePython)
  n = 0.002
FEATURE [App::DocumentObjectGroupPython] G4_TESTIS_ICRP  # scripted group (container) (typed FeaturePython)
  Dunit = g/cm3
  Dvalue = 1.04
  Group = -> [H_element099,C_element108,N_element041,O_element093,Na_element018,P_element010,S_element021,Cl_element024,K_element011]
  conduct = 2
  density = 1
  expand = 3
  formula = G4_TESTIS_ICRP
  name = G4_TESTIS_ICRP
  specific = 4
FEATURE [App::DocumentObjectGroupPython] C_element109  label="C_element : 060"  # scripted group (container) (typed FeaturePython)
  n = 2
  ref = C_element
FEATURE [App::DocumentObjectGroupPython] Cl_element025  label="Cl_element : 012"  # scripted group (container) (typed FeaturePython)
  n = 4
  ref = Cl_element
FEATURE [App::DocumentObjectGroupPython] G4_TETRACHLOROETHYLENE  # scripted group (container) (typed FeaturePython)
  Dunit = g/cm3
  Dvalue = 1.625
  Group = -> [C_element109,Cl_element025]
  conduct = 2
  density = 1
  expand = 3
  formula = G4_TETRACHLOROETHYLENE
  name = G4_TETRACHLOROETHYLENE
  specific = 4
FEATURE [App::DocumentObjectGroupPython] Tl_element001  label="Tl_element : 1"  # scripted group (container) (typed FeaturePython)
  n = 1
  ref = Tl_element
FEATURE [App::DocumentObjectGroupPython] Cl_element026  label="Cl_element : 013"  # scripted group (container) (typed FeaturePython)
  n = 1
  ref = Cl_element
FEATURE [App::DocumentObjectGroupPython] G4_THALLIUM_CHLORIDE  # scripted group (container) (typed FeaturePython)
  Dunit = g/cm3
  Dvalue = 7.004
  Group = -> [Tl_element001,Cl_element026]
  conduct = 2
  density = 1
  expand = 3
  formula = G4_THALLIUM_CHLORIDE
  name = G4_THALLIUM_CHLORIDE
  specific = 4
FEATURE [App::DocumentObjectGroupPython] H_element100  label="H_element : 0.147"  # scripted group (container) (typed FeaturePython)
  n = 0.105
FEATURE [App::DocumentObjectGroupPython] C_element110  label="C_element : 0.256"  # scripted group (container) (typed FeaturePython)
  n = 0.256
FEATURE [App::DocumentObjectGroupPython] N_element042  label="N_element : 0.760"  # scripted group (container) (typed FeaturePython)
  n = 0.027
FEATURE [App::DocumentObjectGroupPython] O_element094  label="O_element : 0.602"  # scripted group (container) (typed FeaturePython)
  n = 0.602
FEATURE [App::DocumentObjectGroupPython] Na_element019  label="Na_element : 0.102"  # scripted group (container) (typed FeaturePython)
  n = 0.001
FEATURE [App::DocumentObjectGroupPython] P_element011  label="P_element : 0.109"  # scripted group (container) (typed FeaturePython)
  n = 0.002
FEATURE [App::DocumentObjectGroupPython] S_element022  label="S_element : 0.023"  # scripted group (container) (typed FeaturePython)
  n = 0.003
FEATURE [App::DocumentObjectGroupPython] Cl_element027  label="Cl_element : 0.591"  # scripted group (container) (typed FeaturePython)
  n = 0.002
FEATURE [App::DocumentObjectGroupPython] K_element012  label="K_element : 0.018"  # scripted group (container) (typed FeaturePython)
  n = 0.002
FEATURE [App::DocumentObjectGroupPython] G4_TISSUE_SOFT_ICRP  # scripted group (container) (typed FeaturePython)
  Dunit = g/cm3
  Dvalue = 1.03
  Group = -> [H_element100,C_element110,N_element042,O_element094,Na_element019,P_element011,S_element022,Cl_element027,K_element012]
  conduct = 2
  density = 1
  expand = 3
  formula = G4_TISSUE_SOFT_ICRP
  name = G4_TISSUE_SOFT_ICRP
  specific = 4
FEATURE [App::DocumentObjectGroupPython] H_element101  label="H_element : 0.148"  # scripted group (container) (typed FeaturePython)
  n = 0.101
FEATURE [App::DocumentObjectGroupPython] C_element111  label="C_element : 0.111"  # scripted group (container) (typed FeaturePython)
  n = 0.111
FEATURE [App::DocumentObjectGroupPython] N_element043  label="N_element : 0.026"  # scripted group (container) (typed FeaturePython)
  n = 0.026
FEATURE [App::DocumentObjectGroupPython] O_element095  label="O_element : 0.762"  # scripted group (container) (typed FeaturePython)
  n = 0.762
FEATURE [App::DocumentObjectGroupPython] G4_TISSUE_SOFT_ICRU_4  label="G4_TISSUE_SOFT_ICRU-4"  # scripted group (container) (typed FeaturePython)
  Dunit = g/cm3
  Dvalue = 1
  Group = -> [H_element101,C_element111,N_element043,O_element095]
  conduct = 2
  density = 1
  expand = 3
  formula = G4_TISSUE_SOFT_ICRU-4
  name = G4_TISSUE_SOFT_ICRU-4
  specific = 4
FEATURE [App::DocumentObjectGroupPython] H_element102  label="H_element : 0.149"  # scripted group (container) (typed FeaturePython)
  n = 0.101869
FEATURE [App::DocumentObjectGroupPython] C_element112  label="C_element : 0.456"  # scripted group (container) (typed FeaturePython)
  n = 0.456179
FEATURE [App::DocumentObjectGroupPython] N_element044  label="N_element : 0.761"  # scripted group (container) (typed FeaturePython)
  n = 0.035172
FEATURE [App::DocumentObjectGroupPython] O_element096  label="O_element : 0.407"  # scripted group (container) (typed FeaturePython)
  n = 0.40678
FEATURE [App::DocumentObjectGroupPython] G4_TISSUE_METHANE  label="G4_TISSUE-METHANE"  # scripted group (container) (typed FeaturePython)
  Dunit = g/cm3
  Dvalue = 0.00106409
  Group = -> [H_element102,C_element112,N_element044,O_element096]
  conduct = 2
  density = 1
  expand = 3
  formula = G4_TISSUE-METHANE
  name = G4_TISSUE-METHANE
  specific = 4
FEATURE [App::DocumentObjectGroupPython] H_element103  label="H_element : 0.103"  # scripted group (container) (typed FeaturePython)
  n = 0.102672
FEATURE [App::DocumentObjectGroupPython] C_element113  label="C_element : 0.569"  # scripted group (container) (typed FeaturePython)
  n = 0.56894
FEATURE [App::DocumentObjectGroupPython] N_element045  label="N_element : 0.762"  # scripted group (container) (typed FeaturePython)
  n = 0.035022
FEATURE [App::DocumentObjectGroupPython] O_element097  label="O_element : 0.293"  # scripted group (container) (typed FeaturePython)
  n = 0.293366
FEATURE [App::DocumentObjectGroupPython] G4_TISSUE_PROPANE  label="G4_TISSUE-PROPANE"  # scripted group (container) (typed FeaturePython)
  Dunit = g/cm3
  Dvalue = 0.00182628
  Group = -> [H_element103,C_element113,N_element045,O_element097]
  conduct = 2
  density = 1
  expand = 3
  formula = G4_TISSUE-PROPANE
  name = G4_TISSUE-PROPANE
  specific = 4
FEATURE [App::DocumentObjectGroupPython] Ti_element003  label="Ti_element : 1"  # scripted group (container) (typed FeaturePython)
  n = 1
  ref = Ti_element
FEATURE [App::DocumentObjectGroupPython] O_element098  label="O_element : 052"  # scripted group (container) (typed FeaturePython)
  n = 2
  ref = O_element
FEATURE [App::DocumentObjectGroupPython] G4_TITANIUM_DIOXIDE  # scripted group (container) (typed FeaturePython)
  Dunit = g/cm3
  Dvalue = 4.26
  Group = -> [Ti_element003,O_element098]
  conduct = 2
  density = 1
  expand = 3
  formula = G4_TITANIUM_DIOXIDE
  name = G4_TITANIUM_DIOXIDE
  specific = 4
FEATURE [App::DocumentObjectGroupPython] C_element114  label="C_element : 061"  # scripted group (container) (typed FeaturePython)
  n = 7
  ref = C_element
FEATURE [App::DocumentObjectGroupPython] H_element104  label="H_element : 055"  # scripted group (container) (typed FeaturePython)
  n = 8
  ref = H_element
FEATURE [App::DocumentObjectGroupPython] G4_TOLUENE  # scripted group (container) (typed FeaturePython)
  Dunit = g/cm3
  Dvalue = 0.8669
  Group = -> [C_element114,H_element104]
  conduct = 2
  density = 1
  expand = 3
  formula = G4_TOLUENE
  name = G4_TOLUENE
  specific = 4
FEATURE [App::DocumentObjectGroupPython] C_element115  label="C_element : 062"  # scripted group (container) (typed FeaturePython)
  n = 2
  ref = C_element
FEATURE [App::DocumentObjectGroupPython] H_element105  label="H_element : 056"  # scripted group (container) (typed FeaturePython)
  n = 1
  ref = H_element
FEATURE [App::DocumentObjectGroupPython] Cl_element028  label="Cl_element : 014"  # scripted group (container) (typed FeaturePython)
  n = 3
  ref = Cl_element
FEATURE [App::DocumentObjectGroupPython] G4_TRICHLOROETHYLENE  # scripted group (container) (typed FeaturePython)
  Dunit = g/cm3
  Dvalue = 1.46
  Group = -> [C_element115,H_element105,Cl_element028]
  conduct = 2
  density = 1
  expand = 3
  formula = G4_TRICHLOROETHYLENE
  name = G4_TRICHLOROETHYLENE
  specific = 4
FEATURE [App::DocumentObjectGroupPython] C_element116  label="C_element : 063"  # scripted group (container) (typed FeaturePython)
  n = 6
  ref = C_element
FEATURE [App::DocumentObjectGroupPython] H_element106  label="H_element : 15"  # scripted group (container) (typed FeaturePython)
  n = 15
  ref = H_element
FEATURE [App::DocumentObjectGroupPython] O_element099  label="O_element : 053"  # scripted group (container) (typed FeaturePython)
  n = 4
  ref = O_element
FEATURE [App::DocumentObjectGroupPython] P_element012  label="P_element : 1"  # scripted group (container) (typed FeaturePython)
  n = 1
  ref = P_element
FEATURE [App::DocumentObjectGroupPython] G4_TRIETHYL_PHOSPHATE  # scripted group (container) (typed FeaturePython)
  Dunit = g/cm3
  Dvalue = 1.07
  Group = -> [C_element116,H_element106,O_element099,P_element012]
  conduct = 2
  density = 1
  expand = 3
  formula = G4_TRIETHYL_PHOSPHATE
  name = G4_TRIETHYL_PHOSPHATE
  specific = 4
FEATURE [App::DocumentObjectGroupPython] W_element003  label="W_element : 003"  # scripted group (container) (typed FeaturePython)
  n = 1
  ref = W_element
FEATURE [App::DocumentObjectGroupPython] F_element017  label="F_element : 6"  # scripted group (container) (typed FeaturePython)
  n = 6
  ref = F_element
FEATURE [App::DocumentObjectGroupPython] G4_TUNGSTEN_HEXAFLUORIDE  # scripted group (container) (typed FeaturePython)
  Dunit = g/cm3
  Dvalue = 2.4
  Group = -> [W_element003,F_element017]
  conduct = 2
  density = 1
  expand = 3
  formula = G4_TUNGSTEN_HEXAFLUORIDE
  name = G4_TUNGSTEN_HEXAFLUORIDE
  specific = 4
FEATURE [App::DocumentObjectGroupPython] U_element001  label="U_element : 1"  # scripted group (container) (typed FeaturePython)
  n = 1
  ref = U_element
FEATURE [App::DocumentObjectGroupPython] C_element117  label="C_element : 064"  # scripted group (container) (typed FeaturePython)
  n = 2
  ref = C_element
FEATURE [App::DocumentObjectGroupPython] G4_URANIUM_DICARBIDE  # scripted group (container) (typed FeaturePython)
  Dunit = g/cm3
  Dvalue = 11.28
  Group = -> [U_element001,C_element117]
  conduct = 2
  density = 1
  expand = 3
  formula = G4_URANIUM_DICARBIDE
  name = G4_URANIUM_DICARBIDE
  specific = 4
FEATURE [App::DocumentObjectGroupPython] U_element002  label="U_element : 002"  # scripted group (container) (typed FeaturePython)
  n = 1
  ref = U_element
FEATURE [App::DocumentObjectGroupPython] C_element118  label="C_element : 065"  # scripted group (container) (typed FeaturePython)
  n = 1
  ref = C_element
FEATURE [App::DocumentObjectGroupPython] G4_URANIUM_MONOCARBIDE  # scripted group (container) (typed FeaturePython)
  Dunit = g/cm3
  Dvalue = 13.63
  Group = -> [U_element002,C_element118]
  conduct = 2
  density = 1
  expand = 3
  formula = G4_URANIUM_MONOCARBIDE
  name = G4_URANIUM_MONOCARBIDE
  specific = 4
FEATURE [App::DocumentObjectGroupPython] U_element003  label="U_element : 003"  # scripted group (container) (typed FeaturePython)
  n = 1
  ref = U_element
FEATURE [App::DocumentObjectGroupPython] O_element100  label="O_element : 054"  # scripted group (container) (typed FeaturePython)
  n = 2
  ref = O_element
FEATURE [App::DocumentObjectGroupPython] G4_URANIUM_OXIDE  # scripted group (container) (typed FeaturePython)
  Dunit = g/cm3
  Dvalue = 10.96
  Group = -> [U_element003,O_element100]
  conduct = 2
  density = 1
  expand = 3
  formula = G4_URANIUM_OXIDE
  name = G4_URANIUM_OXIDE
  specific = 4
FEATURE [App::DocumentObjectGroupPython] C_element119  label="C_element : 066"  # scripted group (container) (typed FeaturePython)
  n = 1
  ref = C_element
FEATURE [App::DocumentObjectGroupPython] H_element107  label="H_element : 057"  # scripted group (container) (typed FeaturePython)
  n = 4
  ref = H_element
FEATURE [App::DocumentObjectGroupPython] N_element046  label="N_element : 019"  # scripted group (container) (typed FeaturePython)
  n = 2
  ref = N_element
FEATURE [App::DocumentObjectGroupPython] O_element101  label="O_element : 055"  # scripted group (container) (typed FeaturePython)
  n = 1
  ref = O_element
FEATURE [App::DocumentObjectGroupPython] G4_UREA  # scripted group (container) (typed FeaturePython)
  Dunit = g/cm3
  Dvalue = 1.323
  Group = -> [C_element119,H_element107,N_element046,O_element101]
  conduct = 2
  density = 1
  expand = 3
  formula = G4_UREA
  name = G4_UREA
  specific = 4
FEATURE [App::DocumentObjectGroupPython] C_element120  label="C_element : 067"  # scripted group (container) (typed FeaturePython)
  n = 5
  ref = C_element
FEATURE [App::DocumentObjectGroupPython] H_element108  label="H_element : 058"  # scripted group (container) (typed FeaturePython)
  n = 11
  ref = H_element
FEATURE [App::DocumentObjectGroupPython] N_element047  label="N_element : 020"  # scripted group (container) (typed FeaturePython)
  n = 1
  ref = N_element
FEATURE [App::DocumentObjectGroupPython] O_element102  label="O_element : 056"  # scripted group (container) (typed FeaturePython)
  n = 2
  ref = O_element
FEATURE [App::DocumentObjectGroupPython] G4_VALINE  # scripted group (container) (typed FeaturePython)
  Dunit = g/cm3
  Dvalue = 1.23
  Group = -> [C_element120,H_element108,N_element047,O_element102]
  conduct = 2
  density = 1
  expand = 3
  formula = G4_VALINE
  name = G4_VALINE
  specific = 4
FEATURE [App::DocumentObjectGroupPython] H_element109  label="H_element : 0.009"  # scripted group (container) (typed FeaturePython)
  n = 0.009417
FEATURE [App::DocumentObjectGroupPython] C_element121  label="C_element : 0.281"  # scripted group (container) (typed FeaturePython)
  n = 0.280555
FEATURE [App::DocumentObjectGroupPython] F_element018  label="F_element : 0.710"  # scripted group (container) (typed FeaturePython)
  n = 0.710028
FEATURE [App::DocumentObjectGroupPython] G4_VITON  # scripted group (container) (typed FeaturePython)
  Dunit = g/cm3
  Dvalue = 1.8
  Group = -> [H_element109,C_element121,F_element018]
  conduct = 2
  density = 1
  expand = 3
  formula = G4_VITON
  name = G4_VITON
  specific = 4
FEATURE [App::DocumentObjectGroupPython] H_element110  label="H_element : 059"  # scripted group (container) (typed FeaturePython)
  n = 2
  ref = H_element
FEATURE [App::DocumentObjectGroupPython] O_element103  label="O_element : 057"  # scripted group (container) (typed FeaturePython)
  n = 1
  ref = O_element
FEATURE [App::DocumentObjectGroupPython] G4_WATER  # scripted group (container) (typed FeaturePython)
  Dunit = g/cm3
  Dvalue = 1
  Group = -> [H_element110,O_element103]
  conduct = 2
  density = 1
  expand = 3
  formula = G4_WATER
  name = G4_WATER
  specific = 4
FEATURE [App::DocumentObjectGroupPython] H_element111  label="H_element : 060"  # scripted group (container) (typed FeaturePython)
  n = 2
  ref = H_element
FEATURE [App::DocumentObjectGroupPython] O_element104  label="O_element : 058"  # scripted group (container) (typed FeaturePython)
  n = 1
  ref = O_element
FEATURE [App::DocumentObjectGroupPython] G4_WATER_VAPOR  # scripted group (container) (typed FeaturePython)
  Dunit = g/cm3
  Dvalue = 0.000756182
  Group = -> [H_element111,O_element104]
  conduct = 2
  density = 1
  expand = 3
  formula = G4_WATER_VAPOR
  name = G4_WATER_VAPOR
  specific = 4
FEATURE [App::DocumentObjectGroupPython] C_element122  label="C_element : 068"  # scripted group (container) (typed FeaturePython)
  n = 8
  ref = C_element
FEATURE [App::DocumentObjectGroupPython] H_element112  label="H_element : 061"  # scripted group (container) (typed FeaturePython)
  n = 10
  ref = H_element
FEATURE [App::DocumentObjectGroupPython] G4_XYLENE  # scripted group (container) (typed FeaturePython)
  Dunit = g/cm3
  Dvalue = 0.87
  Group = -> [C_element122,H_element112]
  conduct = 2
  density = 1
  expand = 3
  formula = G4_XYLENE
  name = G4_XYLENE
  specific = 4
FEATURE [App::DocumentObjectGroupPython] C_element123  label="C_element : 069"  # scripted group (container) (typed FeaturePython)
  n = 1
  ref = C_element
FEATURE [App::DocumentObjectGroupPython] G4_GRAPHITE  # scripted group (container) (typed FeaturePython)
  Dunit = g/cm3
  Dvalue = 2.21
  Group = -> [C_element123]
  conduct = 2
  density = 1
  expand = 3
  formula = G4_GRAPHITE
  name = G4_GRAPHITE
  specific = 4
FEATURE [App::DocumentObjectGroupPython] NIST  # scripted group (container) (typed FeaturePython)
  Group = -> [G4_A_150_TISSUE,G4_ACETONE,G4_ACETYLENE,G4_ADENINE,G4_ADIPOSE_TISSUE_ICRP,G4_AIR,G4_ALANINE,G4_ALUMINUM_OXIDE,G4_AMBER,G4_AMMONIA,G4_ANILINE,G4_ANTHRACENE,G4_B_100_BONE,G4_BAKELITE,G4_BARIUM_FLUORIDE,G4_BARIUM_SULFATE,G4_BENZENE,G4_BERYLLIUM_OXIDE,G4_BGO,G4_BLOOD_ICRP,G4_BONE_COMPACT_ICRU,G4_BONE_CORTICAL_ICRP,G4_BORON_CARBIDE,G4_BORON_OXIDE,G4_BRAIN_ICRP,G4_BUTANE,G4_N_BUTYL_ALCOHOL,G4_C_552,+152 more]
FEATURE [App::DocumentObjectGroupPython] H_element113  label="H_element : 062"  # scripted group (container) (typed FeaturePython)
  n = 1
  ref = H_element
FEATURE [App::DocumentObjectGroupPython] G4_H  # scripted group (container) (typed FeaturePython)
  Dunit = g/cm3
  Dvalue = 8.3748e-05
  Group = -> [H_element113]
  conduct = 2
  density = 1
  expand = 3
  formula = H
  name = G4_H
  specific = 4
FEATURE [App::DocumentObjectGroupPython] He_element001  label="He_element : 1"  # scripted group (container) (typed FeaturePython)
  n = 1
  ref = He_element
FEATURE [App::DocumentObjectGroupPython] G4_He  # scripted group (container) (typed FeaturePython)
  Dunit = g/cm3
  Dvalue = 0.000166322
  Group = -> [He_element001]
  conduct = 2
  density = 1
  expand = 3
  formula = He
  name = G4_He
  specific = 4
FEATURE [App::DocumentObjectGroupPython] Li_element008  label="Li_element : 008"  # scripted group (container) (typed FeaturePython)
  n = 1
  ref = Li_element
FEATURE [App::DocumentObjectGroupPython] G4_Li  # scripted group (container) (typed FeaturePython)
  Dunit = g/cm3
  Dvalue = 0.534
  Group = -> [Li_element008]
  conduct = 2
  density = 1
  expand = 3
  formula = Li
  name = G4_Li
  specific = 4
FEATURE [App::DocumentObjectGroupPython] Be_element002  label="Be_element : 002"  # scripted group (container) (typed FeaturePython)
  n = 1
  ref = Be_element
FEATURE [App::DocumentObjectGroupPython] G4_Be  # scripted group (container) (typed FeaturePython)
  Dunit = g/cm3
  Dvalue = 1.848
  Group = -> [Be_element002]
  conduct = 2
  density = 1
  expand = 3
  formula = Be
  name = G4_Be
  specific = 4
FEATURE [App::DocumentObjectGroupPython] B_element007  label="B_element : 007"  # scripted group (container) (typed FeaturePython)
  n = 1
  ref = B_element
FEATURE [App::DocumentObjectGroupPython] G4_B  # scripted group (container) (typed FeaturePython)
  Dunit = g/cm3
  Dvalue = 2.37
  Group = -> [B_element007]
  conduct = 2
  density = 1
  expand = 3
  formula = B
  name = G4_B
  specific = 4
FEATURE [App::DocumentObjectGroupPython] C_element124  label="C_element : 070"  # scripted group (container) (typed FeaturePython)
  n = 1
  ref = C_element
FEATURE [App::DocumentObjectGroupPython] G4_C  # scripted group (container) (typed FeaturePython)
  Dunit = g/cm3
  Dvalue = 2
  Group = -> [C_element124]
  conduct = 2
  density = 1
  expand = 3
  formula = C
  name = G4_C
  specific = 4
FEATURE [App::DocumentObjectGroupPython] N_element048  label="N_element : 021"  # scripted group (container) (typed FeaturePython)
  n = 1
  ref = N_element
FEATURE [App::DocumentObjectGroupPython] G4_N  # scripted group (container) (typed FeaturePython)
  Dunit = g/cm3
  Dvalue = 0.0011652
  Group = -> [N_element048]
  conduct = 2
  density = 1
  expand = 3
  formula = N
  name = G4_N
  specific = 4
FEATURE [App::DocumentObjectGroupPython] O_element105  label="O_element : 059"  # scripted group (container) (typed FeaturePython)
  n = 1
  ref = O_element
FEATURE [App::DocumentObjectGroupPython] G4_O  # scripted group (container) (typed FeaturePython)
  Dunit = g/cm3
  Dvalue = 0.00133151
  Group = -> [O_element105]
  conduct = 2
  density = 1
  expand = 3
  formula = O
  name = G4_O
  specific = 4
FEATURE [App::DocumentObjectGroupPython] F_element019  label="F_element : 008"  # scripted group (container) (typed FeaturePython)
  n = 1
  ref = F_element
FEATURE [App::DocumentObjectGroupPython] G4_F  # scripted group (container) (typed FeaturePython)
  Dunit = g/cm3
  Dvalue = 0.00158029
  Group = -> [F_element019]
  conduct = 2
  density = 1
  expand = 3
  formula = F
  name = G4_F
  specific = 4
FEATURE [App::DocumentObjectGroupPython] Ne_element001  label="Ne_element : 1"  # scripted group (container) (typed FeaturePython)
  n = 1
  ref = Ne_element
FEATURE [App::DocumentObjectGroupPython] G4_Ne  # scripted group (container) (typed FeaturePython)
  Dunit = g/cm3
  Dvalue = 0.000838505
  Group = -> [Ne_element001]
  conduct = 2
  density = 1
  expand = 3
  formula = Ne
  name = G4_Ne
  specific = 4
FEATURE [App::DocumentObjectGroupPython] Na_element020  label="Na_element : 005"  # scripted group (container) (typed FeaturePython)
  n = 1
  ref = Na_element
FEATURE [App::DocumentObjectGroupPython] G4_Na  # scripted group (container) (typed FeaturePython)
  Dunit = g/cm3
  Dvalue = 0.971
  Group = -> [Na_element020]
  conduct = 2
  density = 1
  expand = 3
  formula = Na
  name = G4_Na
  specific = 4
FEATURE [App::DocumentObjectGroupPython] Mg_element011  label="Mg_element : 005"  # scripted group (container) (typed FeaturePython)
  n = 1
  ref = Mg_element
FEATURE [App::DocumentObjectGroupPython] G4_Mg  # scripted group (container) (typed FeaturePython)
  Dunit = g/cm3
  Dvalue = 1.74
  Group = -> [Mg_element011]
  conduct = 2
  density = 1
  expand = 3
  formula = Mg
  name = G4_Mg
  specific = 4
FEATURE [App::DocumentObjectGroupPython] Al_element004  label="Al_element : 1"  # scripted group (container) (typed FeaturePython)
  n = 1
  ref = Al_element
FEATURE [App::DocumentObjectGroupPython] G4_Al  # scripted group (container) (typed FeaturePython)
  Dunit = g/cm3
  Dvalue = 2.699
  Group = -> [Al_element004]
  conduct = 2
  density = 1
  expand = 3
  formula = Al
  name = G4_Al
  specific = 4
FEATURE [App::DocumentObjectGroupPython] Si_element007  label="Si_element : 002"  # scripted group (container) (typed FeaturePython)
  n = 1
  ref = Si_element
FEATURE [App::DocumentObjectGroupPython] G4_Si  # scripted group (container) (typed FeaturePython)
  Dunit = g/cm3
  Dvalue = 2.33
  Group = -> [Si_element007]
  conduct = 2
  density = 1
  expand = 3
  formula = Si
  name = G4_Si
  specific = 4
FEATURE [App::DocumentObjectGroupPython] P_element013  label="P_element : 002"  # scripted group (container) (typed FeaturePython)
  n = 1
  ref = P_element
FEATURE [App::DocumentObjectGroupPython] G4_P  # scripted group (container) (typed FeaturePython)
  Dunit = g/cm3
  Dvalue = 2.2
  Group = -> [P_element013]
  conduct = 2
  density = 1
  expand = 3
  formula = P
  name = G4_P
  specific = 4
FEATURE [App::DocumentObjectGroupPython] S_element023  label="S_element : 007"  # scripted group (container) (typed FeaturePython)
  n = 1
  ref = S_element
FEATURE [App::DocumentObjectGroupPython] G4_S  # scripted group (container) (typed FeaturePython)
  Dunit = g/cm3
  Dvalue = 2
  Group = -> [S_element023]
  conduct = 2
  density = 1
  expand = 3
  formula = S
  name = G4_S
  specific = 4
FEATURE [App::DocumentObjectGroupPython] Cl_element029  label="Cl_element : 015"  # scripted group (container) (typed FeaturePython)
  n = 1
  ref = Cl_element
FEATURE [App::DocumentObjectGroupPython] G4_Cl  # scripted group (container) (typed FeaturePython)
  Dunit = g/cm3
  Dvalue = 0.00299473
  Group = -> [Cl_element029]
  conduct = 2
  density = 1
  expand = 3
  formula = Cl
  name = G4_Cl
  specific = 4
FEATURE [App::DocumentObjectGroupPython] Ar_element002  label="Ar_element : 1"  # scripted group (container) (typed FeaturePython)
  n = 1
  ref = Ar_element
FEATURE [App::DocumentObjectGroupPython] G4_Ar  # scripted group (container) (typed FeaturePython)
  Dunit = g/cm3
  Dvalue = 0.00166201
  Group = -> [Ar_element002]
  conduct = 2
  density = 1
  expand = 3
  formula = Ar
  name = G4_Ar
  specific = 4
FEATURE [App::DocumentObjectGroupPython] K_element013  label="K_element : 003"  # scripted group (container) (typed FeaturePython)
  n = 1
  ref = K_element
FEATURE [App::DocumentObjectGroupPython] G4_K  # scripted group (container) (typed FeaturePython)
  Dunit = g/cm3
  Dvalue = 0.862
  Group = -> [K_element013]
  conduct = 2
  density = 1
  expand = 3
  formula = K
  name = G4_K
  specific = 4
FEATURE [App::DocumentObjectGroupPython] Ca_element014  label="Ca_element : 007"  # scripted group (container) (typed FeaturePython)
  n = 1
  ref = Ca_element
FEATURE [App::DocumentObjectGroupPython] G4_Ca  # scripted group (container) (typed FeaturePython)
  Dunit = g/cm3
  Dvalue = 1.55
  Group = -> [Ca_element014]
  conduct = 2
  density = 1
  expand = 3
  formula = Ca
  name = G4_Ca
  specific = 4
FEATURE [App::DocumentObjectGroupPython] Sc_element001  label="Sc_element : 1"  # scripted group (container) (typed FeaturePython)
  n = 1
  ref = Sc_element
FEATURE [App::DocumentObjectGroupPython] G4_Sc  # scripted group (container) (typed FeaturePython)
  Dunit = g/cm3
  Dvalue = 2.989
  Group = -> [Sc_element001]
  conduct = 2
  density = 1
  expand = 3
  formula = Sc
  name = G4_Sc
  specific = 4
FEATURE [App::DocumentObjectGroupPython] Ti_element004  label="Ti_element : 002"  # scripted group (container) (typed FeaturePython)
  n = 1
  ref = Ti_element
FEATURE [App::DocumentObjectGroupPython] G4_Ti  # scripted group (container) (typed FeaturePython)
  Dunit = g/cm3
  Dvalue = 4.54
  Group = -> [Ti_element004]
  conduct = 2
  density = 1
  expand = 3
  formula = Ti
  name = G4_Ti
  specific = 4
FEATURE [App::DocumentObjectGroupPython] V_element001  label="V_element : 1"  # scripted group (container) (typed FeaturePython)
  n = 1
  ref = V_element
FEATURE [App::DocumentObjectGroupPython] G4_V  # scripted group (container) (typed FeaturePython)
  Dunit = g/cm3
  Dvalue = 6.11
  Group = -> [V_element001]
  conduct = 2
  density = 1
  expand = 3
  formula = V
  name = G4_V
  specific = 4
FEATURE [App::DocumentObjectGroupPython] Cr_element001  label="Cr_element : 1"  # scripted group (container) (typed FeaturePython)
  n = 1
  ref = Cr_element
FEATURE [App::DocumentObjectGroupPython] G4_Cr  # scripted group (container) (typed FeaturePython)
  Dunit = g/cm3
  Dvalue = 7.18
  Group = -> [Cr_element001]
  conduct = 2
  density = 1
  expand = 3
  formula = Cr
  name = G4_Cr
  specific = 4
FEATURE [App::DocumentObjectGroupPython] Mn_element001  label="Mn_element : 1"  # scripted group (container) (typed FeaturePython)
  n = 1
  ref = Mn_element
FEATURE [App::DocumentObjectGroupPython] G4_Mn  # scripted group (container) (typed FeaturePython)
  Dunit = g/cm3
  Dvalue = 7.44
  Group = -> [Mn_element001]
  conduct = 2
  density = 1
  expand = 3
  formula = Mn
  name = G4_Mn
  specific = 4
FEATURE [App::DocumentObjectGroupPython] Fe_element007  label="Fe_element : 004"  # scripted group (container) (typed FeaturePython)
  n = 1
  ref = Fe_element
FEATURE [App::DocumentObjectGroupPython] G4_Fe  # scripted group (container) (typed FeaturePython)
  Dunit = g/cm3
  Dvalue = 7.874
  Group = -> [Fe_element007]
  conduct = 2
  density = 1
  expand = 3
  formula = Fe
  name = G4_Fe
  specific = 4
FEATURE [App::DocumentObjectGroupPython] Co_element001  label="Co_element : 1"  # scripted group (container) (typed FeaturePython)
  n = 1
  ref = Co_element
FEATURE [App::DocumentObjectGroupPython] G4_Co  # scripted group (container) (typed FeaturePython)
  Dunit = g/cm3
  Dvalue = 8.9
  Group = -> [Co_element001]
  conduct = 2
  density = 1
  expand = 3
  formula = Co
  name = G4_Co
  specific = 4
FEATURE [App::DocumentObjectGroupPython] Ni_element001  label="Ni_element : 1"  # scripted group (container) (typed FeaturePython)
  n = 1
  ref = Ni_element
FEATURE [App::DocumentObjectGroupPython] G4_Ni  # scripted group (container) (typed FeaturePython)
  Dunit = g/cm3
  Dvalue = 8.902
  Group = -> [Ni_element001]
  conduct = 2
  density = 1
  expand = 3
  formula = Ni
  name = G4_Ni
  specific = 4
FEATURE [App::DocumentObjectGroupPython] Cu_element001  label="Cu_element : 1"  # scripted group (container) (typed FeaturePython)
  n = 1
  ref = Cu_element
FEATURE [App::DocumentObjectGroupPython] G4_Cu  # scripted group (container) (typed FeaturePython)
  Dunit = g/cm3
  Dvalue = 8.96
  Group = -> [Cu_element001]
  conduct = 2
  density = 1
  expand = 3
  formula = Cu
  name = G4_Cu
  specific = 4
FEATURE [App::DocumentObjectGroupPython] Zn_element001  label="Zn_element : 1"  # scripted group (container) (typed FeaturePython)
  n = 1
  ref = Zn_element
FEATURE [App::DocumentObjectGroupPython] G4_Zn  # scripted group (container) (typed FeaturePython)
  Dunit = g/cm3
  Dvalue = 7.133
  Group = -> [Zn_element001]
  conduct = 2
  density = 1
  expand = 3
  formula = Zn
  name = G4_Zn
  specific = 4
FEATURE [App::DocumentObjectGroupPython] Ga_element002  label="Ga_element : 002"  # scripted group (container) (typed FeaturePython)
  n = 1
  ref = Ga_element
FEATURE [App::DocumentObjectGroupPython] G4_Ga  # scripted group (container) (typed FeaturePython)
  Dunit = g/cm3
  Dvalue = 5.904
  Group = -> [Ga_element002]
  conduct = 2
  density = 1
  expand = 3
  formula = Ga
  name = G4_Ga
  specific = 4
FEATURE [App::DocumentObjectGroupPython] Ge_element002  label="Ge_element : 1"  # scripted group (container) (typed FeaturePython)
  n = 1
  ref = Ge_element
FEATURE [App::DocumentObjectGroupPython] G4_Ge  # scripted group (container) (typed FeaturePython)
  Dunit = g/cm3
  Dvalue = 5.323
  Group = -> [Ge_element002]
  conduct = 2
  density = 1
  expand = 3
  formula = Ge
  name = G4_Ge
  specific = 4
FEATURE [App::DocumentObjectGroupPython] As_element003  label="As_element : 002"  # scripted group (container) (typed FeaturePython)
  n = 1
  ref = As_element
FEATURE [App::DocumentObjectGroupPython] G4_As  # scripted group (container) (typed FeaturePython)
  Dunit = g/cm3
  Dvalue = 5.73
  Group = -> [As_element003]
  conduct = 2
  density = 1
  expand = 3
  formula = As
  name = G4_As
  specific = 4
FEATURE [App::DocumentObjectGroupPython] Se_element001  label="Se_element : 1"  # scripted group (container) (typed FeaturePython)
  n = 1
  ref = Se_element
FEATURE [App::DocumentObjectGroupPython] G4_Se  # scripted group (container) (typed FeaturePython)
  Dunit = g/cm3
  Dvalue = 4.5
  Group = -> [Se_element001]
  conduct = 2
  density = 1
  expand = 3
  formula = Se
  name = G4_Se
  specific = 4
FEATURE [App::DocumentObjectGroupPython] Br_element007  label="Br_element : 004"  # scripted group (container) (typed FeaturePython)
  n = 1
  ref = Br_element
FEATURE [App::DocumentObjectGroupPython] G4_Br  # scripted group (container) (typed FeaturePython)
  Dunit = g/cm3
  Dvalue = 0.0070721
  Group = -> [Br_element007]
  conduct = 2
  density = 1
  expand = 3
  formula = Br
  name = G4_Br
  specific = 4
FEATURE [App::DocumentObjectGroupPython] Kr_element001  label="Kr_element : 1"  # scripted group (container) (typed FeaturePython)
  n = 1
  ref = Kr_element
FEATURE [App::DocumentObjectGroupPython] G4_Kr  # scripted group (container) (typed FeaturePython)
  Dunit = g/cm3
  Dvalue = 0.00347832
  Group = -> [Kr_element001]
  conduct = 2
  density = 1
  expand = 3
  formula = Kr
  name = G4_Kr
  specific = 4
FEATURE [App::DocumentObjectGroupPython] Rb_element001  label="Rb_element : 1"  # scripted group (container) (typed FeaturePython)
  n = 1
  ref = Rb_element
FEATURE [App::DocumentObjectGroupPython] G4_Rb  # scripted group (container) (typed FeaturePython)
  Dunit = g/cm3
  Dvalue = 1.532
  Group = -> [Rb_element001]
  conduct = 2
  density = 1
  expand = 3
  formula = Rb
  name = G4_Rb
  specific = 4
FEATURE [App::DocumentObjectGroupPython] Sr_element001  label="Sr_element : 1"  # scripted group (container) (typed FeaturePython)
  n = 1
  ref = Sr_element
FEATURE [App::DocumentObjectGroupPython] G4_Sr  # scripted group (container) (typed FeaturePython)
  Dunit = g/cm3
  Dvalue = 2.54
  Group = -> [Sr_element001]
  conduct = 2
  density = 1
  expand = 3
  formula = Sr
  name = G4_Sr
  specific = 4
FEATURE [App::DocumentObjectGroupPython] Y_element001  label="Y_element : 1"  # scripted group (container) (typed FeaturePython)
  n = 1
  ref = Y_element
FEATURE [App::DocumentObjectGroupPython] G4_Y  # scripted group (container) (typed FeaturePython)
  Dunit = g/cm3
  Dvalue = 4.469
  Group = -> [Y_element001]
  conduct = 2
  density = 1
  expand = 3
  formula = Y
  name = G4_Y
  specific = 4
FEATURE [App::DocumentObjectGroupPython] Zr_element001  label="Zr_element : 1"  # scripted group (container) (typed FeaturePython)
  n = 1
  ref = Zr_element
FEATURE [App::DocumentObjectGroupPython] G4_Zr  # scripted group (container) (typed FeaturePython)
  Dunit = g/cm3
  Dvalue = 6.506
  Group = -> [Zr_element001]
  conduct = 2
  density = 1
  expand = 3
  formula = Zr
  name = G4_Zr
  specific = 4
FEATURE [App::DocumentObjectGroupPython] Nb_element001  label="Nb_element : 1"  # scripted group (container) (typed FeaturePython)
  n = 1
  ref = Nb_element
FEATURE [App::DocumentObjectGroupPython] G4_Nb  # scripted group (container) (typed FeaturePython)
  Dunit = g/cm3
  Dvalue = 8.57
  Group = -> [Nb_element001]
  conduct = 2
  density = 1
  expand = 3
  formula = Nb
  name = G4_Nb
  specific = 4
FEATURE [App::DocumentObjectGroupPython] Mo_element001  label="Mo_element : 1"  # scripted group (container) (typed FeaturePython)
  n = 1
  ref = Mo_element
FEATURE [App::DocumentObjectGroupPython] G4_Mo  # scripted group (container) (typed FeaturePython)
  Dunit = g/cm3
  Dvalue = 10.22
  Group = -> [Mo_element001]
  conduct = 2
  density = 1
  expand = 3
  formula = Mo
  name = G4_Mo
  specific = 4
FEATURE [App::DocumentObjectGroupPython] Tc_element001  label="Tc_element : 1"  # scripted group (container) (typed FeaturePython)
  n = 1
  ref = Tc_element
FEATURE [App::DocumentObjectGroupPython] G4_Tc  # scripted group (container) (typed FeaturePython)
  Dunit = g/cm3
  Dvalue = 11.5
  Group = -> [Tc_element001]
  conduct = 2
  density = 1
  expand = 3
  formula = Tc
  name = G4_Tc
  specific = 4
FEATURE [App::DocumentObjectGroupPython] Ru_element001  label="Ru_element : 1"  # scripted group (container) (typed FeaturePython)
  n = 1
  ref = Ru_element
FEATURE [App::DocumentObjectGroupPython] G4_Ru  # scripted group (container) (typed FeaturePython)
  Dunit = g/cm3
  Dvalue = 12.41
  Group = -> [Ru_element001]
  conduct = 2
  density = 1
  expand = 3
  formula = Ru
  name = G4_Ru
  specific = 4
FEATURE [App::DocumentObjectGroupPython] Rh_element001  label="Rh_element : 1"  # scripted group (container) (typed FeaturePython)
  n = 1
  ref = Rh_element
FEATURE [App::DocumentObjectGroupPython] G4_Rh  # scripted group (container) (typed FeaturePython)
  Dunit = g/cm3
  Dvalue = 12.41
  Group = -> [Rh_element001]
  conduct = 2
  density = 1
  expand = 3
  formula = Rh
  name = G4_Rh
  specific = 4
FEATURE [App::DocumentObjectGroupPython] Pd_element001  label="Pd_element : 1"  # scripted group (container) (typed FeaturePython)
  n = 1
  ref = Pd_element
FEATURE [App::DocumentObjectGroupPython] G4_Pd  # scripted group (container) (typed FeaturePython)
  Dunit = g/cm3
  Dvalue = 12.02
  Group = -> [Pd_element001]
  conduct = 2
  density = 1
  expand = 3
  formula = Pd
  name = G4_Pd
  specific = 4
FEATURE [App::DocumentObjectGroupPython] Ag_element006  label="Ag_element : 004"  # scripted group (container) (typed FeaturePython)
  n = 1
  ref = Ag_element
FEATURE [App::DocumentObjectGroupPython] G4_Ag  # scripted group (container) (typed FeaturePython)
  Dunit = g/cm3
  Dvalue = 10.5
  Group = -> [Ag_element006]
  conduct = 2
  density = 1
  expand = 3
  formula = Ag
  name = G4_Ag
  specific = 4
FEATURE [App::DocumentObjectGroupPython] Cd_element003  label="Cd_element : 003"  # scripted group (container) (typed FeaturePython)
  n = 1
  ref = Cd_element
FEATURE [App::DocumentObjectGroupPython] G4_Cd  # scripted group (container) (typed FeaturePython)
  Dunit = g/cm3
  Dvalue = 8.65
  Group = -> [Cd_element003]
  conduct = 2
  density = 1
  expand = 3
  formula = Cd
  name = G4_Cd
  specific = 4
FEATURE [App::DocumentObjectGroupPython] In_element001  label="In_element : 1"  # scripted group (container) (typed FeaturePython)
  n = 1
  ref = In_element
FEATURE [App::DocumentObjectGroupPython] G4_In  # scripted group (container) (typed FeaturePython)
  Dunit = g/cm3
  Dvalue = 7.31
  Group = -> [In_element001]
  conduct = 2
  density = 1
  expand = 3
  formula = In
  name = G4_In
  specific = 4
FEATURE [App::DocumentObjectGroupPython] Sn_element001  label="Sn_element : 1"  # scripted group (container) (typed FeaturePython)
  n = 1
  ref = Sn_element
FEATURE [App::DocumentObjectGroupPython] G4_Sn  # scripted group (container) (typed FeaturePython)
  Dunit = g/cm3
  Dvalue = 7.31
  Group = -> [Sn_element001]
  conduct = 2
  density = 1
  expand = 3
  formula = Sn
  name = G4_Sn
  specific = 4
FEATURE [App::DocumentObjectGroupPython] Sb_element001  label="Sb_element : 1"  # scripted group (container) (typed FeaturePython)
  n = 1
  ref = Sb_element
FEATURE [App::DocumentObjectGroupPython] G4_Sb  # scripted group (container) (typed FeaturePython)
  Dunit = g/cm3
  Dvalue = 6.691
  Group = -> [Sb_element001]
  conduct = 2
  density = 1
  expand = 3
  formula = Sb
  name = G4_Sb
  specific = 4
FEATURE [App::DocumentObjectGroupPython] Te_element002  label="Te_element : 002"  # scripted group (container) (typed FeaturePython)
  n = 1
  ref = Te_element
FEATURE [App::DocumentObjectGroupPython] G4_Te  # scripted group (container) (typed FeaturePython)
  Dunit = g/cm3
  Dvalue = 6.24
  Group = -> [Te_element002]
  conduct = 2
  density = 1
  expand = 3
  formula = Te
  name = G4_Te
  specific = 4
FEATURE [App::DocumentObjectGroupPython] I_element010  label="I_element : 006"  # scripted group (container) (typed FeaturePython)
  n = 1
  ref = I_element
FEATURE [App::DocumentObjectGroupPython] G4_I  # scripted group (container) (typed FeaturePython)
  Dunit = g/cm3
  Dvalue = 4.93
  Group = -> [I_element010]
  conduct = 2
  density = 1
  expand = 3
  formula = I
  name = G4_I
  specific = 4
FEATURE [App::DocumentObjectGroupPython] Xe_element001  label="Xe_element : 1"  # scripted group (container) (typed FeaturePython)
  n = 1
  ref = Xe_element
FEATURE [App::DocumentObjectGroupPython] G4_Xe  # scripted group (container) (typed FeaturePython)
  Dunit = g/cm3
  Dvalue = 0.00548536
  Group = -> [Xe_element001]
  conduct = 2
  density = 1
  expand = 3
  formula = Xe
  name = G4_Xe
  specific = 4
FEATURE [App::DocumentObjectGroupPython] Cs_element003  label="Cs_element : 003"  # scripted group (container) (typed FeaturePython)
  n = 1
  ref = Cs_element
FEATURE [App::DocumentObjectGroupPython] G4_Cs  # scripted group (container) (typed FeaturePython)
  Dunit = g/cm3
  Dvalue = 1.873
  Group = -> [Cs_element003]
  conduct = 2
  density = 1
  expand = 3
  formula = Cs
  name = G4_Cs
  specific = 4
FEATURE [App::DocumentObjectGroupPython] Ba_element003  label="Ba_element : 003"  # scripted group (container) (typed FeaturePython)
  n = 1
  ref = Ba_element
FEATURE [App::DocumentObjectGroupPython] G4_Ba  # scripted group (container) (typed FeaturePython)
  Dunit = g/cm3
  Dvalue = 3.5
  Group = -> [Ba_element003]
  conduct = 2
  density = 1
  expand = 3
  formula = Ba
  name = G4_Ba
  specific = 4
FEATURE [App::DocumentObjectGroupPython] La_element003  label="La_element : 003"  # scripted group (container) (typed FeaturePython)
  n = 1
  ref = La_element
FEATURE [App::DocumentObjectGroupPython] G4_La  # scripted group (container) (typed FeaturePython)
  Dunit = g/cm3
  Dvalue = 6.154
  Group = -> [La_element003]
  conduct = 2
  density = 1
  expand = 3
  formula = La
  name = G4_La
  specific = 4
FEATURE [App::DocumentObjectGroupPython] Ce_element002  label="Ce_element : 1"  # scripted group (container) (typed FeaturePython)
  n = 1
  ref = Ce_element
FEATURE [App::DocumentObjectGroupPython] G4_Ce  # scripted group (container) (typed FeaturePython)
  Dunit = g/cm3
  Dvalue = 6.657
  Group = -> [Ce_element002]
  conduct = 2
  density = 1
  expand = 3
  formula = Ce
  name = G4_Ce
  specific = 4
FEATURE [App::DocumentObjectGroupPython] Pr_element001  label="Pr_element : 1"  # scripted group (container) (typed FeaturePython)
  n = 1
  ref = Pr_element
FEATURE [App::DocumentObjectGroupPython] G4_Pr  # scripted group (container) (typed FeaturePython)
  Dunit = g/cm3
  Dvalue = 6.71
  Group = -> [Pr_element001]
  conduct = 2
  density = 1
  expand = 3
  formula = Pr
  name = G4_Pr
  specific = 4
FEATURE [App::DocumentObjectGroupPython] Nd_element001  label="Nd_element : 1"  # scripted group (container) (typed FeaturePython)
  n = 1
  ref = Nd_element
FEATURE [App::DocumentObjectGroupPython] G4_Nd  # scripted group (container) (typed FeaturePython)
  Dunit = g/cm3
  Dvalue = 6.9
  Group = -> [Nd_element001]
  conduct = 2
  density = 1
  expand = 3
  formula = Nd
  name = G4_Nd
  specific = 4
FEATURE [App::DocumentObjectGroupPython] Pm_element001  label="Pm_element : 1"  # scripted group (container) (typed FeaturePython)
  n = 1
  ref = Pm_element
FEATURE [App::DocumentObjectGroupPython] G4_Pm  # scripted group (container) (typed FeaturePython)
  Dunit = g/cm3
  Dvalue = 7.22
  Group = -> [Pm_element001]
  conduct = 2
  density = 1
  expand = 3
  formula = Pm
  name = G4_Pm
  specific = 4
FEATURE [App::DocumentObjectGroupPython] Sm_element001  label="Sm_element : 1"  # scripted group (container) (typed FeaturePython)
  n = 1
  ref = Sm_element
FEATURE [App::DocumentObjectGroupPython] G4_Sm  # scripted group (container) (typed FeaturePython)
  Dunit = g/cm3
  Dvalue = 7.46
  Group = -> [Sm_element001]
  conduct = 2
  density = 1
  expand = 3
  formula = Sm
  name = G4_Sm
  specific = 4
FEATURE [App::DocumentObjectGroupPython] Eu_element001  label="Eu_element : 1"  # scripted group (container) (typed FeaturePython)
  n = 1
  ref = Eu_element
FEATURE [App::DocumentObjectGroupPython] G4_Eu  # scripted group (container) (typed FeaturePython)
  Dunit = g/cm3
  Dvalue = 5.243
  Group = -> [Eu_element001]
  conduct = 2
  density = 1
  expand = 3
  formula = Eu
  name = G4_Eu
  specific = 4
FEATURE [App::DocumentObjectGroupPython] Gd_element002  label="Gd_element : 1"  # scripted group (container) (typed FeaturePython)
  n = 1
  ref = Gd_element
FEATURE [App::DocumentObjectGroupPython] G4_Gd  # scripted group (container) (typed FeaturePython)
  Dunit = g/cm3
  Dvalue = 7.9004
  Group = -> [Gd_element002]
  conduct = 2
  density = 1
  expand = 3
  formula = Gd
  name = G4_Gd
  specific = 4
FEATURE [App::DocumentObjectGroupPython] Tb_element001  label="Tb_element : 1"  # scripted group (container) (typed FeaturePython)
  n = 1
  ref = Tb_element
FEATURE [App::DocumentObjectGroupPython] G4_Tb  # scripted group (container) (typed FeaturePython)
  Dunit = g/cm3
  Dvalue = 8.229
  Group = -> [Tb_element001]
  conduct = 2
  density = 1
  expand = 3
  formula = Tb
  name = G4_Tb
  specific = 4
FEATURE [App::DocumentObjectGroupPython] Dy_element001  label="Dy_element : 1"  # scripted group (container) (typed FeaturePython)
  n = 1
  ref = Dy_element
FEATURE [App::DocumentObjectGroupPython] G4_Dy  # scripted group (container) (typed FeaturePython)
  Dunit = g/cm3
  Dvalue = 8.55
  Group = -> [Dy_element001]
  conduct = 2
  density = 1
  expand = 3
  formula = Dy
  name = G4_Dy
  specific = 4
FEATURE [App::DocumentObjectGroupPython] Ho_element001  label="Ho_element : 1"  # scripted group (container) (typed FeaturePython)
  n = 1
  ref = Ho_element
FEATURE [App::DocumentObjectGroupPython] G4_Ho  # scripted group (container) (typed FeaturePython)
  Dunit = g/cm3
  Dvalue = 8.795
  Group = -> [Ho_element001]
  conduct = 2
  density = 1
  expand = 3
  formula = Ho
  name = G4_Ho
  specific = 4
FEATURE [App::DocumentObjectGroupPython] Er_element001  label="Er_element : 1"  # scripted group (container) (typed FeaturePython)
  n = 1
  ref = Er_element
FEATURE [App::DocumentObjectGroupPython] G4_Er  # scripted group (container) (typed FeaturePython)
  Dunit = g/cm3
  Dvalue = 9.066
  Group = -> [Er_element001]
  conduct = 2
  density = 1
  expand = 3
  formula = Er
  name = G4_Er
  specific = 4
FEATURE [App::DocumentObjectGroupPython] Tm_element001  label="Tm_element : 1"  # scripted group (container) (typed FeaturePython)
  n = 1
  ref = Tm_element
FEATURE [App::DocumentObjectGroupPython] G4_Tm  # scripted group (container) (typed FeaturePython)
  Dunit = g/cm3
  Dvalue = 9.321
  Group = -> [Tm_element001]
  conduct = 2
  density = 1
  expand = 3
  formula = Tm
  name = G4_Tm
  specific = 4
FEATURE [App::DocumentObjectGroupPython] Yb_element001  label="Yb_element : 1"  # scripted group (container) (typed FeaturePython)
  n = 1
  ref = Yb_element
FEATURE [App::DocumentObjectGroupPython] G4_Yb  # scripted group (container) (typed FeaturePython)
  Dunit = g/cm3
  Dvalue = 6.73
  Group = -> [Yb_element001]
  conduct = 2
  density = 1
  expand = 3
  formula = Yb
  name = G4_Yb
  specific = 4
FEATURE [App::DocumentObjectGroupPython] Lu_element001  label="Lu_element : 1"  # scripted group (container) (typed FeaturePython)
  n = 1
  ref = Lu_element
FEATURE [App::DocumentObjectGroupPython] G4_Lu  # scripted group (container) (typed FeaturePython)
  Dunit = g/cm3
  Dvalue = 9.84
  Group = -> [Lu_element001]
  conduct = 2
  density = 1
  expand = 3
  formula = Lu
  name = G4_Lu
  specific = 4
FEATURE [App::DocumentObjectGroupPython] Hf_element001  label="Hf_element : 1"  # scripted group (container) (typed FeaturePython)
  n = 1
  ref = Hf_element
FEATURE [App::DocumentObjectGroupPython] G4_Hf  # scripted group (container) (typed FeaturePython)
  Dunit = g/cm3
  Dvalue = 13.31
  Group = -> [Hf_element001]
  conduct = 2
  density = 1
  expand = 3
  formula = Hf
  name = G4_Hf
  specific = 4
FEATURE [App::DocumentObjectGroupPython] Ta_element001  label="Ta_element : 1"  # scripted group (container) (typed FeaturePython)
  n = 1
  ref = Ta_element
FEATURE [App::DocumentObjectGroupPython] G4_Ta  # scripted group (container) (typed FeaturePython)
  Dunit = g/cm3
  Dvalue = 16.654
  Group = -> [Ta_element001]
  conduct = 2
  density = 1
  expand = 3
  formula = Ta
  name = G4_Ta
  specific = 4
FEATURE [App::DocumentObjectGroupPython] W_element004  label="W_element : 004"  # scripted group (container) (typed FeaturePython)
  n = 1
  ref = W_element
FEATURE [App::DocumentObjectGroupPython] G4_W  # scripted group (container) (typed FeaturePython)
  Dunit = g/cm3
  Dvalue = 19.3
  Group = -> [W_element004]
  conduct = 2
  density = 1
  expand = 3
  formula = W
  name = G4_W
  specific = 4
FEATURE [App::DocumentObjectGroupPython] Re_element001  label="Re_element : 1"  # scripted group (container) (typed FeaturePython)
  n = 1
  ref = Re_element
FEATURE [App::DocumentObjectGroupPython] G4_Re  # scripted group (container) (typed FeaturePython)
  Dunit = g/cm3
  Dvalue = 21.02
  Group = -> [Re_element001]
  conduct = 2
  density = 1
  expand = 3
  formula = Re
  name = G4_Re
  specific = 4
FEATURE [App::DocumentObjectGroupPython] Os_element001  label="Os_element : 1"  # scripted group (container) (typed FeaturePython)
  n = 1
  ref = Os_element
FEATURE [App::DocumentObjectGroupPython] G4_Os  # scripted group (container) (typed FeaturePython)
  Dunit = g/cm3
  Dvalue = 22.57
  Group = -> [Os_element001]
  conduct = 2
  density = 1
  expand = 3
  formula = Os
  name = G4_Os
  specific = 4
FEATURE [App::DocumentObjectGroupPython] Ir_element001  label="Ir_element : 1"  # scripted group (container) (typed FeaturePython)
  n = 1
  ref = Ir_element
FEATURE [App::DocumentObjectGroupPython] G4_Ir  # scripted group (container) (typed FeaturePython)
  Dunit = g/cm3
  Dvalue = 22.42
  Group = -> [Ir_element001]
  conduct = 2
  density = 1
  expand = 3
  formula = Ir
  name = G4_Ir
  specific = 4
FEATURE [App::DocumentObjectGroupPython] Pt_element001  label="Pt_element : 1"  # scripted group (container) (typed FeaturePython)
  n = 1
  ref = Pt_element
FEATURE [App::DocumentObjectGroupPython] G4_Pt  # scripted group (container) (typed FeaturePython)
  Dunit = g/cm3
  Dvalue = 21.45
  Group = -> [Pt_element001]
  conduct = 2
  density = 1
  expand = 3
  formula = Pt
  name = G4_Pt
  specific = 4
FEATURE [App::DocumentObjectGroupPython] Au_element001  label="Au_element : 1"  # scripted group (container) (typed FeaturePython)
  n = 1
  ref = Au_element
FEATURE [App::DocumentObjectGroupPython] G4_Au  # scripted group (container) (typed FeaturePython)
  Dunit = g/cm3
  Dvalue = 19.32
  Group = -> [Au_element001]
  conduct = 2
  density = 1
  expand = 3
  formula = Au
  name = G4_Au
  specific = 4
FEATURE [App::DocumentObjectGroupPython] Hg_element002  label="Hg_element : 002"  # scripted group (container) (typed FeaturePython)
  n = 1
  ref = Hg_element
FEATURE [App::DocumentObjectGroupPython] G4_Hg  # scripted group (container) (typed FeaturePython)
  Dunit = g/cm3
  Dvalue = 13.546
  Group = -> [Hg_element002]
  conduct = 2
  density = 1
  expand = 3
  formula = Hg
  name = G4_Hg
  specific = 4
FEATURE [App::DocumentObjectGroupPython] Tl_element002  label="Tl_element : 002"  # scripted group (container) (typed FeaturePython)
  n = 1
  ref = Tl_element
FEATURE [App::DocumentObjectGroupPython] G4_Tl  # scripted group (container) (typed FeaturePython)
  Dunit = g/cm3
  Dvalue = 11.72
  Group = -> [Tl_element002]
  conduct = 2
  density = 1
  expand = 3
  formula = Tl
  name = G4_Tl
  specific = 4
FEATURE [App::DocumentObjectGroupPython] Pb_element003  label="Pb_element : 1"  # scripted group (container) (typed FeaturePython)
  n = 1
  ref = Pb_element
FEATURE [App::DocumentObjectGroupPython] G4_Pb  # scripted group (container) (typed FeaturePython)
  Dunit = g/cm3
  Dvalue = 11.35
  Group = -> [Pb_element003]
  conduct = 2
  density = 1
  expand = 3
  formula = Pb
  name = G4_Pb
  specific = 4
FEATURE [App::DocumentObjectGroupPython] Bi_element002  label="Bi_element : 1"  # scripted group (container) (typed FeaturePython)
  n = 1
  ref = Bi_element
FEATURE [App::DocumentObjectGroupPython] G4_Bi  # scripted group (container) (typed FeaturePython)
  Dunit = g/cm3
  Dvalue = 9.747
  Group = -> [Bi_element002]
  conduct = 2
  density = 1
  expand = 3
  formula = Bi
  name = G4_Bi
  specific = 4
FEATURE [App::DocumentObjectGroupPython] Po_element001  label="Po_element : 1"  # scripted group (container) (typed FeaturePython)
  n = 1
  ref = Po_element
FEATURE [App::DocumentObjectGroupPython] G4_Po  # scripted group (container) (typed FeaturePython)
  Dunit = g/cm3
  Dvalue = 9.32
  Group = -> [Po_element001]
  conduct = 2
  density = 1
  expand = 3
  formula = Po
  name = G4_Po
  specific = 4
FEATURE [App::DocumentObjectGroupPython] At_element001  label="At_element : 1"  # scripted group (container) (typed FeaturePython)
  n = 1
  ref = At_element
FEATURE [App::DocumentObjectGroupPython] G4_At  # scripted group (container) (typed FeaturePython)
  Dunit = g/cm3
  Dvalue = 9.32
  Group = -> [At_element001]
  conduct = 2
  density = 1
  expand = 3
  formula = At
  name = G4_At
  specific = 4
FEATURE [App::DocumentObjectGroupPython] Rn_element001  label="Rn_element : 1"  # scripted group (container) (typed FeaturePython)
  n = 1
  ref = Rn_element
FEATURE [App::DocumentObjectGroupPython] G4_Rn  # scripted group (container) (typed FeaturePython)
  Dunit = g/cm3
  Dvalue = 0.00900662
  Group = -> [Rn_element001]
  conduct = 2
  density = 1
  expand = 3
  formula = Rn
  name = G4_Rn
  specific = 4
FEATURE [App::DocumentObjectGroupPython] Fr_element001  label="Fr_element : 1"  # scripted group (container) (typed FeaturePython)
  n = 1
  ref = Fr_element
FEATURE [App::DocumentObjectGroupPython] G4_Fr  # scripted group (container) (typed FeaturePython)
  Dunit = g/cm3
  Dvalue = 1
  Group = -> [Fr_element001]
  conduct = 2
  density = 1
  expand = 3
  formula = Fr
  name = G4_Fr
  specific = 4
FEATURE [App::DocumentObjectGroupPython] Ra_element001  label="Ra_element : 1"  # scripted group (container) (typed FeaturePython)
  n = 1
  ref = Ra_element
FEATURE [App::DocumentObjectGroupPython] G4_Ra  # scripted group (container) (typed FeaturePython)
  Dunit = g/cm3
  Dvalue = 5
  Group = -> [Ra_element001]
  conduct = 2
  density = 1
  expand = 3
  formula = Ra
  name = G4_Ra
  specific = 4
FEATURE [App::DocumentObjectGroupPython] Ac_element001  label="Ac_element : 1"  # scripted group (container) (typed FeaturePython)
  n = 1
  ref = Ac_element
FEATURE [App::DocumentObjectGroupPython] G4_Ac  # scripted group (container) (typed FeaturePython)
  Dunit = g/cm3
  Dvalue = 10.07
  Group = -> [Ac_element001]
  conduct = 2
  density = 1
  expand = 3
  formula = Ac
  name = G4_Ac
  specific = 4
FEATURE [App::DocumentObjectGroupPython] Th_element001  label="Th_element : 1"  # scripted group (container) (typed FeaturePython)
  n = 1
  ref = Th_element
FEATURE [App::DocumentObjectGroupPython] G4_Th  # scripted group (container) (typed FeaturePython)
  Dunit = g/cm3
  Dvalue = 11.72
  Group = -> [Th_element001]
  conduct = 2
  density = 1
  expand = 3
  formula = Th
  name = G4_Th
  specific = 4
FEATURE [App::DocumentObjectGroupPython] Pa_element001  label="Pa_element : 1"  # scripted group (container) (typed FeaturePython)
  n = 1
  ref = Pa_element
FEATURE [App::DocumentObjectGroupPython] G4_Pa  # scripted group (container) (typed FeaturePython)
  Dunit = g/cm3
  Dvalue = 15.37
  Group = -> [Pa_element001]
  conduct = 2
  density = 1
  expand = 3
  formula = Pa
  name = G4_Pa
  specific = 4
FEATURE [App::DocumentObjectGroupPython] U_element004  label="U_element : 004"  # scripted group (container) (typed FeaturePython)
  n = 1
  ref = U_element
FEATURE [App::DocumentObjectGroupPython] G4_U  # scripted group (container) (typed FeaturePython)
  Dunit = g/cm3
  Dvalue = 18.95
  Group = -> [U_element004]
  conduct = 2
  density = 1
  expand = 3
  formula = U
  name = G4_U
  specific = 4
FEATURE [App::DocumentObjectGroupPython] Np_element001  label="Np_element : 1"  # scripted group (container) (typed FeaturePython)
  n = 1
  ref = Np_element
FEATURE [App::DocumentObjectGroupPython] G4_Np  # scripted group (container) (typed FeaturePython)
  Dunit = g/cm3
  Dvalue = 20.25
  Group = -> [Np_element001]
  conduct = 2
  density = 1
  expand = 3
  formula = Np
  name = G4_Np
  specific = 4
FEATURE [App::DocumentObjectGroupPython] Pu_element002  label="Pu_element : 002"  # scripted group (container) (typed FeaturePython)
  n = 1
  ref = Pu_element
FEATURE [App::DocumentObjectGroupPython] G4_Pu  # scripted group (container) (typed FeaturePython)
  Dunit = g/cm3
  Dvalue = 19.84
  Group = -> [Pu_element002]
  conduct = 2
  density = 1
  expand = 3
  formula = Pu
  name = G4_Pu
  specific = 4
FEATURE [App::DocumentObjectGroupPython] Am_element001  label="Am_element : 1"  # scripted group (container) (typed FeaturePython)
  n = 1
  ref = Am_element
FEATURE [App::DocumentObjectGroupPython] G4_Am  # scripted group (container) (typed FeaturePython)
  Dunit = g/cm3
  Dvalue = 13.67
  Group = -> [Am_element001]
  conduct = 2
  density = 1
  expand = 3
  formula = Am
  name = G4_Am
  specific = 4
FEATURE [App::DocumentObjectGroupPython] Cm_element001  label="Cm_element : 1"  # scripted group (container) (typed FeaturePython)
  n = 1
  ref = Cm_element
FEATURE [App::DocumentObjectGroupPython] G4_Cm  # scripted group (container) (typed FeaturePython)
  Dunit = g/cm3
  Dvalue = 13.51
  Group = -> [Cm_element001]
  conduct = 2
  density = 1
  expand = 3
  formula = Cm
  name = G4_Cm
  specific = 4
FEATURE [App::DocumentObjectGroupPython] Bk_element001  label="Bk_element : 1"  # scripted group (container) (typed FeaturePython)
  n = 1
  ref = Bk_element
FEATURE [App::DocumentObjectGroupPython] G4_Bk  # scripted group (container) (typed FeaturePython)
  Dunit = g/cm3
  Dvalue = 14
  Group = -> [Bk_element001]
  conduct = 2
  density = 1
  expand = 3
  formula = Bk
  name = G4_Bk
  specific = 4
FEATURE [App::DocumentObjectGroupPython] Cf_element001  label="Cf_element : 1"  # scripted group (container) (typed FeaturePython)
  n = 1
  ref = Cf_element
FEATURE [App::DocumentObjectGroupPython] G4_Cf  # scripted group (container) (typed FeaturePython)
  Dunit = g/cm3
  Dvalue = 10
  Group = -> [Cf_element001]
  conduct = 2
  density = 1
  expand = 3
  formula = Cf
  name = G4_Cf
  specific = 4
FEATURE [App::DocumentObjectGroupPython] Element  # scripted group (container) (typed FeaturePython)
  Group = -> [G4_H,G4_He,G4_Li,G4_Be,G4_B,G4_C,G4_N,G4_O,G4_F,G4_Ne,G4_Na,G4_Mg,G4_Al,G4_Si,G4_P,G4_S,G4_Cl,G4_Ar,G4_K,G4_Ca,G4_Sc,G4_Ti,G4_V,G4_Cr,G4_Mn,G4_Fe,G4_Co,G4_Ni,G4_Cu,G4_Zn,G4_Ga,G4_Ge,G4_As,G4_Se,G4_Br,G4_Kr,G4_Rb,G4_Sr,G4_Y,G4_Zr,G4_Nb,G4_Mo,G4_Tc,G4_Ru,G4_Rh,G4_Pd,G4_Ag,G4_Cd,G4_In,G4_Sn,G4_Sb,G4_Te,G4_I,G4_Xe,G4_Cs,G4_Ba,G4_La,G4_Ce,G4_Pr,G4_Nd,G4_Pm,G4_Sm,G4_Eu,G4_Gd,G4_Tb,G4_Dy,G4_Ho,G4_Er,+30 more]
FEATURE [App::DocumentObjectGroupPython] H_element114  label="H_element : 063"  # scripted group (container) (typed FeaturePython)
  n = 2
  ref = H_element
FEATURE [App::DocumentObjectGroupPython] G4_lH2  # scripted group (container) (typed FeaturePython)
  Dunit = g/cm3
  Dvalue = 0.0708
  Group = -> [H_element114]
  conduct = 2
  density = 1
  expand = 3
  formula = G4_lH2
  name = G4_lH2
  specific = 4
FEATURE [App::DocumentObjectGroupPython] N_element049  label="N_element : 022"  # scripted group (container) (typed FeaturePython)
  n = 2
  ref = N_element
FEATURE [App::DocumentObjectGroupPython] G4_lN2  # scripted group (container) (typed FeaturePython)
  Dunit = g/cm3
  Dvalue = 0.807
  Group = -> [N_element049]
  conduct = 2
  density = 1
  expand = 3
  formula = G4_lN2
  name = G4_lN2
  specific = 4
FEATURE [App::DocumentObjectGroupPython] O_element106  label="O_element : 060"  # scripted group (container) (typed FeaturePython)
  n = 2
  ref = O_element
FEATURE [App::DocumentObjectGroupPython] G4_lO2  # scripted group (container) (typed FeaturePython)
  Dunit = g/cm3
  Dvalue = 1.141
  Group = -> [O_element106]
  conduct = 2
  density = 1
  expand = 3
  formula = G4_lO2
  name = G4_lO2
  specific = 4
FEATURE [App::DocumentObjectGroupPython] Ar_element003  label="Ar_element : 002"  # scripted group (container) (typed FeaturePython)
  n = 1
  ref = Ar_element
FEATURE [App::DocumentObjectGroupPython] G4_lAr  # scripted group (container) (typed FeaturePython)
  Dunit = g/cm3
  Dvalue = 1.396
  Group = -> [Ar_element003]
  conduct = 2
  density = 1
  expand = 3
  formula = G4_lAr
  name = G4_lAr
  specific = 4
FEATURE [App::DocumentObjectGroupPython] Br_element008  label="Br_element : 005"  # scripted group (container) (typed FeaturePython)
  n = 1
  ref = Br_element
FEATURE [App::DocumentObjectGroupPython] G4_lBr  # scripted group (container) (typed FeaturePython)
  Dunit = g/cm3
  Dvalue = 3.1028
  Group = -> [Br_element008]
  conduct = 2
  density = 1
  expand = 3
  formula = G4_lBr
  name = G4_lBr
  specific = 4
FEATURE [App::DocumentObjectGroupPython] Kr_element002  label="Kr_element : 002"  # scripted group (container) (typed FeaturePython)
  n = 1
  ref = Kr_element
FEATURE [App::DocumentObjectGroupPython] G4_lKr  # scripted group (container) (typed FeaturePython)
  Dunit = g/cm3
  Dvalue = 2.418
  Group = -> [Kr_element002]
  conduct = 2
  density = 1
  expand = 3
  formula = G4_lKr
  name = G4_lKr
  specific = 4
FEATURE [App::DocumentObjectGroupPython] Xe_element002  label="Xe_element : 002"  # scripted group (container) (typed FeaturePython)
  n = 1
  ref = Xe_element
FEATURE [App::DocumentObjectGroupPython] G4_lXe  # scripted group (container) (typed FeaturePython)
  Dunit = g/cm3
  Dvalue = 2.953
  Group = -> [Xe_element002]
  conduct = 2
  density = 1
  expand = 3
  formula = G4_lXe
  name = G4_lXe
  specific = 4
FEATURE [App::DocumentObjectGroupPython] O_element107  label="O_element : 061"  # scripted group (container) (typed FeaturePython)
  n = 4
  ref = O_element
FEATURE [App::DocumentObjectGroupPython] Pb_element004  label="Pb_element : 002"  # scripted group (container) (typed FeaturePython)
  n = 1
  ref = Pb_element
FEATURE [App::DocumentObjectGroupPython] W_element005  label="W_element : 005"  # scripted group (container) (typed FeaturePython)
  n = 1
  ref = W_element
FEATURE [App::DocumentObjectGroupPython] G4_PbWO4  # scripted group (container) (typed FeaturePython)
  Dunit = g/cm3
  Dvalue = 8.28
  Group = -> [O_element107,Pb_element004,W_element005]
  conduct = 2
  density = 1
  expand = 3
  formula = G4_PbWO4
  name = G4_PbWO4
  specific = 4
FEATURE [App::DocumentObjectGroupPython] H_element115  label="H_element : 064"  # scripted group (container) (typed FeaturePython)
  n = 1
  ref = H_element
FEATURE [App::DocumentObjectGroupPython] G4_Galactic  # scripted group (container) (typed FeaturePython)
  Dunit = g/cm3
  Dvalue = 0
  Group = -> [H_element115]
  conduct = 2
  density = 1
  expand = 3
  formula = G4_Galactic
  name = G4_Galactic
  specific = 4
FEATURE [App::DocumentObjectGroupPython] C_element125  label="C_element : 071"  # scripted group (container) (typed FeaturePython)
  n = 1
  ref = C_element
FEATURE [App::DocumentObjectGroupPython] G4_GRAPHITE_POROUS  # scripted group (container) (typed FeaturePython)
  Dunit = g/cm3
  Dvalue = 1.7
  Group = -> [C_element125]
  conduct = 2
  density = 1
  expand = 3
  formula = G4_GRAPHITE_POROUS
  name = G4_GRAPHITE_POROUS
  specific = 4
FEATURE [App::DocumentObjectGroupPython] H_element116  label="H_element : 0.150"  # scripted group (container) (typed FeaturePython)
  n = 0.080538
FEATURE [App::DocumentObjectGroupPython] C_element126  label="C_element : 0.600"  # scripted group (container) (typed FeaturePython)
  n = 0.599848
FEATURE [App::DocumentObjectGroupPython] O_element108  label="O_element : 0.320"  # scripted group (container) (typed FeaturePython)
  n = 0.319614
FEATURE [App::DocumentObjectGroupPython] G4_LUCITE  # scripted group (container) (typed FeaturePython)
  Dunit = g/cm3
  Dvalue = 1.19
  Group = -> [H_element116,C_element126,O_element108]
  conduct = 2
  density = 1
  expand = 3
  formula = G4_LUCITE
  name = G4_LUCITE
  specific = 4
FEATURE [App::DocumentObjectGroupPython] Cu_element002  label="Cu_element : 62"  # scripted group (container) (typed FeaturePython)
  n = 62
  ref = Cu_element
FEATURE [App::DocumentObjectGroupPython] Zn_element002  label="Zn_element : 35"  # scripted group (container) (typed FeaturePython)
  n = 35
  ref = Zn_element
FEATURE [App::DocumentObjectGroupPython] Pb_element005  label="Pb_element : 3"  # scripted group (container) (typed FeaturePython)
  n = 3
  ref = Pb_element
FEATURE [App::DocumentObjectGroupPython] G4_BRASS  # scripted group (container) (typed FeaturePython)
  Dunit = g/cm3
  Dvalue = 8.52
  Group = -> [Cu_element002,Zn_element002,Pb_element005]
  conduct = 2
  density = 1
  expand = 3
  formula = G4_BRASS
  name = G4_BRASS
  specific = 4
FEATURE [App::DocumentObjectGroupPython] Cu_element003  label="Cu_element : 89"  # scripted group (container) (typed FeaturePython)
  n = 89
  ref = Cu_element
FEATURE [App::DocumentObjectGroupPython] Zn_element003  label="Zn_element : 9"  # scripted group (container) (typed FeaturePython)
  n = 9
  ref = Zn_element
FEATURE [App::DocumentObjectGroupPython] Pb_element006  label="Pb_element : 2"  # scripted group (container) (typed FeaturePython)
  n = 2
  ref = Pb_element
FEATURE [App::DocumentObjectGroupPython] G4_BRONZE  # scripted group (container) (typed FeaturePython)
  Dunit = g/cm3
  Dvalue = 8.82
  Group = -> [Cu_element003,Zn_element003,Pb_element006]
  conduct = 2
  density = 1
  expand = 3
  formula = G4_BRONZE
  name = G4_BRONZE
  specific = 4
FEATURE [App::DocumentObjectGroupPython] Fe_element008  label="Fe_element : 74"  # scripted group (container) (typed FeaturePython)
  n = 74
  ref = Fe_element
FEATURE [App::DocumentObjectGroupPython] Cr_element002  label="Cr_element : 18"  # scripted group (container) (typed FeaturePython)
  n = 18
  ref = Cr_element
FEATURE [App::DocumentObjectGroupPython] Ni_element002  label="Ni_element : 8"  # scripted group (container) (typed FeaturePython)
  n = 8
  ref = Ni_element
FEATURE [App::DocumentObjectGroupPython] G4_STAINLESS_STEEL  label="G4_STAINLESS-STEEL"  # scripted group (container) (typed FeaturePython)
  Dunit = g/cm3
  Dvalue = 8
  Group = -> [Fe_element008,Cr_element002,Ni_element002]
  conduct = 2
  density = 1
  expand = 3
  formula = G4_STAINLESS-STEEL
  name = G4_STAINLESS-STEEL
  specific = 4
FEATURE [App::DocumentObjectGroupPython] H_element117  label="H_element : 065"  # scripted group (container) (typed FeaturePython)
  n = 18
  ref = H_element
FEATURE [App::DocumentObjectGroupPython] C_element127  label="C_element : 072"  # scripted group (container) (typed FeaturePython)
  n = 12
  ref = C_element
FEATURE [App::DocumentObjectGroupPython] O_element109  label="O_element : 062"  # scripted group (container) (typed FeaturePython)
  n = 7
  ref = O_element
FEATURE [App::DocumentObjectGroupPython] G4_CR39  # scripted group (container) (typed FeaturePython)
  Dunit = g/cm3
  Dvalue = 1.32
  Group = -> [H_element117,C_element127,O_element109]
  conduct = 2
  density = 1
  expand = 3
  formula = G4_CR39
  name = G4_CR39
  specific = 4
FEATURE [App::DocumentObjectGroupPython] H_element118  label="H_element : 38"  # scripted group (container) (typed FeaturePython)
  n = 38
  ref = H_element
FEATURE [App::DocumentObjectGroupPython] C_element128  label="C_element : 073"  # scripted group (container) (typed FeaturePython)
  n = 18
  ref = C_element
FEATURE [App::DocumentObjectGroupPython] O_element110  label="O_element : 063"  # scripted group (container) (typed FeaturePython)
  n = 1
  ref = O_element
FEATURE [App::DocumentObjectGroupPython] G4_OCTADECANOL  # scripted group (container) (typed FeaturePython)
  Dunit = g/cm3
  Dvalue = 0.812
  Group = -> [H_element118,C_element128,O_element110]
  conduct = 2
  density = 1
  expand = 3
  formula = G4_OCTADECANOL
  name = G4_OCTADECANOL
  specific = 4
FEATURE [App::DocumentObjectGroupPython] HEP  # scripted group (container) (typed FeaturePython)
  Group = -> [G4_lH2,G4_lN2,G4_lO2,G4_lAr,G4_lBr,G4_lKr,G4_lXe,G4_PbWO4,G4_Galactic,G4_GRAPHITE_POROUS,G4_LUCITE,G4_BRASS,G4_BRONZE,G4_STAINLESS_STEEL,G4_CR39,G4_OCTADECANOL]
FEATURE [App::DocumentObjectGroupPython] C_element129  label="C_element : 074"  # scripted group (container) (typed FeaturePython)
  n = 14
  ref = C_element
FEATURE [App::DocumentObjectGroupPython] H_element119  label="H_element : 066"  # scripted group (container) (typed FeaturePython)
  n = 10
  ref = H_element
FEATURE [App::DocumentObjectGroupPython] O_element111  label="O_element : 064"  # scripted group (container) (typed FeaturePython)
  n = 2
  ref = O_element
FEATURE [App::DocumentObjectGroupPython] N_element050  label="N_element : 023"  # scripted group (container) (typed FeaturePython)
  n = 2
  ref = N_element
FEATURE [App::DocumentObjectGroupPython] G4_KEVLAR  # scripted group (container) (typed FeaturePython)
  Dunit = g/cm3
  Dvalue = 1.44
  Group = -> [C_element129,H_element119,O_element111,N_element050]
  conduct = 2
  density = 1
  expand = 3
  formula = G4_KEVLAR
  name = G4_KEVLAR
  specific = 4
FEATURE [App::DocumentObjectGroupPython] C_element130  label="C_element : 075"  # scripted group (container) (typed FeaturePython)
  n = 10
  ref = C_element
FEATURE [App::DocumentObjectGroupPython] H_element120  label="H_element : 067"  # scripted group (container) (typed FeaturePython)
  n = 8
  ref = H_element
FEATURE [App::DocumentObjectGroupPython] O_element112  label="O_element : 065"  # scripted group (container) (typed FeaturePython)
  n = 4
  ref = O_element
FEATURE [App::DocumentObjectGroupPython] G4_DACRON  # scripted group (container) (typed FeaturePython)
  Dunit = g/cm3
  Dvalue = 1.4
  Group = -> [C_element130,H_element120,O_element112]
  conduct = 2
  density = 1
  expand = 3
  formula = G4_DACRON
  name = G4_DACRON
  specific = 4
FEATURE [App::DocumentObjectGroupPython] C_element131  label="C_element : 076"  # scripted group (container) (typed FeaturePython)
  n = 4
  ref = C_element
FEATURE [App::DocumentObjectGroupPython] H_element121  label="H_element : 068"  # scripted group (container) (typed FeaturePython)
  n = 5
  ref = H_element
FEATURE [App::DocumentObjectGroupPython] Cl_element030  label="Cl_element : 016"  # scripted group (container) (typed FeaturePython)
  n = 1
  ref = Cl_element
FEATURE [App::DocumentObjectGroupPython] G4_NEOPRENE  # scripted group (container) (typed FeaturePython)
  Dunit = g/cm3
  Dvalue = 1.23
  Group = -> [C_element131,H_element121,Cl_element030]
  conduct = 2
  density = 1
  expand = 3
  formula = G4_NEOPRENE
  name = G4_NEOPRENE
  specific = 4
FEATURE [App::DocumentObjectGroupPython] Space  # scripted group (container) (typed FeaturePython)
  Group = -> [G4_KEVLAR,G4_DACRON,G4_NEOPRENE]
FEATURE [App::DocumentObjectGroupPython] H_element122  label="H_element : 069"  # scripted group (container) (typed FeaturePython)
  n = 5
  ref = H_element
FEATURE [App::DocumentObjectGroupPython] C_element132  label="C_element : 077"  # scripted group (container) (typed FeaturePython)
  n = 4
  ref = C_element
FEATURE [App::DocumentObjectGroupPython] N_element051  label="N_element : 3"  # scripted group (container) (typed FeaturePython)
  n = 3
  ref = N_element
FEATURE [App::DocumentObjectGroupPython] O_element113  label="O_element : 066"  # scripted group (container) (typed FeaturePython)
  n = 1
  ref = O_element
FEATURE [App::DocumentObjectGroupPython] G4_CYTOSINE  # scripted group (container) (typed FeaturePython)
  Dunit = g/cm3
  Dvalue = 1.55
  Group = -> [H_element122,C_element132,N_element051,O_element113]
  conduct = 2
  density = 1
  expand = 3
  formula = G4_CYTOSINE
  name = G4_CYTOSINE
  specific = 4
FEATURE [App::DocumentObjectGroupPython] H_element123  label="H_element : 070"  # scripted group (container) (typed FeaturePython)
  n = 6
  ref = H_element
FEATURE [App::DocumentObjectGroupPython] C_element133  label="C_element : 078"  # scripted group (container) (typed FeaturePython)
  n = 5
  ref = C_element
FEATURE [App::DocumentObjectGroupPython] N_element052  label="N_element : 024"  # scripted group (container) (typed FeaturePython)
  n = 2
  ref = N_element
FEATURE [App::DocumentObjectGroupPython] O_element114  label="O_element : 067"  # scripted group (container) (typed FeaturePython)
  n = 2
  ref = O_element
FEATURE [App::DocumentObjectGroupPython] G4_THYMINE  # scripted group (container) (typed FeaturePython)
  Dunit = g/cm3
  Dvalue = 1.23
  Group = -> [H_element123,C_element133,N_element052,O_element114]
  conduct = 2
  density = 1
  expand = 3
  formula = G4_THYMINE
  name = G4_THYMINE
  specific = 4
FEATURE [App::DocumentObjectGroupPython] H_element124  label="H_element : 071"  # scripted group (container) (typed FeaturePython)
  n = 4
  ref = H_element
FEATURE [App::DocumentObjectGroupPython] C_element134  label="C_element : 079"  # scripted group (container) (typed FeaturePython)
  n = 4
  ref = C_element
FEATURE [App::DocumentObjectGroupPython] N_element053  label="N_element : 025"  # scripted group (container) (typed FeaturePython)
  n = 2
  ref = N_element
FEATURE [App::DocumentObjectGroupPython] O_element115  label="O_element : 068"  # scripted group (container) (typed FeaturePython)
  n = 2
  ref = O_element
FEATURE [App::DocumentObjectGroupPython] G4_URACIL  # scripted group (container) (typed FeaturePython)
  Dunit = g/cm3
  Dvalue = 1.32
  Group = -> [H_element124,C_element134,N_element053,O_element115]
  conduct = 2
  density = 1
  expand = 3
  formula = G4_URACIL
  name = G4_URACIL
  specific = 4
FEATURE [App::DocumentObjectGroupPython] H_element125  label="H_element : 072"  # scripted group (container) (typed FeaturePython)
  n = 4
  ref = H_element
FEATURE [App::DocumentObjectGroupPython] C_element135  label="C_element : 080"  # scripted group (container) (typed FeaturePython)
  n = 5
  ref = C_element
FEATURE [App::DocumentObjectGroupPython] N_element054  label="N_element : 026"  # scripted group (container) (typed FeaturePython)
  n = 5
  ref = N_element
FEATURE [App::DocumentObjectGroupPython] G4_DNA_ADENINE  # scripted group (container) (typed FeaturePython)
  Dunit = g/cm3
  Dvalue = 1
  Group = -> [H_element125,C_element135,N_element054]
  conduct = 2
  density = 1
  expand = 3
  formula = G4_DNA_ADENINE
  name = G4_DNA_ADENINE
  specific = 4
FEATURE [App::DocumentObjectGroupPython] H_element126  label="H_element : 073"  # scripted group (container) (typed FeaturePython)
  n = 4
  ref = H_element
FEATURE [App::DocumentObjectGroupPython] C_element136  label="C_element : 081"  # scripted group (container) (typed FeaturePython)
  n = 5
  ref = C_element
FEATURE [App::DocumentObjectGroupPython] N_element055  label="N_element : 027"  # scripted group (container) (typed FeaturePython)
  n = 5
  ref = N_element
FEATURE [App::DocumentObjectGroupPython] O_element116  label="O_element : 069"  # scripted group (container) (typed FeaturePython)
  n = 1
  ref = O_element
FEATURE [App::DocumentObjectGroupPython] G4_DNA_GUANINE  # scripted group (container) (typed FeaturePython)
  Dunit = g/cm3
  Dvalue = 1
  Group = -> [H_element126,C_element136,N_element055,O_element116]
  conduct = 2
  density = 1
  expand = 3
  formula = G4_DNA_GUANINE
  name = G4_DNA_GUANINE
  specific = 4
FEATURE [App::DocumentObjectGroupPython] H_element127  label="H_element : 074"  # scripted group (container) (typed FeaturePython)
  n = 4
  ref = H_element
FEATURE [App::DocumentObjectGroupPython] C_element137  label="C_element : 082"  # scripted group (container) (typed FeaturePython)
  n = 4
  ref = C_element
FEATURE [App::DocumentObjectGroupPython] N_element056  label="N_element : 028"  # scripted group (container) (typed FeaturePython)
  n = 3
  ref = N_element
FEATURE [App::DocumentObjectGroupPython] O_element117  label="O_element : 070"  # scripted group (container) (typed FeaturePython)
  n = 1
  ref = O_element
FEATURE [App::DocumentObjectGroupPython] G4_DNA_CYTOSINE  # scripted group (container) (typed FeaturePython)
  Dunit = g/cm3
  Dvalue = 1
  Group = -> [H_element127,C_element137,N_element056,O_element117]
  conduct = 2
  density = 1
  expand = 3
  formula = G4_DNA_CYTOSINE
  name = G4_DNA_CYTOSINE
  specific = 4
FEATURE [App::DocumentObjectGroupPython] H_element128  label="H_element : 075"  # scripted group (container) (typed FeaturePython)
  n = 5
  ref = H_element
FEATURE [App::DocumentObjectGroupPython] C_element138  label="C_element : 083"  # scripted group (container) (typed FeaturePython)
  n = 5
  ref = C_element
FEATURE [App::DocumentObjectGroupPython] N_element057  label="N_element : 029"  # scripted group (container) (typed FeaturePython)
  n = 2
  ref = N_element
FEATURE [App::DocumentObjectGroupPython] O_element118  label="O_element : 071"  # scripted group (container) (typed FeaturePython)
  n = 2
  ref = O_element
FEATURE [App::DocumentObjectGroupPython] G4_DNA_THYMINE  # scripted group (container) (typed FeaturePython)
  Dunit = g/cm3
  Dvalue = 1
  Group = -> [H_element128,C_element138,N_element057,O_element118]
  conduct = 2
  density = 1
  expand = 3
  formula = G4_DNA_THYMINE
  name = G4_DNA_THYMINE
  specific = 4
FEATURE [App::DocumentObjectGroupPython] H_element129  label="H_element : 076"  # scripted group (container) (typed FeaturePython)
  n = 3
  ref = H_element
FEATURE [App::DocumentObjectGroupPython] C_element139  label="C_element : 084"  # scripted group (container) (typed FeaturePython)
  n = 4
  ref = C_element
FEATURE [App::DocumentObjectGroupPython] N_element058  label="N_element : 030"  # scripted group (container) (typed FeaturePython)
  n = 2
  ref = N_element
FEATURE [App::DocumentObjectGroupPython] O_element119  label="O_element : 072"  # scripted group (container) (typed FeaturePython)
  n = 2
  ref = O_element
FEATURE [App::DocumentObjectGroupPython] G4_DNA_URACIL  # scripted group (container) (typed FeaturePython)
  Dunit = g/cm3
  Dvalue = 1
  Group = -> [H_element129,C_element139,N_element058,O_element119]
  conduct = 2
  density = 1
  expand = 3
  formula = G4_DNA_URACIL
  name = G4_DNA_URACIL
  specific = 4
FEATURE [App::DocumentObjectGroupPython] H_element130  label="H_element : 077"  # scripted group (container) (typed FeaturePython)
  n = 10
  ref = H_element
FEATURE [App::DocumentObjectGroupPython] C_element140  label="C_element : 085"  # scripted group (container) (typed FeaturePython)
  n = 10
  ref = C_element
FEATURE [App::DocumentObjectGroupPython] N_element059  label="N_element : 031"  # scripted group (container) (typed FeaturePython)
  n = 5
  ref = N_element
FEATURE [App::DocumentObjectGroupPython] O_element120  label="O_element : 073"  # scripted group (container) (typed FeaturePython)
  n = 4
  ref = O_element
FEATURE [App::DocumentObjectGroupPython] G4_DNA_ADENOSINE  # scripted group (container) (typed FeaturePython)
  Dunit = g/cm3
  Dvalue = 1
  Group = -> [H_element130,C_element140,N_element059,O_element120]
  conduct = 2
  density = 1
  expand = 3
  formula = G4_DNA_ADENOSINE
  name = G4_DNA_ADENOSINE
  specific = 4
FEATURE [App::DocumentObjectGroupPython] H_element131  label="H_element : 078"  # scripted group (container) (typed FeaturePython)
  n = 10
  ref = H_element
FEATURE [App::DocumentObjectGroupPython] C_element141  label="C_element : 086"  # scripted group (container) (typed FeaturePython)
  n = 10
  ref = C_element
FEATURE [App::DocumentObjectGroupPython] N_element060  label="N_element : 032"  # scripted group (container) (typed FeaturePython)
  n = 5
  ref = N_element
FEATURE [App::DocumentObjectGroupPython] O_element121  label="O_element : 074"  # scripted group (container) (typed FeaturePython)
  n = 5
  ref = O_element
FEATURE [App::DocumentObjectGroupPython] G4_DNA_GUANOSINE  # scripted group (container) (typed FeaturePython)
  Dunit = g/cm3
  Dvalue = 1
  Group = -> [H_element131,C_element141,N_element060,O_element121]
  conduct = 2
  density = 1
  expand = 3
  formula = G4_DNA_GUANOSINE
  name = G4_DNA_GUANOSINE
  specific = 4
FEATURE [App::DocumentObjectGroupPython] H_element132  label="H_element : 079"  # scripted group (container) (typed FeaturePython)
  n = 10
  ref = H_element
FEATURE [App::DocumentObjectGroupPython] C_element142  label="C_element : 087"  # scripted group (container) (typed FeaturePython)
  n = 9
  ref = C_element
FEATURE [App::DocumentObjectGroupPython] N_element061  label="N_element : 033"  # scripted group (container) (typed FeaturePython)
  n = 3
  ref = N_element
FEATURE [App::DocumentObjectGroupPython] O_element122  label="O_element : 075"  # scripted group (container) (typed FeaturePython)
  n = 5
  ref = O_element
FEATURE [App::DocumentObjectGroupPython] G4_DNA_CYTIDINE  # scripted group (container) (typed FeaturePython)
  Dunit = g/cm3
  Dvalue = 1
  Group = -> [H_element132,C_element142,N_element061,O_element122]
  conduct = 2
  density = 1
  expand = 3
  formula = G4_DNA_CYTIDINE
  name = G4_DNA_CYTIDINE
  specific = 4
FEATURE [App::DocumentObjectGroupPython] H_element133  label="H_element : 080"  # scripted group (container) (typed FeaturePython)
  n = 9
  ref = H_element
FEATURE [App::DocumentObjectGroupPython] C_element143  label="C_element : 088"  # scripted group (container) (typed FeaturePython)
  n = 9
  ref = C_element
FEATURE [App::DocumentObjectGroupPython] N_element062  label="N_element : 034"  # scripted group (container) (typed FeaturePython)
  n = 2
  ref = N_element
FEATURE [App::DocumentObjectGroupPython] O_element123  label="O_element : 076"  # scripted group (container) (typed FeaturePython)
  n = 6
  ref = O_element
FEATURE [App::DocumentObjectGroupPython] G4_DNA_URIDINE  # scripted group (container) (typed FeaturePython)
  Dunit = g/cm3
  Dvalue = 1
  Group = -> [H_element133,C_element143,N_element062,O_element123]
  conduct = 2
  density = 1
  expand = 3
  formula = G4_DNA_URIDINE
  name = G4_DNA_URIDINE
  specific = 4
FEATURE [App::DocumentObjectGroupPython] H_element134  label="H_element : 081"  # scripted group (container) (typed FeaturePython)
  n = 11
  ref = H_element
FEATURE [App::DocumentObjectGroupPython] C_element144  label="C_element : 089"  # scripted group (container) (typed FeaturePython)
  n = 10
  ref = C_element
FEATURE [App::DocumentObjectGroupPython] N_element063  label="N_element : 035"  # scripted group (container) (typed FeaturePython)
  n = 2
  ref = N_element
FEATURE [App::DocumentObjectGroupPython] O_element124  label="O_element : 077"  # scripted group (container) (typed FeaturePython)
  n = 6
  ref = O_element
FEATURE [App::DocumentObjectGroupPython] G4_DNA_METHYLURIDINE  # scripted group (container) (typed FeaturePython)
  Dunit = g/cm3
  Dvalue = 1
  Group = -> [H_element134,C_element144,N_element063,O_element124]
  conduct = 2
  density = 1
  expand = 3
  formula = G4_DNA_METHYLURIDINE
  name = G4_DNA_METHYLURIDINE
  specific = 4
FEATURE [App::DocumentObjectGroupPython] P_element014  label="P_element : 003"  # scripted group (container) (typed FeaturePython)
  n = 1
  ref = P_element
FEATURE [App::DocumentObjectGroupPython] O_element125  label="O_element : 078"  # scripted group (container) (typed FeaturePython)
  n = 3
  ref = O_element
FEATURE [App::DocumentObjectGroupPython] G4_DNA_MONOPHOSPHATE  # scripted group (container) (typed FeaturePython)
  Dunit = g/cm3
  Dvalue = 1
  Group = -> [P_element014,O_element125]
  conduct = 2
  density = 1
  expand = 3
  formula = G4_DNA_MONOPHOSPHATE
  name = G4_DNA_MONOPHOSPHATE
  specific = 4
FEATURE [App::DocumentObjectGroupPython] H_element135  label="H_element : 082"  # scripted group (container) (typed FeaturePython)
  n = 10
  ref = H_element
FEATURE [App::DocumentObjectGroupPython] C_element145  label="C_element : 090"  # scripted group (container) (typed FeaturePython)
  n = 10
  ref = C_element
FEATURE [App::DocumentObjectGroupPython] N_element064  label="N_element : 036"  # scripted group (container) (typed FeaturePython)
  n = 5
  ref = N_element
FEATURE [App::DocumentObjectGroupPython] O_element126  label="O_element : 079"  # scripted group (container) (typed FeaturePython)
  n = 7
  ref = O_element
FEATURE [App::DocumentObjectGroupPython] P_element015  label="P_element : 004"  # scripted group (container) (typed FeaturePython)
  n = 1
  ref = P_element
FEATURE [App::DocumentObjectGroupPython] G4_DNA_A  # scripted group (container) (typed FeaturePython)
  Dunit = g/cm3
  Dvalue = 1
  Group = -> [H_element135,C_element145,N_element064,O_element126,P_element015]
  conduct = 2
  density = 1
  expand = 3
  formula = G4_DNA_A
  name = G4_DNA_A
  specific = 4
FEATURE [App::DocumentObjectGroupPython] H_element136  label="H_element : 083"  # scripted group (container) (typed FeaturePython)
  n = 10
  ref = H_element
FEATURE [App::DocumentObjectGroupPython] C_element146  label="C_element : 091"  # scripted group (container) (typed FeaturePython)
  n = 10
  ref = C_element
FEATURE [App::DocumentObjectGroupPython] N_element065  label="N_element : 037"  # scripted group (container) (typed FeaturePython)
  n = 5
  ref = N_element
FEATURE [App::DocumentObjectGroupPython] O_element127  label="O_element : 8"  # scripted group (container) (typed FeaturePython)
  n = 8
  ref = O_element
FEATURE [App::DocumentObjectGroupPython] P_element016  label="P_element : 005"  # scripted group (container) (typed FeaturePython)
  n = 1
  ref = P_element
FEATURE [App::DocumentObjectGroupPython] G4_DNA_G  # scripted group (container) (typed FeaturePython)
  Dunit = g/cm3
  Dvalue = 1
  Group = -> [H_element136,C_element146,N_element065,O_element127,P_element016]
  conduct = 2
  density = 1
  expand = 3
  formula = G4_DNA_G
  name = G4_DNA_G
  specific = 4
FEATURE [App::DocumentObjectGroupPython] H_element137  label="H_element : 084"  # scripted group (container) (typed FeaturePython)
  n = 10
  ref = H_element
FEATURE [App::DocumentObjectGroupPython] C_element147  label="C_element : 092"  # scripted group (container) (typed FeaturePython)
  n = 9
  ref = C_element
FEATURE [App::DocumentObjectGroupPython] N_element066  label="N_element : 038"  # scripted group (container) (typed FeaturePython)
  n = 3
  ref = N_element
FEATURE [App::DocumentObjectGroupPython] O_element128  label="O_element : 080"  # scripted group (container) (typed FeaturePython)
  n = 8
  ref = O_element
FEATURE [App::DocumentObjectGroupPython] P_element017  label="P_element : 006"  # scripted group (container) (typed FeaturePython)
  n = 1
  ref = P_element
FEATURE [App::DocumentObjectGroupPython] G4_DNA_C  # scripted group (container) (typed FeaturePython)
  Dunit = g/cm3
  Dvalue = 1
  Group = -> [H_element137,C_element147,N_element066,O_element128,P_element017]
  conduct = 2
  density = 1
  expand = 3
  formula = G4_DNA_C
  name = G4_DNA_C
  specific = 4
FEATURE [App::DocumentObjectGroupPython] H_element138  label="H_element : 085"  # scripted group (container) (typed FeaturePython)
  n = 9
  ref = H_element
FEATURE [App::DocumentObjectGroupPython] C_element148  label="C_element : 093"  # scripted group (container) (typed FeaturePython)
  n = 9
  ref = C_element
FEATURE [App::DocumentObjectGroupPython] N_element067  label="N_element : 039"  # scripted group (container) (typed FeaturePython)
  n = 2
  ref = N_element
FEATURE [App::DocumentObjectGroupPython] O_element129  label="O_element : 9"  # scripted group (container) (typed FeaturePython)
  n = 9
  ref = O_element
FEATURE [App::DocumentObjectGroupPython] P_element018  label="P_element : 007"  # scripted group (container) (typed FeaturePython)
  n = 1
  ref = P_element
FEATURE [App::DocumentObjectGroupPython] G4_DNA_U  # scripted group (container) (typed FeaturePython)
  Dunit = g/cm3
  Dvalue = 1
  Group = -> [H_element138,C_element148,N_element067,O_element129,P_element018]
  conduct = 2
  density = 1
  expand = 3
  formula = G4_DNA_U
  name = G4_DNA_U
  specific = 4
FEATURE [App::DocumentObjectGroupPython] H_element139  label="H_element : 086"  # scripted group (container) (typed FeaturePython)
  n = 11
  ref = H_element
FEATURE [App::DocumentObjectGroupPython] C_element149  label="C_element : 094"  # scripted group (container) (typed FeaturePython)
  n = 10
  ref = C_element
FEATURE [App::DocumentObjectGroupPython] N_element068  label="N_element : 040"  # scripted group (container) (typed FeaturePython)
  n = 2
  ref = N_element
FEATURE [App::DocumentObjectGroupPython] O_element130  label="O_element : 081"  # scripted group (container) (typed FeaturePython)
  n = 9
  ref = O_element
FEATURE [App::DocumentObjectGroupPython] P_element019  label="P_element : 008"  # scripted group (container) (typed FeaturePython)
  n = 1
  ref = P_element
FEATURE [App::DocumentObjectGroupPython] G4_DNA_MU  # scripted group (container) (typed FeaturePython)
  Dunit = g/cm3
  Dvalue = 1
  Group = -> [H_element139,C_element149,N_element068,O_element130,P_element019]
  conduct = 2
  density = 1
  expand = 3
  formula = G4_DNA_MU
  name = G4_DNA_MU
  specific = 4
FEATURE [App::DocumentObjectGroupPython] BioChemical  # scripted group (container) (typed FeaturePython)
  Group = -> [G4_CYTOSINE,G4_THYMINE,G4_URACIL,G4_DNA_ADENINE,G4_DNA_GUANINE,G4_DNA_CYTOSINE,G4_DNA_THYMINE,G4_DNA_URACIL,G4_DNA_ADENOSINE,G4_DNA_GUANOSINE,G4_DNA_CYTIDINE,G4_DNA_URIDINE,G4_DNA_METHYLURIDINE,G4_DNA_MONOPHOSPHATE,G4_DNA_A,G4_DNA_G,G4_DNA_C,G4_DNA_U,G4_DNA_MU]
FEATURE [App::DocumentObjectGroupPython] G4Materials  # scripted group (container) (typed FeaturePython)
  Group = -> [NIST,Element,HEP,Space,BioChemical]
  version = 1
FEATURE [App::DocumentObjectGroupPython] Geant4  # scripted group (container) (typed FeaturePython)
  Group = -> [G4Isotopes,G4Elements,G4Materials]
FEATURE [App::DocumentObjectGroupPython] Materials  # scripted group (container) (typed FeaturePython)
  Group = -> [Geant4]
FEATURE [Part::FeaturePython] GDMLBox_WorldBox  # WARN: FeaturePython — macro-defined, semantics opaque (R4)
  lunit = 2
  material = 5
  x = 200.2
  y = 130
  z = 130
FEATURE [Part::FeaturePython] GDMLBox_Box  # WARN: FeaturePython — macro-defined, semantics opaque (R4)
  Placement = pos=(30,0,0) rot=(0,0,1;0rad)
  lunit = 2
  material = 0
  x = 10
  y = 10
  z = 10
FEATURE [Part::FeaturePython] GDMLTorus  # WARN: FeaturePython — macro-defined, semantics opaque (R4)
  Placement = pos=(30,0,0) rot=(0,1,0;1.5708rad)
  aunit = deg
  deltaphi = 360
  lunit = 2
  material = 0
  rmax = 2
  rmin = 0
  rtor = 8
  startphi = 0
FEATURE [Part::MultiFuse] Fusion
  Shapes = -> [GDMLBox_Box,GDMLTorus]
FEATURE [Part::FeaturePython] Array  # Draft array (typed FeaturePython)
  AlwaysSyncPlacement = false
  Angle = 180
  ArrayType = 1
  Axis = (0,0,1)
  Base = -> Fusion
  Center = (0,0,0)
  Count = 5
  ExpandArray = false
  Fuse = false
  IntervalAxis = (0,0,0)
  IntervalX = (50,0,0)
  IntervalY = (0,50,0)
  IntervalZ = (0,0,50)
  NumberCircles = 3
  NumberPolar = 5
  NumberX = 2
  NumberY = 2
  NumberZ = 1
  Placement = pos=(0,0,0) rot=(0,0,1;0.785398rad)
  PlacementList = 5 placements: [(0,0,0),(0,0,0),(0,0,0),(0,0,0),(0,0,0)]
  RadialDistance = 50
  ScaleList = (5) [(1,1,1),(1,1,1),(1,1,1),(1,1,1),(1,1,1)]
  Symmetry = 1
  TangentialDistance = 25
FEATURE [App::Part] Part001
  Group = -> [Array]
  Origin = -> Origin004
FEATURE [App::Part] worldVOL
  Group = -> [GDMLBox_WorldBox,Part001]
  Origin = -> Origin
